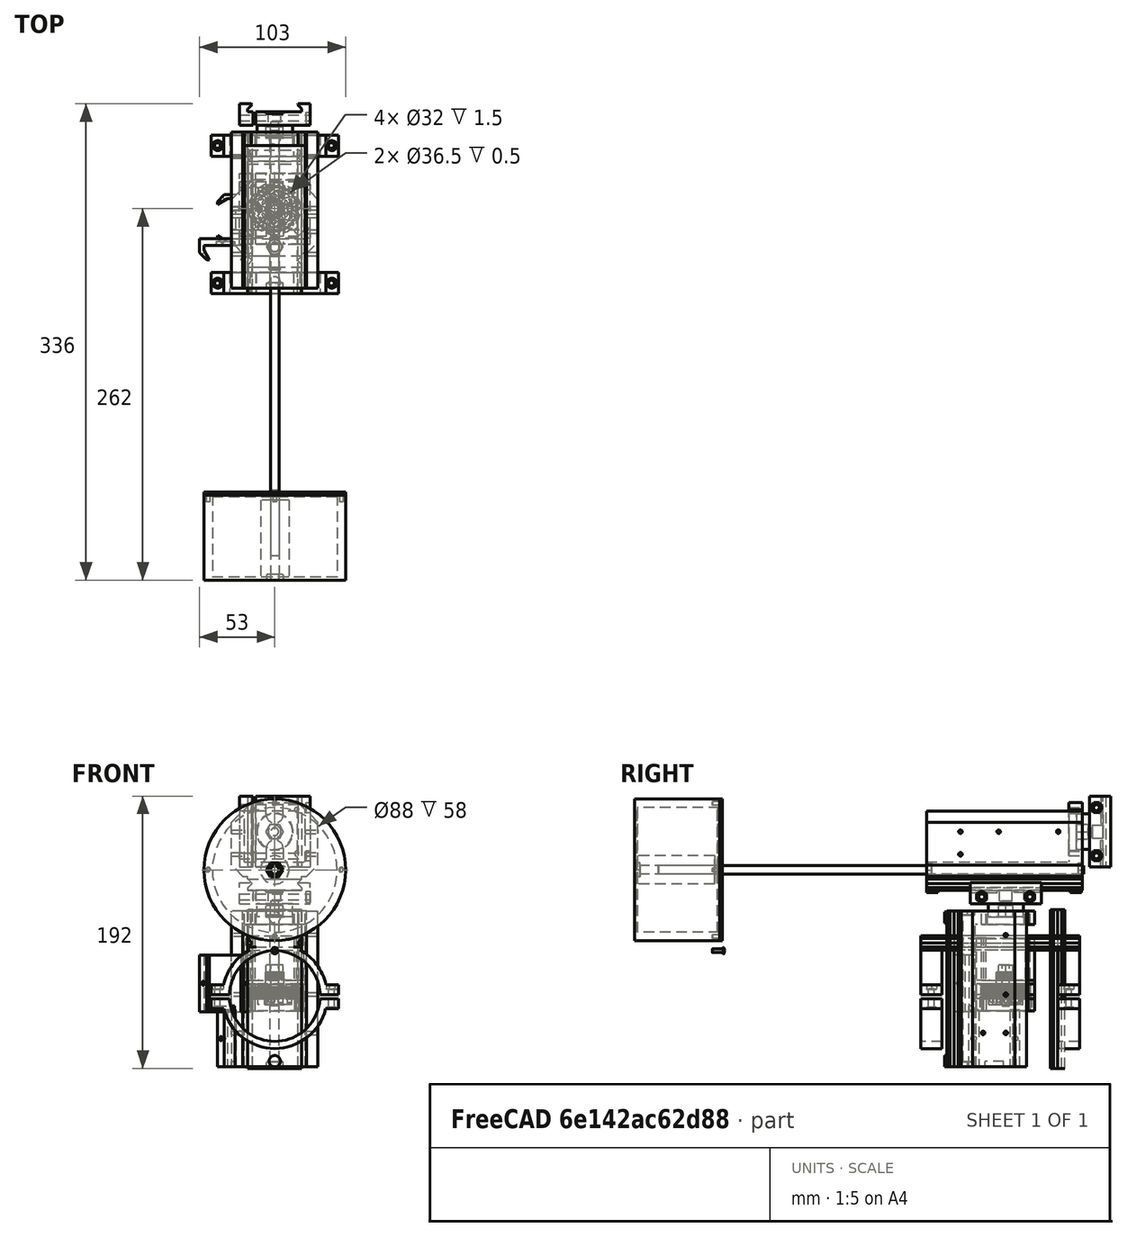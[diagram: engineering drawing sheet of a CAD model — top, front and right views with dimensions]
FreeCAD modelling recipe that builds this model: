
FCSTD DOCUMENT  (FreeCAD 0.17R12284 (Git))
Label: eq-mount-V1.0
License: All rights reserved
LicenseURL: http://en.wikipedia.org/wiki/All_rights_reserved
objects: Part::Feature×227, Part::Cylinder×217, Part::MultiFuse×182, Part::Cut×127, Part::Box×42, Part::FeaturePython×29, Part::Extrusion×25, App::Part×16, Sketcher::SketchObject×11, Part::Chamfer×8, Part::RegularPolygon×4
note: 872 computed .brp shape members not serialized (recipe doc carries the construction recipe); baked Part::Feature solids carry a one-line shape summary decoded from their .brp

FEATURE [Part::FeaturePython] InvoluteGear007  # WARN: FeaturePython — macro-defined, semantics opaque (R4)
  backlash = 0
  beta = 0
  clearance = 0.25
  double_helix = false
  head = 0
  height = 5.5
  module = 1.2
  numpoints = 6
  pressure_angle = 20
  reversed_backlash = false
  shift = 0
  simple = false
  teeth = 27
  undercut = false
FEATURE [Part::FeaturePython] InvoluteGear006  # WARN: FeaturePython — macro-defined, semantics opaque (R4)
  backlash = 0
  beta = 0
  clearance = 0.25
  double_helix = false
  head = 0
  height = 5.5
  module = 1.2
  numpoints = 6
  pressure_angle = 20
  reversed_backlash = false
  shift = 0
  simple = false
  teeth = 27
  undercut = false
FEATURE [Part::FeaturePython] InvoluteGear005  # WARN: FeaturePython — macro-defined, semantics opaque (R4)
  backlash = 0
  beta = 0
  clearance = 0.25
  double_helix = false
  head = 0
  height = 5.5
  module = 1.2
  numpoints = 6
  pressure_angle = 20
  reversed_backlash = false
  shift = 0
  simple = false
  teeth = 27
  undercut = false
FEATURE [Part::Cylinder] Cylinder007  label="Válec007"
  Angle = 360
  AttacherType = Attacher::AttachEngine3D
  Height = 1.5
  Radius = 20
FEATURE [Part::Cylinder] Cylinder008  label="Válec008"
  Angle = 360
  AttacherType = Attacher::AttachEngine3D
  Height = 1.5
  Radius = 16
FEATURE [Part::Cylinder] Cylinder006  label="Válec006"
  Angle = 360
  AttacherType = Attacher::AttachEngine3D
  Height = 1.5
  Radius = 16
FEATURE [Part::Cut] Cut  label="Ring2"
  Base = -> Cylinder007
  Placement = pos=(0,0,5.5) rot=(0,0,1;0rad)
  Tool = -> Cylinder006
FEATURE [Part::Cylinder] Cylinder009  label="Válec009"
  Angle = 360
  AttacherType = Attacher::AttachEngine3D
  Height = 1.5
  Radius = 20
FEATURE [Part::Cut] Cut003  label="Ring003"
  Base = -> Cylinder009
  Placement = pos=(0,0,-1.5) rot=(0,0,1;0rad)
  Tool = -> Cylinder008
FEATURE [Part::Cylinder] Cylinder005  label="Válec005"
  Angle = 360
  AttacherType = Attacher::AttachEngine3D
  Height = 5.5
  Radius = 20
FEATURE [Part::Cut] Cut002  label="ring 001"
  Base = -> Cylinder005
  Tool = -> InvoluteGear005
FEATURE [Part::MultiFuse] Fusion  label="Ring zaklad Fin"
  Shapes = -> [Cut002,Cut,Cut003]
FEATURE [Sketcher::SketchObject] Sketch001
  MapMode = 45
  Placement = pos=(44.88,21.011,5.40003) rot=(0.707106,0.001666,0.707106;3.13826rad)
  sketch-geometry (7):
    g0: LineSegment StartX=5 StartY=0 StartZ=0 EndX=2.5 EndY=4.33013 EndZ=0
    g1: LineSegment StartX=2.5 StartY=4.33013 StartZ=0 EndX=-2.5 EndY=4.33013 EndZ=0
    g2: LineSegment StartX=-2.5 StartY=4.33013 StartZ=0 EndX=-5 EndY=0 EndZ=0
    g3: LineSegment StartX=-5 StartY=0 StartZ=0 EndX=-2.5 EndY=-4.33013 EndZ=0
    g4: LineSegment StartX=-2.5 StartY=-4.33013 StartZ=0 EndX=2.5 EndY=-4.33013 EndZ=0
    g5: LineSegment StartX=2.5 StartY=-4.33013 StartZ=0 EndX=5 EndY=0 EndZ=0
    g6: Circle [constr] CenterX=0 CenterY=0 CenterZ=0 NormalX=0 NormalY=0 NormalZ=1 AngleXU=0 Radius=5
  constraints (14):
    c: Coincident(g0,g1)
    c: Coincident(g1,g2)
    c: Coincident(g2,g3)
    c: Coincident(g3,g4)
    c: Coincident(g4,g5)
    c: Coincident(g5,g0)
    c: Equal(g0, g1-g5) x5
    c: PointOnObject(g0,g6)
    c: PointOnObject(g1,g6)
    c: PointOnObject(g2,g6)
    c: PointOnObject(g3,g6)
    c: PointOnObject(g4,g6)
    c: PointOnObject(g5,g6)
    c: PointOnObject(g6,g-1)
FEATURE [Part::Feature] Cut005_solid001_cs
  Placement = pos=(0,0,-11.25) rot=(0,0,1;0rad)
  shape: bbox 41 x 41 x 3e-07 mm, 0 faces, 0 solids (baked)
FEATURE [Part::Feature] Screw_solid003  label="M2x4-Screw (Solid)003"
  Placement = pos=(0,0,0) rot=(0,0,1;1.0472rad)
  shape: bbox 3.6 x 3.6 x 4 mm, 12 faces (baked)
FEATURE [Part::Feature] Cylinder014002  label="Válec014"
  Placement = pos=(0,0,0) rot=(0,0,1;4.18879rad)
  shape: bbox 16 x 16 x 10 mm, 3 faces (baked)
FEATURE [Part::Feature] Screw_solid004  label="M2x4-Screw (Solid)004"
  Placement = pos=(0,0,0) rot=(0,0,-1;1.0472rad)
  shape: bbox 3.6 x 3.6 x 4 mm, 12 faces (baked)
FEATURE [Part::Feature] Screw_solid005  label="M2x4-Screw (Solid)005"
  Placement = pos=(0,0,0) rot=(0,0,1;3.14159rad)
  shape: bbox 3.6 x 3.6 x 4 mm, 12 faces (baked)
FEATURE [Part::MultiFuse] Fusion004  label="srouby002"
  Shapes = -> [Screw_solid003,Screw_solid004,Screw_solid005]
FEATURE [Part::Feature] Cut008_solid  label="Planet001"
  shape: bbox 12.9 x 13.1 x 5 mm, 57 faces (baked)
FEATURE [Part::Feature] Cylinder014001  label="Válec013"
  Placement = pos=(0,0,0) rot=(0,0,1;2.0944rad)
  shape: bbox 16 x 16 x 10 mm, 3 faces (baked)
FEATURE [Part::Cylinder] Cylinder014005010  label="Unasec vrch001"
  Angle = 360
  AttacherType = Attacher::AttachEngine3D
  Height = 1.5
  Placement = pos=(0,0,5.5) rot=(0,0,1;0rad)
  Radius = 15.5
FEATURE [Part::Cylinder] Cylinder010  label="unasec spodek"
  Angle = 360
  AttacherType = Attacher::AttachEngine3D
  Height = 1.5
  Placement = pos=(0,0,-1.5) rot=(0,0,1;0rad)
  Radius = 15.5
FEATURE [Part::Cylinder] Cylinder  label="Válec"
  Angle = 360
  AttacherType = Attacher::AttachEngine3D
  Height = 10
  Placement = pos=(0,0,-3) rot=(0,0,1;0rad)
  Radius = 7
FEATURE [Part::Cylinder] Cylinder014005007  label="Válec024"
  Angle = 360
  AttacherType = Attacher::AttachEngine3D
  Height = 7.5
  Placement = pos=(0,0,-7) rot=(0,0,1;0rad)
  Radius = 6.5
FEATURE [Part::Cylinder] Cylinder013  label="Válec011"
  Angle = 360
  AttacherType = Attacher::AttachEngine3D
  Height = 10
  Placement = pos=(10.5,0,0) rot=(0,0,1;0rad)
  Radius = 8
FEATURE [Part::MultiFuse] Fusion001
  Shapes = -> [Cylinder,Cylinder013,Cylinder014002,Cylinder014001]
FEATURE [Part::Cylinder] Cylinder011  label="unasec stred"
  Angle = 360
  AttacherType = Attacher::AttachEngine3D
  Height = 7
  Placement = pos=(0,0,-1.5) rot=(0,0,1;0rad)
  Radius = 13.5
FEATURE [Part::MultiFuse] Fusion002
  Shapes = -> [Cylinder011,Cylinder010]
FEATURE [Part::Cut] Cut004  label="unasec spodek001"
  Base = -> Fusion002
  Tool = -> Fusion001
FEATURE [Part::Cut] Cut006  label="Uasec spodek"
  Base = -> Cut004
  Tool = -> Fusion004
FEATURE [Part::Cylinder] Cylinder014005008  label="Válec025"
  Angle = 360
  AttacherType = Attacher::AttachEngine3D
  Height = 15
  Placement = pos=(0,0,-8) rot=(0,0,1;0rad)
  Radius = 2.65
FEATURE [Part::Cylinder] Cylinder014005009  label="Válec026"
  Angle = 360
  AttacherType = Attacher::AttachEngine3D
  Height = 7
  Placement = pos=(0,0,-7) rot=(0,0,1;0rad)
  Radius = 12
FEATURE [Part::Extrusion] Extrude  label="box"
  Base = -> Cut005_solid001_cs
  Dir = (0,0,1)
  DirMode = 2
  FaceMakerClass = Part::FaceMakerBullseye
  LengthFwd = 19
  LengthRev = 0
  Placement = pos=(0,0,-11.5) rot=(0,0,1;0rad)
  Solid = true
  Symmetric = false
FEATURE [Part::RegularPolygon] RegularPolygon  label="Pravidelný n-úhelník"
  AttacherType = Attacher::AttachEngine3D
  Circumradius = 6
  Polygon = 6
FEATURE [Part::Extrusion] Extrude006
  Base = -> RegularPolygon
  Dir = (0,0,1)
  DirMode = 2
  FaceMakerClass = Part::FaceMakerBullseye
  LengthFwd = 8
  LengthRev = 0
  Placement = pos=(0,0,13) rot=(0,0,1;0rad)
  Solid = true
  Symmetric = false
FEATURE [Part::Extrusion] Extrude007
  Base = -> Sketch001
  Dir = (1,0,0)
  DirMode = 2
  FaceMakerClass = Part::FaceMakerBullseye
  LengthFwd = 5
  LengthRev = 0
  Placement = pos=(0,0,0.25) rot=(0,0,1;0rad)
  Solid = true
  Symmetric = false
FEATURE [Part::FeaturePython] InvoluteGear012  # WARN: FeaturePython — macro-defined, semantics opaque (R4)
  backlash = 0
  beta = 0
  clearance = 0.25
  double_helix = false
  head = 0
  height = 5.5
  module = 1.2
  numpoints = 6
  pressure_angle = 20
  reversed_backlash = false
  shift = 0
  simple = false
  teeth = 27
  undercut = false
FEATURE [Part::FeaturePython] InvoluteGear013  # WARN: FeaturePython — macro-defined, semantics opaque (R4)
  backlash = 0
  beta = 0
  clearance = 0.25
  double_helix = false
  head = 0
  height = 5.5
  module = 1.2
  numpoints = 6
  pressure_angle = 20
  reversed_backlash = false
  shift = 0
  simple = false
  teeth = 27
  undercut = false
FEATURE [Part::Feature] Cylinder014005025  label="Válec038"
  Placement = pos=(0,0,0) rot=(0,0,1;2.0944rad)
  shape: bbox 5 x 5 x 7 mm, 3 faces (baked)
FEATURE [Part::Feature] Cylinder014005026  label="Válec039"
  Placement = pos=(0,0,0) rot=(0,0,1;2.0944rad)
  shape: bbox 16 x 16 x 10 mm, 3 faces (baked)
FEATURE [Part::Feature] Cylinder014005024  label="Válec037"
  Placement = pos=(0,0,0) rot=(0,0,1;4.18879rad)
  shape: bbox 16 x 16 x 10 mm, 3 faces (baked)
FEATURE [Part::Feature] Screw_solid006  label="M2x4-Screw (Solid)006"
  Placement = pos=(0,0,0) rot=(0,0,1;1.0472rad)
  shape: bbox 3.6 x 3.6 x 4 mm, 12 faces (baked)
FEATURE [Part::Feature] Screw_solid007  label="M2x4-Screw (Solid)007"
  Placement = pos=(0,0,0) rot=(0,0,-1;1.0472rad)
  shape: bbox 3.6 x 3.6 x 4 mm, 12 faces (baked)
FEATURE [Part::Feature] Cylinder014005006  label="Válec023"
  Placement = pos=(0,0,0) rot=(0,0,1;4.18879rad)
  shape: bbox 5 x 5 x 7 mm, 3 faces (baked)
FEATURE [Part::Feature] Cut008_solid001  label="Planet002"
  Placement = pos=(0,0,0) rot=(0,0,1;2.0944rad)
  shape: bbox 12.9 x 13.1 x 5 mm, 57 faces (baked)
FEATURE [Part::Feature] Cut008_solid002  label="Planet003"
  Placement = pos=(0,0,0) rot=(0,0,1;4.18879rad)
  shape: bbox 12.9 x 13.1 x 5 mm, 57 faces (baked)
FEATURE [Part::Feature] Cut007_solid  label="Sun1"
  shape: bbox 12.9 x 13.1 x 5 mm, 57 faces (baked)
FEATURE [Part::MultiFuse] Fusion010
  Shapes = -> [Cut007_solid,Cylinder014005007,Cylinder014005009]
FEATURE [Part::Feature] Screw_solid008  label="M2x4-Screw (Solid)008"
  Placement = pos=(0,0,0) rot=(0,0,1;3.14159rad)
  shape: bbox 3.6 x 3.6 x 4 mm, 12 faces (baked)
FEATURE [Part::MultiFuse] Fusion011  label="srouby003"
  Placement = pos=(0,0,0.5) rot=(0,0,1;0rad)
  Shapes = -> [Screw_solid006,Screw_solid007,Screw_solid008]
FEATURE [Part::Cut] Cut012  label="unasec vrch001"
  Base = -> Cylinder014005010
  Tool = -> Fusion011
FEATURE [Part::Feature] Cylinder014005005  label="Válec022"
  Placement = pos=(0,0,0) rot=(0,0,1;2.0944rad)
  shape: bbox 5 x 5 x 7 mm, 3 faces (baked)
FEATURE [Part::Feature] Cylinder014005013  label="Válec029"
  Placement = pos=(0,0,0) rot=(0,0,1;2.0944rad)
  shape: bbox 5 x 5 x 7 mm, 3 faces (baked)
FEATURE [Part::Feature] Cylinder014005004  label="Válec021"
  shape: bbox 5 x 5 x 7 mm, 3 faces (baked)
FEATURE [Part::MultiFuse] Fusion006
  Shapes = -> [Cylinder014005006,Cylinder014005004,Cylinder014005005]
FEATURE [Part::MultiFuse] Fusion008  label="Unasec spdek final"
  Shapes = -> [Cut006,Fusion006]
FEATURE [Part::Feature] Cylinder014005012  label="Válec028"
  shape: bbox 5 x 5 x 7 mm, 3 faces (baked)
FEATURE [Part::Feature] Cylinder014005014  label="Válec030"
  Placement = pos=(0,0,0) rot=(0,0,1;4.18879rad)
  shape: bbox 5 x 5 x 7 mm, 3 faces (baked)
FEATURE [Part::MultiFuse] Fusion012
  Shapes = -> [Cylinder014005014,Cylinder014005012,Cylinder014005013]
FEATURE [Part::Feature] Cut008_solid003  label="Planet004"
  Placement = pos=(0,0,0) rot=(0,0,1;4.18879rad)
  shape: bbox 12.9 x 13.1 x 5 mm, 57 faces (baked)
FEATURE [Part::Cylinder] Cylinder014005016  label="unasec spodek003"
  Angle = 360
  AttacherType = Attacher::AttachEngine3D
  Height = 1.5
  Placement = pos=(0,0,-1.5) rot=(0,0,1;0rad)
  Radius = 15.5
FEATURE [Part::Cylinder] Cylinder014005035  label="Válec048"
  Angle = 360
  AttacherType = Attacher::AttachEngine3D
  Height = 18
  Radius = 2.6
FEATURE [Part::Cylinder] Cylinder014005032  label="Válec045"
  Angle = 360
  AttacherType = Attacher::AttachEngine3D
  Height = 1.5
  Radius = 16
FEATURE [Part::Cylinder] Cylinder014005015  label="Válec031"
  Angle = 360
  AttacherType = Attacher::AttachEngine3D
  Height = 10
  Placement = pos=(0,0,-3) rot=(0,0,1;0rad)
  Radius = 7
FEATURE [Part::Cylinder] Cylinder014005029  label="Válec042"
  Angle = 360
  AttacherType = Attacher::AttachEngine3D
  Height = 1.5
  Radius = 16
FEATURE [Part::Cylinder] Cylinder014005031  label="Válec044"
  Angle = 360
  AttacherType = Attacher::AttachEngine3D
  Height = 1.5
  Radius = 20
FEATURE [Part::Cut] Cut017  label="Ring005"
  Base = -> Cylinder014005031
  Placement = pos=(0,0,-1.5) rot=(0,0,1;0rad)
  Tool = -> Cylinder014005032
FEATURE [Part::Cylinder] Cylinder014005034  label="Válec047"
  Angle = 360
  AttacherType = Attacher::AttachEngine3D
  Height = 4
  Placement = pos=(0,0,7) rot=(0,0,1;0rad)
  Radius = 6.5
FEATURE [Part::Cylinder] Cylinder014005036  label="Válec049"
  Angle = 360
  AttacherType = Attacher::AttachEngine3D
  Height = 4
  Placement = pos=(0,0,7) rot=(0,0,1;0rad)
  Radius = 6.5
FEATURE [Part::Cylinder] Cylinder014005041  label="Unasec vrch003"
  Angle = 360
  AttacherType = Attacher::AttachEngine3D
  Height = 1.5
  Placement = pos=(0,0,5.5) rot=(0,0,1;0rad)
  Radius = 15.5
FEATURE [Part::Cylinder] Cylinder014005011  label="Válec027"
  Angle = 360
  AttacherType = Attacher::AttachEngine3D
  Height = 7
  Radius = 2.6
FEATURE [Part::MultiFuse] Fusion013
  Placement = pos=(0,0,1) rot=(0,0,1;0rad)
  Shapes = -> [Fusion012,Cylinder014005011]
FEATURE [Part::Cut] Cut011  label="Unasec Vrch zaklad001"
  Base = -> Cut012
  Tool = -> Fusion013
FEATURE [Part::Cylinder] Cylinder014005017  label="unasec stred001"
  Angle = 360
  AttacherType = Attacher::AttachEngine3D
  Height = 7
  Placement = pos=(0,0,-1.5) rot=(0,0,1;0rad)
  Radius = 13.5
FEATURE [Part::Cylinder] Cylinder014005018  label="Válec032"
  Angle = 360
  AttacherType = Attacher::AttachEngine3D
  Height = 10
  Placement = pos=(10.5,0,0) rot=(0,0,1;0rad)
  Radius = 8
FEATURE [Part::MultiFuse] Fusion017
  Shapes = -> [Cylinder014005015,Cylinder014005018,Cylinder014005024,Cylinder014005026]
FEATURE [Part::Cylinder] Cylinder014005030  label="Válec043"
  Angle = 360
  AttacherType = Attacher::AttachEngine3D
  Height = 1.5
  Radius = 20
FEATURE [Part::Cut] Cut014  label="Ring004"
  Base = -> Cylinder014005030
  Placement = pos=(0,0,5.5) rot=(0,0,1;0rad)
  Tool = -> Cylinder014005029
FEATURE [Part::Cylinder] Cylinder014005033  label="Válec046"
  Angle = 360
  AttacherType = Attacher::AttachEngine3D
  Height = 5.5
  Radius = 20
FEATURE [Part::Cut] Cut015  label="ring 002"
  Base = -> Cylinder014005033
  Tool = -> InvoluteGear006
FEATURE [Part::Cylinder] Cylinder014005037  label="Válec050"
  Angle = 360
  AttacherType = Attacher::AttachEngine3D
  Height = 18
  Radius = 2.6
FEATURE [Part::Cylinder] Cylinder014005051  label="Válec063"
  Angle = 360
  AttacherType = Attacher::AttachEngine3D
  Height = 7
  Radius = 2.6
FEATURE [Part::Cylinder] Cylinder014005052  label="Válec064"
  Angle = 360
  AttacherType = Attacher::AttachEngine3D
  Height = 10
  Placement = pos=(0,0,-3) rot=(0,0,1;0rad)
  Radius = 7
FEATURE [Part::Cylinder] Cylinder014005042  label="Válec054"
  Angle = 360
  AttacherType = Attacher::AttachEngine3D
  Height = 7
  Radius = 2.6
FEATURE [Part::Cylinder] Cylinder014005054  label="Válec065"
  Angle = 360
  AttacherType = Attacher::AttachEngine3D
  Height = 10
  Placement = pos=(10.5,0,0) rot=(0,0,1;0rad)
  Radius = 8
FEATURE [Part::Cylinder] Cylinder014005056  label="Válec066"
  Angle = 360
  AttacherType = Attacher::AttachEngine3D
  Height = 1.5
  Radius = 16
FEATURE [Part::Cylinder] Cylinder014005053  label="unasec stred002"
  Angle = 360
  AttacherType = Attacher::AttachEngine3D
  Height = 7
  Placement = pos=(0,0,-1.5) rot=(0,0,1;0rad)
  Radius = 13.5
FEATURE [Part::Cylinder] Cylinder014005057  label="Válec067"
  Angle = 360
  AttacherType = Attacher::AttachEngine3D
  Height = 4
  Placement = pos=(0,0,7) rot=(0,0,1;0rad)
  Radius = 6.5
FEATURE [Part::Cylinder] Cylinder014005055  label="unasec spodek005"
  Angle = 360
  AttacherType = Attacher::AttachEngine3D
  Height = 1.5
  Placement = pos=(0,0,-1.5) rot=(0,0,1;0rad)
  Radius = 15.5
FEATURE [Part::Feature] Screw_solid016  label="M2x4-Screw (Solid)016"
  Placement = pos=(0,0,0) rot=(0,0,1;3.14159rad)
  shape: bbox 3.6 x 3.6 x 4 mm, 12 faces (baked)
FEATURE [Part::Feature] Screw_solid014  label="M2x4-Screw (Solid)014"
  Placement = pos=(0,0,0) rot=(0,0,-1;1.0472rad)
  shape: bbox 3.6 x 3.6 x 4 mm, 12 faces (baked)
FEATURE [Part::Feature] Cylinder014005027  label="Válec040"
  shape: bbox 5 x 5 x 7 mm, 3 faces (baked)
FEATURE [Part::Feature] Screw_solid015  label="M2x4-Screw (Solid)015"
  Placement = pos=(0,0,0) rot=(0,0,-1;1.0472rad)
  shape: bbox 3.6 x 3.6 x 4 mm, 12 faces (baked)
FEATURE [Part::Feature] Screw_solid011  label="M2x4-Screw (Solid)011"
  Placement = pos=(0,0,0) rot=(0,0,1;3.14159rad)
  shape: bbox 3.6 x 3.6 x 4 mm, 12 faces (baked)
FEATURE [Part::Feature] Cut008_solid004  label="Planet005"
  shape: bbox 12.9 x 13.1 x 5 mm, 57 faces (baked)
FEATURE [Part::Feature] Cylinder014005028  label="Válec041"
  Placement = pos=(0,0,0) rot=(0,0,1;4.18879rad)
  shape: bbox 5 x 5 x 7 mm, 3 faces (baked)
FEATURE [Part::Feature] Cut007_solid001  label="Sun2"
  Placement = pos=(0,0,10.5) rot=(0,0,1;0rad)
  shape: bbox 12.9 x 13.1 x 5 mm, 57 faces (baked)
FEATURE [Part::Feature] Cut008_solid005  label="Planet006"
  Placement = pos=(0,0,0) rot=(0,0,1;2.0944rad)
  shape: bbox 12.9 x 13.1 x 5 mm, 57 faces (baked)
FEATURE [Part::Feature] Cut007_solid002  label="Sun003"
  Placement = pos=(0,0,10.5) rot=(0,0,1;0rad)
  shape: bbox 12.9 x 13.1 x 5 mm, 57 faces (baked)
FEATURE [Part::Feature] Screw_solid013  label="M2x4-Screw (Solid)013"
  Placement = pos=(0,0,0) rot=(0,0,1;1.0472rad)
  shape: bbox 3.6 x 3.6 x 4 mm, 12 faces (baked)
FEATURE [Part::MultiFuse] Fusion018
  Shapes = -> [Cylinder014005017,Cylinder014005016]
FEATURE [Part::Cut] Cut016  label="unasec spodek002"
  Base = -> Fusion018
  Tool = -> Fusion017
FEATURE [Part::MultiFuse] Fusion028  label="Tělo I"
  Shapes = -> [Extrude,Fusion]
FEATURE [Part::MultiFuse] Fusion019  label="srouby005"
  Shapes = -> [Screw_solid013,Screw_solid014,Screw_solid011]
FEATURE [Part::Cut] Cut018  label="Uasec spodek001"
  Base = -> Cut016
  Tool = -> Fusion019
FEATURE [Part::MultiFuse] Fusion023  label="unasec vrhch 2"
  Shapes = -> [Cut011,Cut007_solid001,Cylinder014005034]
FEATURE [Part::Cut] Cut020  label="Unasec + Sun"
  Base = -> Fusion023
  Tool = -> Cylinder014005035
FEATURE [Part::MultiFuse] Fusion021
  Shapes = -> [Cylinder014005028,Cylinder014005027,Cylinder014005025]
FEATURE [Part::MultiFuse] Fusion020  label="Unasec spdek final001"
  Shapes = -> [Cut018,Fusion021]
FEATURE [Part::MultiFuse] Fusion030
  Shapes = -> [Cylinder014005053,Cylinder014005055]
FEATURE [Part::MultiFuse] Fusion022  label="Ring zaklad Fin001"
  Shapes = -> [Cut015,Cut014,Cut017]
FEATURE [Part::Feature] Cut008_solid007  label="Planet008"
  shape: bbox 12.9 x 13.1 x 5 mm, 57 faces (baked)
FEATURE [Part::Feature] Screw_solid022  label="M2x4-Screw (Solid)022"
  Placement = pos=(0,0,0) rot=(0,0,1;3.14159rad)
  shape: bbox 3.6 x 3.6 x 4 mm, 12 faces (baked)
FEATURE [Part::Feature] Cylinder014005048  label="Válec060"
  Placement = pos=(0,0,0) rot=(0,0,1;4.18879rad)
  shape: bbox 16 x 16 x 10 mm, 3 faces (baked)
FEATURE [Part::Feature] Cylinder014005049  label="Válec061"
  Placement = pos=(0,0,0) rot=(0,0,1;2.0944rad)
  shape: bbox 5 x 5 x 7 mm, 3 faces (baked)
FEATURE [Part::Feature] Cylinder014005050  label="Válec062"
  Placement = pos=(0,0,0) rot=(0,0,1;2.0944rad)
  shape: bbox 16 x 16 x 10 mm, 3 faces (baked)
FEATURE [Part::MultiFuse] Fusion031
  Shapes = -> [Cylinder014005052,Cylinder014005054,Cylinder014005048,Cylinder014005050]
FEATURE [Part::Cut] Cut030  label="unasec spodek004"
  Base = -> Fusion030
  Tool = -> Fusion031
FEATURE [Part::Feature] Cylinder014005040  label="Válec053"
  Placement = pos=(0,0,0) rot=(0,0,1;2.0944rad)
  shape: bbox 5 x 5 x 7 mm, 3 faces (baked)
FEATURE [Part::Feature] Cylinder014005039  label="Válec052"
  shape: bbox 5 x 5 x 7 mm, 3 faces (baked)
FEATURE [Part::Feature] Screw_solid019  label="M2x4-Screw (Solid)019"
  Placement = pos=(0,0,0) rot=(0,0,-1;1.0472rad)
  shape: bbox 3.6 x 3.6 x 4 mm, 12 faces (baked)
FEATURE [Part::Feature] Cut008_solid008  label="Planet009"
  Placement = pos=(0,0,0) rot=(0,0,1;4.18879rad)
  shape: bbox 12.9 x 13.1 x 5 mm, 57 faces (baked)
FEATURE [Part::Feature] Cut005_solid001_cs003
  Placement = pos=(0,0,-11.25) rot=(0,0,1;0rad)
  shape: bbox 41 x 41 x 3e-07 mm, 0 faces, 0 solids (baked)
FEATURE [Part::Extrusion] Extrude002  label="box002"
  Base = -> Cut005_solid001_cs003
  Dir = (0,0,1)
  DirMode = 2
  FaceMakerClass = Part::FaceMakerBullseye
  LengthFwd = 10.5
  LengthRev = 0
  Placement = pos=(0,0,-3) rot=(0,0,1;0rad)
  Solid = true
  Symmetric = false
FEATURE [Part::Feature] Screw_solid023  label="M2x4-Screw (Solid)023"
  Placement = pos=(0,0,0) rot=(0,0,1;1.0472rad)
  shape: bbox 3.6 x 3.6 x 4 mm, 12 faces (baked)
FEATURE [Part::Feature] Cylinder014005046  label="Válec058"
  Placement = pos=(0,0,0) rot=(0,0,1;4.18879rad)
  shape: bbox 5 x 5 x 7 mm, 3 faces (baked)
FEATURE [Part::Feature] Cut005_solid001_cs002
  Placement = pos=(0,0,-11.25) rot=(0,0,1;0rad)
  shape: bbox 41 x 41 x 3e-07 mm, 0 faces, 0 solids (baked)
FEATURE [Part::Extrusion] Extrude001  label="box001"
  Base = -> Cut005_solid001_cs002
  Dir = (0,0,1)
  DirMode = 2
  FaceMakerClass = Part::FaceMakerBullseye
  LengthFwd = 10.5
  LengthRev = 0
  Placement = pos=(0,0,-3) rot=(0,0,1;0rad)
  Solid = true
  Symmetric = false
FEATURE [Part::MultiFuse] Fusion029  label="teloII"
  Shapes = -> [Fusion022,Extrude001]
FEATURE [Part::Feature] Screw_solid017  label="M2x4-Screw (Solid)017"
  Placement = pos=(0,0,0) rot=(0,0,1;1.0472rad)
  shape: bbox 3.6 x 3.6 x 4 mm, 12 faces (baked)
FEATURE [Part::MultiFuse] Fusion027  label="srouby006"
  Placement = pos=(0,0,0.5) rot=(0,0,1;0rad)
  Shapes = -> [Screw_solid017,Screw_solid015,Screw_solid016]
FEATURE [Part::Cut] Cut021  label="unasec vrch003"
  Base = -> Cylinder014005041
  Tool = -> Fusion027
FEATURE [Part::Feature] Cylinder014005045  label="Válec057"
  Placement = pos=(0,0,0) rot=(0,0,1;4.18879rad)
  shape: bbox 5 x 5 x 7 mm, 3 faces (baked)
FEATURE [Part::Feature] Cut007_solid003  label="Sun004"
  Placement = pos=(0,0,10.5) rot=(0,0,1;0rad)
  shape: bbox 12.9 x 13.1 x 5 mm, 57 faces (baked)
FEATURE [Part::Feature] Cylinder014005047  label="Válec059"
  shape: bbox 5 x 5 x 7 mm, 3 faces (baked)
FEATURE [Part::MultiFuse] Fusion033
  Shapes = -> [Cylinder014005045,Cylinder014005047,Cylinder014005049]
FEATURE [Part::Feature] Screw_solid021  label="M2x4-Screw (Solid)021"
  Placement = pos=(0,0,0) rot=(0,0,-1;1.0472rad)
  shape: bbox 3.6 x 3.6 x 4 mm, 12 faces (baked)
FEATURE [Part::MultiFuse] Fusion039  label="srouby008"
  Shapes = -> [Screw_solid023,Screw_solid021,Screw_solid022]
FEATURE [Part::Cut] Cut031  label="Uasec spodek002"
  Base = -> Cut030
  Tool = -> Fusion039
FEATURE [Part::MultiFuse] Fusion040  label="Unasec spdek final002"
  Shapes = -> [Cut031,Fusion033]
FEATURE [Part::Feature] Cylinder014005044  label="Válec056"
  Placement = pos=(0,0,0) rot=(0,0,1;2.0944rad)
  shape: bbox 5 x 5 x 7 mm, 3 faces (baked)
FEATURE [Part::Feature] Cylinder014005038  label="Válec051"
  Placement = pos=(0,0,0) rot=(0,0,1;4.18879rad)
  shape: bbox 5 x 5 x 7 mm, 3 faces (baked)
FEATURE [Part::MultiFuse] Fusion026
  Shapes = -> [Cylinder014005038,Cylinder014005039,Cylinder014005040]
FEATURE [Part::MultiFuse] Fusion025
  Placement = pos=(0,0,1) rot=(0,0,1;0rad)
  Shapes = -> [Fusion026,Cylinder014005042]
FEATURE [Part::Cut] Cut022  label="Unasec Vrch zaklad003"
  Base = -> Cut021
  Tool = -> Fusion025
FEATURE [Part::MultiFuse] Fusion024  label="unasec vrhch 003"
  Shapes = -> [Cut022,Cut007_solid002,Cylinder014005036]
FEATURE [Part::Cut] Cut023  label="Unasec + Sun001"
  Base = -> Fusion024
  Tool = -> Cylinder014005037
FEATURE [App::Part] Part  label="Part020"
  Group = -> [Cut016,Cut018,Cylinder014005015,Cylinder014005016,Cylinder014005017,Cylinder014005018,Cylinder014005024,Cylinder014005025,Cylinder014005026,Screw_solid011,Cylinder014005027,Screw_solid013,Cylinder014005028,Screw_solid014,Fusion017,Fusion018,Fusion019,Fusion021,Fusion020,Cut008_solid004,Cut008_solid005,Cut008_solid003,Screw_solid017,Cylinder014005039,Cylinder014005040,Screw_solid015,Screw_solid016,+26 more]
  License = CC BY 3.0
  LicenseURL = http://creativecommons.org/licenses/by/3.0/
  Origin = -> Origin
  Placement = pos=(0,0,10.5) rot=(0,0,1;0rad)
FEATURE [Part::Feature] Cut008_solid006  label="Planet007"
  Placement = pos=(0,0,0) rot=(0,0,1;2.0944rad)
  shape: bbox 12.9 x 13.1 x 5 mm, 57 faces (baked)
FEATURE [Part::Feature] Screw_solid020  label="M2x4-Screw (Solid)020"
  Placement = pos=(0,0,0) rot=(0,0,1;3.14159rad)
  shape: bbox 3.6 x 3.6 x 4 mm, 12 faces (baked)
FEATURE [Part::Feature] Cylinder014005043  label="Válec055"
  shape: bbox 5 x 5 x 7 mm, 3 faces (baked)
FEATURE [Part::MultiFuse] Fusion038
  Shapes = -> [Cylinder014005046,Cylinder014005043,Cylinder014005044]
FEATURE [Part::MultiFuse] Fusion035
  Placement = pos=(0,0,1) rot=(0,0,1;0rad)
  Shapes = -> [Fusion038,Cylinder014005051]
FEATURE [Part::Feature] Screw_solid018  label="M2x4-Screw (Solid)018"
  Placement = pos=(0,0,0) rot=(0,0,1;1.0472rad)
  shape: bbox 3.6 x 3.6 x 4 mm, 12 faces (baked)
FEATURE [Part::MultiFuse] Fusion036  label="srouby007"
  Placement = pos=(0,0,0.5) rot=(0,0,1;0rad)
  Shapes = -> [Screw_solid018,Screw_solid019,Screw_solid020]
FEATURE [Part::Cylinder] Cylinder014005060  label="Válec070"
  Angle = 360
  AttacherType = Attacher::AttachEngine3D
  Height = 5.5
  Radius = 20
FEATURE [Part::Cut] Cut024  label="ring 003"
  Base = -> Cylinder014005060
  Tool = -> InvoluteGear007
FEATURE [Part::Cylinder] Cylinder014005063  label="Válec072"
  Angle = 360
  AttacherType = Attacher::AttachEngine3D
  Height = 1.5
  Radius = 20
FEATURE [Part::Cut] Cut029  label="Ring007"
  Base = -> Cylinder014005063
  Placement = pos=(0,0,5.5) rot=(0,0,1;0rad)
  Tool = -> Cylinder014005056
FEATURE [Part::Cylinder] Cylinder014005058  label="Válec068"
  Angle = 360
  AttacherType = Attacher::AttachEngine3D
  Height = 1.5
  Radius = 16
FEATURE [Part::Cylinder] Cylinder014005059  label="Válec069"
  Angle = 360
  AttacherType = Attacher::AttachEngine3D
  Height = 18
  Radius = 2.6
FEATURE [Part::Cylinder] Cylinder014005062  label="Válec071"
  Angle = 360
  AttacherType = Attacher::AttachEngine3D
  Height = 1.5
  Radius = 20
FEATURE [Part::Cut] Cut025  label="Ring006"
  Base = -> Cylinder014005062
  Placement = pos=(0,0,-1.5) rot=(0,0,1;0rad)
  Tool = -> Cylinder014005058
FEATURE [Part::MultiFuse] Fusion034  label="Ring zaklad Fin002"
  Shapes = -> [Cut024,Cut029,Cut025]
FEATURE [Part::MultiFuse] Fusion032  label="teloII001"
  Shapes = -> [Fusion034,Extrude002]
FEATURE [Part::Cylinder] Cylinder014005061  label="Unasec vrch004"
  Angle = 360
  AttacherType = Attacher::AttachEngine3D
  Height = 1.5
  Placement = pos=(0,0,5.5) rot=(0,0,1;0rad)
  Radius = 15.5
FEATURE [Part::Cut] Cut028  label="unasec vrch004"
  Base = -> Cylinder014005061
  Tool = -> Fusion036
FEATURE [Part::Cut] Cut027  label="Unasec Vrch zaklad004"
  Base = -> Cut028
  Tool = -> Fusion035
FEATURE [Part::MultiFuse] Fusion037  label="unasec vrhch 004"
  Shapes = -> [Cut027,Cut007_solid003,Cylinder014005057]
FEATURE [Part::Cut] Cut026  label="Unasec + Sun002"
  Base = -> Fusion037
  Tool = -> Cylinder014005059
FEATURE [App::Part] Part002  label="Part019"
  Group = -> [Cut030,Cut031,Cylinder014005052,Cylinder014005055,Cylinder014005053,Cylinder014005054,Cylinder014005048,Cylinder014005049,Cylinder014005050,Screw_solid022,Cylinder014005047,Screw_solid023,Cylinder014005045,Screw_solid021,Fusion031,Fusion030,Fusion039,Fusion033,Fusion040,Cut008_solid007,Cut008_solid006,Cut008_solid008,Screw_solid018,Cylinder014005043,Cylinder014005044,Screw_solid019,Screw_solid020,+26 more]
  License = CC BY 3.0
  LicenseURL = http://creativecommons.org/licenses/by/3.0/
  Origin = -> Origin002
  Placement = pos=(0,0,21) rot=(0,0,1;0rad)
FEATURE [Part::Feature] Cut007_solid005  label="Sun006"
  Placement = pos=(0,0,10.5) rot=(0,0,1;0rad)
  shape: bbox 12.9 x 13.1 x 5 mm, 57 faces (baked)
FEATURE [Part::Feature] Cylinder014005109  label="Válec111"
  Placement = pos=(0,0,0) rot=(0,0,1;2.0944rad)
  shape: bbox 16 x 16 x 10 mm, 3 faces (baked)
FEATURE [Part::Feature] Cylinder014005108  label="Válec110"
  Placement = pos=(0,0,0) rot=(0,0,1;2.0944rad)
  shape: bbox 5 x 5 x 7 mm, 3 faces (baked)
FEATURE [Part::Feature] Cut008_solid013  label="Planet014"
  Placement = pos=(0,0,0) rot=(0,0,1;4.18879rad)
  shape: bbox 12.9 x 13.1 x 5 mm, 57 faces (baked)
FEATURE [Part::Feature] Cut008_solid014  label="Planet015"
  shape: bbox 12.9 x 13.1 x 5 mm, 57 faces (baked)
FEATURE [Part::Feature] Screw_solid038  label="M2x4-Screw (Solid)038"
  Placement = pos=(0,0,0) rot=(0,0,1;1.0472rad)
  shape: bbox 3.6 x 3.6 x 4 mm, 12 faces (baked)
FEATURE [Part::Feature] Cut005_solid001_cs005
  Placement = pos=(0,0,-11.25) rot=(0,0,1;0rad)
  shape: bbox 41 x 41 x 3e-07 mm, 0 faces, 0 solids (baked)
FEATURE [Part::Extrusion] Extrude004  label="box004"
  Base = -> Cut005_solid001_cs005
  Dir = (0,0,1)
  DirMode = 2
  FaceMakerClass = Part::FaceMakerBullseye
  LengthFwd = 10.5
  LengthRev = 0
  Placement = pos=(0,0,-3) rot=(0,0,1;0rad)
  Solid = true
  Symmetric = false
FEATURE [Part::Feature] Cylinder014005118  label="Válec119"
  shape: bbox 5 x 5 x 7 mm, 3 faces (baked)
FEATURE [Part::Feature] Cut007_solid006  label="Sun007"
  Placement = pos=(0,0,10.5) rot=(0,0,1;0rad)
  shape: bbox 12.9 x 13.1 x 5 mm, 57 faces (baked)
FEATURE [Part::Feature] Cylinder014005103  label="Válec105"
  Placement = pos=(0,0,0) rot=(0,0,1;2.0944rad)
  shape: bbox 5 x 5 x 7 mm, 3 faces (baked)
FEATURE [Part::Feature] Screw_solid035  label="M2x4-Screw (Solid)035"
  Placement = pos=(0,0,0) rot=(0,0,1;3.14159rad)
  shape: bbox 3.6 x 3.6 x 4 mm, 12 faces (baked)
FEATURE [Part::Feature] Cylinder014005102  label="Válec104"
  Placement = pos=(0,0,0) rot=(0,0,1;4.18879rad)
  shape: bbox 5 x 5 x 7 mm, 3 faces (baked)
FEATURE [Part::Feature] Cylinder014005106  label="Válec108"
  Placement = pos=(0,0,0) rot=(0,0,1;4.18879rad)
  shape: bbox 5 x 5 x 7 mm, 3 faces (baked)
FEATURE [Part::Feature] Screw_solid033  label="M2x4-Screw (Solid)033"
  Placement = pos=(0,0,0) rot=(0,0,1;1.0472rad)
  shape: bbox 3.6 x 3.6 x 4 mm, 12 faces (baked)
FEATURE [Part::Feature] Cut008_solid012  label="Planet013"
  Placement = pos=(0,0,0) rot=(0,0,1;2.0944rad)
  shape: bbox 12.9 x 13.1 x 5 mm, 57 faces (baked)
FEATURE [Part::Feature] Screw_solid036  label="M2x4-Screw (Solid)036"
  Placement = pos=(0,0,0) rot=(0,0,-1;1.0472rad)
  shape: bbox 3.6 x 3.6 x 4 mm, 12 faces (baked)
FEATURE [Part::Feature] Cylinder014005107  label="Válec109"
  shape: bbox 5 x 5 x 7 mm, 3 faces (baked)
FEATURE [Part::MultiFuse] Fusion063
  Shapes = -> [Cylinder014005106,Cylinder014005107,Cylinder014005103]
FEATURE [Part::Feature] Cylinder014005105  label="Válec107"
  Placement = pos=(0,0,0) rot=(0,0,1;4.18879rad)
  shape: bbox 16 x 16 x 10 mm, 3 faces (baked)
FEATURE [Part::Feature] Cylinder014005104  label="Válec106"
  shape: bbox 5 x 5 x 7 mm, 3 faces (baked)
FEATURE [Part::MultiFuse] Fusion062
  Shapes = -> [Cylinder014005102,Cylinder014005104,Cylinder014005108]
FEATURE [Part::Feature] Screw_solid037  label="M2x4-Screw (Solid)037"
  Placement = pos=(0,0,0) rot=(0,0,-1;1.0472rad)
  shape: bbox 3.6 x 3.6 x 4 mm, 12 faces (baked)
FEATURE [Part::MultiFuse] Fusion066  label="srouby013"
  Placement = pos=(0,0,0.5) rot=(0,0,1;0rad)
  Shapes = -> [Screw_solid033,Screw_solid037,Screw_solid035]
FEATURE [Part::Feature] Screw_solid034  label="M2x4-Screw (Solid)034"
  Placement = pos=(0,0,0) rot=(0,0,1;3.14159rad)
  shape: bbox 3.6 x 3.6 x 4 mm, 12 faces (baked)
FEATURE [Part::MultiFuse] Fusion065  label="srouby012"
  Shapes = -> [Screw_solid038,Screw_solid036,Screw_solid034]
FEATURE [Part::Cylinder] Cylinder014005101  label="Válec103"
  Angle = 360
  AttacherType = Attacher::AttachEngine3D
  Height = 10
  Placement = pos=(10.5,0,0) rot=(0,0,1;0rad)
  Radius = 8
FEATURE [Part::Cylinder] Cylinder014005110  label="Válec112"
  Angle = 360
  AttacherType = Attacher::AttachEngine3D
  Height = 1.5
  Radius = 16
FEATURE [Part::Cylinder] Cylinder014005098  label="Válec102"
  Angle = 360
  AttacherType = Attacher::AttachEngine3D
  Height = 10
  Placement = pos=(0,0,-3) rot=(0,0,1;0rad)
  Radius = 7
FEATURE [Part::MultiFuse] Fusion059
  Shapes = -> [Cylinder014005098,Cylinder014005101,Cylinder014005105,Cylinder014005109]
FEATURE [Part::Cylinder] Cylinder014005112  label="Válec114"
  Angle = 360
  AttacherType = Attacher::AttachEngine3D
  Height = 1.5
  Radius = 20
FEATURE [Part::Cylinder] Cylinder014005117  label="Válec118"
  Angle = 360
  AttacherType = Attacher::AttachEngine3D
  Height = 18
  Radius = 2.6
FEATURE [Part::Cylinder] Cylinder014005114  label="Válec116"
  Angle = 360
  AttacherType = Attacher::AttachEngine3D
  Height = 1.5
  Radius = 20
FEATURE [Part::Cut] Cut046  label="Ring011"
  Base = -> Cylinder014005114
  Placement = pos=(0,0,-1.5) rot=(0,0,1;0rad)
  Tool = -> Cylinder014005110
FEATURE [Part::Cylinder] Cylinder014005121  label="Válec122"
  Angle = 360
  AttacherType = Attacher::AttachEngine3D
  Height = 1.5
  Radius = 16
FEATURE [Part::Cylinder] Cylinder014005111  label="Válec113"
  Angle = 360
  AttacherType = Attacher::AttachEngine3D
  Height = 5.5
  Radius = 20
FEATURE [Part::Cut] Cut045  label="ring 005"
  Base = -> Cylinder014005111
  Tool = -> InvoluteGear012
FEATURE [Part::Cylinder] Cylinder014005119  label="Válec120"
  Angle = 360
  AttacherType = Attacher::AttachEngine3D
  Height = 1.5
  Radius = 20
FEATURE [Part::Cut] Cut054  label="Ring013"
  Base = -> Cylinder014005119
  Placement = pos=(0,0,5.5) rot=(0,0,1;0rad)
  Tool = -> Cylinder014005121
FEATURE [Part::Cylinder] Cylinder014005099  label="unasec stred005"
  Angle = 360
  AttacherType = Attacher::AttachEngine3D
  Height = 7
  Placement = pos=(0,0,-1.5) rot=(0,0,1;0rad)
  Radius = 13.5
FEATURE [Part::Cylinder] Cylinder014005097  label="Válec101"
  Angle = 360
  AttacherType = Attacher::AttachEngine3D
  Height = 7
  Radius = 2.6
FEATURE [Part::MultiFuse] Fusion068
  Placement = pos=(0,0,1) rot=(0,0,1;0rad)
  Shapes = -> [Fusion063,Cylinder014005097]
FEATURE [Part::Cylinder] Cylinder014005100  label="unasec spodek011"
  Angle = 360
  AttacherType = Attacher::AttachEngine3D
  Height = 1.5
  Placement = pos=(0,0,-1.5) rot=(0,0,1;0rad)
  Radius = 15.5
FEATURE [Part::MultiFuse] Fusion058
  Shapes = -> [Cylinder014005099,Cylinder014005100]
FEATURE [Part::Cut] Cut044  label="unasec spodek010"
  Base = -> Fusion058
  Tool = -> Fusion059
FEATURE [Part::Cut] Cut050  label="Uasec spodek005"
  Base = -> Cut044
  Tool = -> Fusion065
FEATURE [Part::MultiFuse] Fusion064  label="Unasec spdek final004"
  Shapes = -> [Cut050,Fusion062]
FEATURE [Part::Cylinder] Cylinder014005113  label="Válec115"
  Angle = 360
  AttacherType = Attacher::AttachEngine3D
  Height = 1.5
  Radius = 16
FEATURE [Part::Cut] Cut043  label="Ring010"
  Base = -> Cylinder014005112
  Placement = pos=(0,0,5.5) rot=(0,0,1;0rad)
  Tool = -> Cylinder014005113
FEATURE [Part::MultiFuse] Fusion061  label="Ring zaklad Fin004"
  Shapes = -> [Cut045,Cut043,Cut046]
FEATURE [Part::MultiFuse] Fusion060  label="teloII003"
  Shapes = -> [Fusion061,Extrude004]
FEATURE [Part::Cylinder] Cylinder014005115  label="Unasec vrch006"
  Angle = 360
  AttacherType = Attacher::AttachEngine3D
  Height = 1.5
  Placement = pos=(0,0,5.5) rot=(0,0,1;0rad)
  Radius = 15.5
FEATURE [Part::Cut] Cut049  label="unasec vrch006"
  Base = -> Cylinder014005115
  Tool = -> Fusion066
FEATURE [Part::Cut] Cut048  label="Unasec Vrch zaklad006"
  Base = -> Cut049
  Tool = -> Fusion068
FEATURE [Part::Cylinder] Cylinder014005116  label="Válec117"
  Angle = 360
  AttacherType = Attacher::AttachEngine3D
  Height = 4
  Placement = pos=(0,0,7) rot=(0,0,1;0rad)
  Radius = 6.5
FEATURE [Part::MultiFuse] Fusion067  label="unasec vrhch 006"
  Shapes = -> [Cut048,Cut007_solid005,Cylinder014005116]
FEATURE [Part::Cut] Cut047  label="Unasec + Sun004"
  Base = -> Fusion067
  Tool = -> Cylinder014005117
FEATURE [App::Part] Part004
  Group = -> [Cut044,Cut050,Cylinder014005098,Cylinder014005100,Cylinder014005099,Cylinder014005101,Cylinder014005105,Cylinder014005108,Cylinder014005109,Screw_solid034,Cylinder014005104,Screw_solid038,Cylinder014005102,Screw_solid036,Fusion059,Fusion058,Fusion065,Fusion062,Fusion064,Cut008_solid014,Cut008_solid012,Cut008_solid013,Screw_solid033,Cylinder014005107,Cylinder014005103,Screw_solid037,Screw_solid035,+26 more]
  License = CC BY 3.0
  LicenseURL = http://creativecommons.org/licenses/by/3.0/
  Origin = -> Origin004
  Placement = pos=(0,0,31.5) rot=(0,0,1;0rad)
FEATURE [Part::Cylinder] Cylinder014005120  label="Válec121"
  Angle = 360
  AttacherType = Attacher::AttachEngine3D
  Height = 5.5
  Radius = 20
FEATURE [Part::Cut] Cut051  label="ring 006"
  Base = -> Cylinder014005120
  Tool = -> InvoluteGear013
FEATURE [Part::Cylinder] Cylinder014005123  label="Válec124"
  Angle = 360
  AttacherType = Attacher::AttachEngine3D
  Height = 1.5
  Radius = 16
FEATURE [Part::Cylinder] Cylinder014005127  label="Válec127"
  Angle = 360
  AttacherType = Attacher::AttachEngine3D
  Height = 18
  Radius = 2.6
FEATURE [Part::Cylinder] Cylinder014005124  label="Válec125"
  Angle = 360
  AttacherType = Attacher::AttachEngine3D
  Height = 1.5
  Radius = 20
FEATURE [Part::Cut] Cut053  label="Ring012"
  Base = -> Cylinder014005124
  Placement = pos=(0,0,-1.5) rot=(0,0,1;0rad)
  Tool = -> Cylinder014005123
FEATURE [Part::MultiFuse] Fusion076  label="Ring zaklad Fin005"
  Shapes = -> [Cut051,Cut054,Cut053]
FEATURE [Part::Cylinder] Cylinder014005125  label="Unasec vrch007"
  Angle = 360
  AttacherType = Attacher::AttachEngine3D
  Height = 1.5
  Placement = pos=(0,0,5.5) rot=(0,0,1;0rad)
  Radius = 15.5
FEATURE [Part::Cylinder] Cylinder014005133  label="unasec stred006"
  Angle = 360
  AttacherType = Attacher::AttachEngine3D
  Height = 7
  Placement = pos=(0,0,-1.5) rot=(0,0,1;0rad)
  Radius = 13.5
FEATURE [Part::Cylinder] Cylinder014005122  label="Válec123"
  Angle = 360
  AttacherType = Attacher::AttachEngine3D
  Height = 10
  Placement = pos=(10.5,0,0) rot=(0,0,1;0rad)
  Radius = 8
FEATURE [Part::Cylinder] Cylinder014005126  label="Válec126"
  Angle = 360
  AttacherType = Attacher::AttachEngine3D
  Height = 4
  Placement = pos=(0,0,7) rot=(0,0,1;0rad)
  Radius = 6.5
FEATURE [Part::Cylinder] Cylinder014005134  label="unasec spodek013"
  Angle = 360
  AttacherType = Attacher::AttachEngine3D
  Height = 1.5
  Placement = pos=(0,0,-1.5) rot=(0,0,1;0rad)
  Radius = 15.5
FEATURE [Part::MultiFuse] Fusion077
  Shapes = -> [Cylinder014005133,Cylinder014005134]
FEATURE [Part::Feature] Cylinder014005131  label="Válec131"
  Placement = pos=(0,0,0) rot=(0,0,1;4.18879rad)
  shape: bbox 16 x 16 x 10 mm, 3 faces (baked)
FEATURE [Part::Feature] Cylinder014005138  label="Válec136"
  Placement = pos=(0,0,0) rot=(0,0,1;2.0944rad)
  shape: bbox 16 x 16 x 10 mm, 3 faces (baked)
FEATURE [Part::Feature] Screw_solid044  label="M2x4-Screw (Solid)044"
  Placement = pos=(0,0,0) rot=(0,0,1;1.0472rad)
  shape: bbox 3.6 x 3.6 x 4 mm, 12 faces (baked)
FEATURE [Part::Feature] Screw_solid043  label="M2x4-Screw (Solid)043"
  Placement = pos=(0,0,0) rot=(0,0,-1;1.0472rad)
  shape: bbox 3.6 x 3.6 x 4 mm, 12 faces (baked)
FEATURE [Part::Feature] Screw_solid042  label="M2x4-Screw (Solid)042"
  Placement = pos=(0,0,0) rot=(0,0,1;3.14159rad)
  shape: bbox 3.6 x 3.6 x 4 mm, 12 faces (baked)
FEATURE [Part::Feature] Screw_solid047  label="M2x4-Screw (Solid)047"
  Placement = pos=(0,0,0) rot=(0,0,-1;1.0472rad)
  shape: bbox 3.6 x 3.6 x 4 mm, 12 faces (baked)
FEATURE [Part::Feature] Cylinder014005128  label="Válec128"
  Placement = pos=(0,0,0) rot=(0,0,1;2.0944rad)
  shape: bbox 5 x 5 x 7 mm, 3 faces (baked)
FEATURE [Part::Feature] Cylinder014005129  label="Válec129"
  shape: bbox 5 x 5 x 7 mm, 3 faces (baked)
FEATURE [Part::Feature] Cut008_solid017  label="Planet018"
  shape: bbox 12.9 x 13.1 x 5 mm, 57 faces (baked)
FEATURE [Part::Feature] Cut061001  label="SUN I Final"
  shape: bbox 24 x 24 x 12.25 mm, 99 faces (baked)
FEATURE [App::Part] Part001
  Group = -> [Cut008_solid,Cut008_solid001,Cut008_solid002,Cylinder010,Cylinder,Cylinder013,Fusion001,Fusion002,Cylinder014005006,Cylinder014005005,Cylinder014002,Cylinder014001,Cylinder014005004,Cylinder011,Cut004,Cut006,Screw_solid005,Screw_solid003,Screw_solid004,Fusion006,Fusion004,Fusion008,Cylinder014005034,Cylinder014005035,Cut007_solid001,Cut012,Cut011,Screw_solid007,Screw_solid008,Cylinder014005014,+29 more]
  License = CC BY 3.0
  LicenseURL = http://creativecommons.org/licenses/by/3.0/
  Origin = -> Origin001
FEATURE [Part::Feature] Screw_solid045  label="M2x4-Screw (Solid)045"
  Placement = pos=(0,0,0) rot=(0,0,1;3.14159rad)
  shape: bbox 3.6 x 3.6 x 4 mm, 12 faces (baked)
FEATURE [Part::Feature] Cylinder014005130  label="Válec130"
  Placement = pos=(0,0,0) rot=(0,0,1;4.18879rad)
  shape: bbox 5 x 5 x 7 mm, 3 faces (baked)
FEATURE [Part::Feature] Screw_solid046  label="M2x4-Screw (Solid)046"
  Placement = pos=(0,0,0) rot=(0,0,1;1.0472rad)
  shape: bbox 3.6 x 3.6 x 4 mm, 12 faces (baked)
FEATURE [Part::MultiFuse] Fusion085  label="srouby016"
  Placement = pos=(0,0,0.5) rot=(0,0,1;0rad)
  Shapes = -> [Screw_solid046,Screw_solid047,Screw_solid045]
FEATURE [Part::Feature] Screw_solid040  label="M2x4-Screw (Solid)040"
  Placement = pos=(0,0,0) rot=(0,0,1;3.14159rad)
  shape: bbox 3.6 x 3.6 x 4 mm, 12 faces (baked)
FEATURE [Part::Feature] Cylinder014005132  label="Válec132"
  Placement = pos=(0,0,0) rot=(0,0,1;4.18879rad)
  shape: bbox 5 x 5 x 7 mm, 3 faces (baked)
FEATURE [Part::MultiFuse] Fusion075
  Shapes = -> [Cylinder014005132,Cylinder014005118,Cylinder014005128]
FEATURE [Part::Feature] Cut008_solid015  label="Planet016"
  Placement = pos=(0,0,0) rot=(0,0,1;2.0944rad)
  shape: bbox 12.9 x 13.1 x 5 mm, 57 faces (baked)
FEATURE [Part::Feature] Screw_solid041  label="M2x4-Screw (Solid)041"
  Placement = pos=(0,0,0) rot=(0,0,-1;1.0472rad)
  shape: bbox 3.6 x 3.6 x 4 mm, 12 faces (baked)
FEATURE [Part::MultiFuse] Fusion073  label="srouby015"
  Shapes = -> [Screw_solid044,Screw_solid041,Screw_solid042]
FEATURE [Part::Feature] Cut008_solid016  label="Planet017"
  Placement = pos=(0,0,0) rot=(0,0,1;4.18879rad)
  shape: bbox 12.9 x 13.1 x 5 mm, 57 faces (baked)
FEATURE [Part::Feature] Cylinder014005137  label="Válec135"
  Placement = pos=(0,0,0) rot=(0,0,1;2.0944rad)
  shape: bbox 5 x 5 x 7 mm, 3 faces (baked)
FEATURE [Part::MultiFuse] Fusion072
  Shapes = -> [Cylinder014005130,Cylinder014005129,Cylinder014005137]
FEATURE [Part::Feature] Cylinder014005149  label="Válec146"
  Placement = pos=(0,0,0) rot=(0,0,1;2.0944rad)
  shape: bbox 5 x 5 x 7 mm, 3 faces (baked)
FEATURE [Part::Feature] Cylinder014005150  label="Válec147"
  shape: bbox 5 x 5 x 7 mm, 3 faces (baked)
FEATURE [Part::Feature] Screw_solid039  label="M2x4-Screw (Solid)039"
  Placement = pos=(0,0,0) rot=(0,0,1;1.0472rad)
  shape: bbox 3.6 x 3.6 x 4 mm, 12 faces (baked)
FEATURE [Part::MultiFuse] Fusion071  label="srouby014"
  Placement = pos=(0,0,0.5) rot=(0,0,1;0rad)
  Shapes = -> [Screw_solid039,Screw_solid043,Screw_solid040]
FEATURE [Part::Cut] Cut057  label="unasec vrch007"
  Base = -> Cylinder014005125
  Tool = -> Fusion071
FEATURE [Part::Feature] Cut005_solid001_cs006
  Placement = pos=(0,0,-11.25) rot=(0,0,1;0rad)
  shape: bbox 41 x 41 x 3e-07 mm, 0 faces, 0 solids (baked)
FEATURE [Part::Extrusion] Extrude005  label="box005"
  Base = -> Cut005_solid001_cs006
  Dir = (0,0,1)
  DirMode = 2
  FaceMakerClass = Part::FaceMakerBullseye
  LengthFwd = 10.5
  LengthRev = 0
  Placement = pos=(0,0,-3) rot=(0,0,1;0rad)
  Solid = true
  Symmetric = false
FEATURE [Part::MultiFuse] Fusion078  label="teloII004"
  Shapes = -> [Fusion076,Extrude005]
FEATURE [Part::Cylinder] Cylinder014005135  label="Válec133"
  Angle = 360
  AttacherType = Attacher::AttachEngine3D
  Height = 7
  Radius = 2.6
FEATURE [Part::MultiFuse] Fusion079
  Placement = pos=(0,0,1) rot=(0,0,1;0rad)
  Shapes = -> [Fusion075,Cylinder014005135]
FEATURE [Part::Cylinder] Cylinder014005136  label="Válec134"
  Angle = 360
  AttacherType = Attacher::AttachEngine3D
  Height = 10
  Placement = pos=(0,0,-3) rot=(0,0,1;0rad)
  Radius = 7
FEATURE [Part::MultiFuse] Fusion069
  Shapes = -> [Cylinder014005136,Cylinder014005122,Cylinder014005131,Cylinder014005138]
FEATURE [Part::Cut] Cut052  label="unasec spodek012"
  Base = -> Fusion077
  Tool = -> Fusion069
FEATURE [Part::Cut] Cut056  label="Uasec spodek006"
  Base = -> Cut052
  Tool = -> Fusion073
FEATURE [Part::MultiFuse] Fusion074  label="Unasec spdek final005"
  Shapes = -> [Cut056,Fusion072]
FEATURE [Part::Cut] Cut058  label="Unasec Vrch zaklad007"
  Base = -> Cut057
  Tool = -> Fusion079
FEATURE [Part::MultiFuse] Fusion070  label="unasec vrhch 007"
  Shapes = -> [Cut058,Cut007_solid006,Cylinder014005126]
FEATURE [Part::Cut] Cut055  label="Unasec + Sun005 old"
  Base = -> Fusion070
  Tool = -> Cylinder014005127
FEATURE [Part::Cylinder] Cylinder014005148  label="Válec145"
  Angle = 360
  AttacherType = Attacher::AttachEngine3D
  Height = 22
  Radius = 2.6
FEATURE [Part::MultiFuse] Fusion090
  Shapes = -> [Cylinder014005148,Extrude007]
FEATURE [Part::Cylinder] Cylinder014005147  label="Válec144"
  Angle = 360
  AttacherType = Attacher::AttachEngine3D
  Height = 6
  Placement = pos=(0,0,7) rot=(0,0,1;0rad)
  Radius = 6.5
FEATURE [Part::Cylinder] Cylinder014005145  label="Válec143"
  Angle = 360
  AttacherType = Attacher::AttachEngine3D
  Height = 7
  Radius = 2.6
FEATURE [Part::Cylinder] Cylinder014005146  label="Unasec vrch008"
  Angle = 360
  AttacherType = Attacher::AttachEngine3D
  Height = 1.5
  Placement = pos=(0,0,5.5) rot=(0,0,1;0rad)
  Radius = 15.5
FEATURE [Part::Cut] Cut061004  label="unasec vrch008"
  Base = -> Cylinder014005146
  Tool = -> Fusion085
FEATURE [Part::Feature] Cylinder014005151  label="Válec148"
  Placement = pos=(0,0,0) rot=(0,0,1;4.18879rad)
  shape: bbox 5 x 5 x 7 mm, 3 faces (baked)
FEATURE [Part::MultiFuse] Fusion087
  Shapes = -> [Cylinder014005151,Cylinder014005150,Cylinder014005149]
FEATURE [Part::MultiFuse] Fusion088
  Placement = pos=(0,0,1) rot=(0,0,1;0rad)
  Shapes = -> [Fusion087,Cylinder014005145]
FEATURE [Part::Cut] Cut061003  label="Unasec Vrch zaklad008"
  Base = -> Cut061004
  Tool = -> Fusion088
FEATURE [Part::MultiFuse] Fusion089
  Shapes = -> [Cut061003,Cylinder014005147,Extrude006]
FEATURE [Part::Cut] Cut061005  label="unasec top"
  Base = -> Fusion089
  Tool = -> Fusion090
FEATURE [App::Part] Part005
  Group = -> [Cut052,Cut056,Cylinder014005136,Cylinder014005134,Cylinder014005133,Cylinder014005122,Cylinder014005131,Cylinder014005137,Cylinder014005138,Screw_solid042,Cylinder014005129,Screw_solid044,Cylinder014005130,Screw_solid041,Fusion069,Fusion077,Fusion073,Fusion072,Fusion074,Cut008_solid017,Cut008_solid015,Cut008_solid016,Screw_solid039,Cylinder014005118,Cylinder014005128,Screw_solid043,Screw_solid040,+48 more]
  License = CC BY 3.0
  LicenseURL = http://creativecommons.org/licenses/by/3.0/
  Origin = -> Origin005
  Placement = pos=(0,0,42) rot=(0,0,1;0rad)
FEATURE [App::Part] Part007  label="GearBOX 1024:1a"
  Group = -> [Part001,Part,Part002,Part004,Part005]
  License = CC BY 3.0
  LicenseURL = http://creativecommons.org/licenses/by/3.0/
  Origin = -> Origin007
FEATURE [Part::Box] Box009  label="Krychle008"
  AttacherType = Attacher::AttachEngine3D
  Height = 40
  Length = 41
  Placement = pos=(-20.5,-20.5,0) rot=(0,0,1;0rad)
  Width = 41
FEATURE [Part::Cylinder] Cylinder003  label="Válec003"
  Angle = 360
  AttacherType = Attacher::AttachEngine3D
  Height = 50
  Placement = pos=(-15.5,15.5,0) rot=(0,0,1;0rad)
  Radius = 1.6
FEATURE [Part::Cylinder] Cylinder002  label="Válec002"
  Angle = 360
  AttacherType = Attacher::AttachEngine3D
  Height = 50
  Placement = pos=(15.5,15.5,0) rot=(0,0,1;0rad)
  Radius = 1.6
FEATURE [Part::Cylinder] Cylinder014005153  label="Válec150"
  Angle = 360
  AttacherType = Attacher::AttachEngine3D
  Height = 50
  Placement = pos=(-15.5,-15.5,0) rot=(0,0,1;0rad)
  Radius = 1.6
FEATURE [Part::Cylinder] Cylinder004  label="Válec004"
  Angle = 360
  AttacherType = Attacher::AttachEngine3D
  Height = 50
  Placement = pos=(15.5,-15.5,0) rot=(0,0,1;0rad)
  Radius = 1.6
FEATURE [Part::MultiFuse] Fusion091  label="diry"
  Shapes = -> [Cylinder003,Cylinder002,Cylinder014005153,Cylinder004]
FEATURE [Part::Chamfer] Chamfer
  Base = -> Box009
  Edges = 4 edges r=5: [Edge1,Edge3,Edge5,Edge7]
FEATURE [Part::Cut] Cut061006
  Base = -> Chamfer
  Tool = -> Fusion091
FEATURE [App::Part] Part008  label="NEAM17  motor- 40mm"
  Group = -> [Chamfer,Fusion091,Box009,Cylinder003,Cylinder002,Cylinder014005153,Cylinder004,Cut061006]
  License = CC BY 3.0
  LicenseURL = http://creativecommons.org/licenses/by/3.0/
  Origin = -> Origin008
  Placement = pos=(0,0,-51.5) rot=(0,0,1;0rad)
FEATURE [Part::Box] Box010  label="Krychle009"
  AttacherType = Attacher::AttachEngine3D
  Height = 10
  Length = 43
  Placement = pos=(-21.5,-20.5,0) rot=(0,0,1;0rad)
  Width = 42
FEATURE [Part::Chamfer] Chamfer001
  Base = -> Box010
  Edges = 2 edges r=5: [Edge1,Edge5]
FEATURE [Part::Cylinder] Cylinder014005154  label="Válec151"
  Angle = 360
  AttacherType = Attacher::AttachEngine3D
  Height = 50
  Placement = pos=(-15.5,15.5,0) rot=(0,0,1;0rad)
  Radius = 1.6
FEATURE [Part::Cylinder] Cylinder014005155  label="Válec152"
  Angle = 360
  AttacherType = Attacher::AttachEngine3D
  Height = 50
  Placement = pos=(15.5,15.5,0) rot=(0,0,1;0rad)
  Radius = 1.6
FEATURE [Part::Cylinder] Cylinder014005156  label="dira stred001"
  Angle = 360
  AttacherType = Attacher::AttachEngine3D
  Height = 50
  Radius = 13
FEATURE [Part::Cylinder] Cylinder014005157  label="Válec153"
  Angle = 360
  AttacherType = Attacher::AttachEngine3D
  Height = 50
  Placement = pos=(-15.5,-15.5,0) rot=(0,0,1;0rad)
  Radius = 1.6
FEATURE [Part::Cylinder] Cylinder014005158  label="Válec154"
  Angle = 360
  AttacherType = Attacher::AttachEngine3D
  Height = 50
  Placement = pos=(15.5,-15.5,0) rot=(0,0,1;0rad)
  Radius = 1.6
FEATURE [Part::MultiFuse] Fusion092  label="diry001"
  Shapes = -> [Cylinder014005154,Cylinder014005155,Cylinder014005156,Cylinder014005157,Cylinder014005158]
FEATURE [Part::Cut] Cut061007  label="Horni ucjyt"
  Base = -> Chamfer001
  Placement = pos=(0,0,49.5) rot=(0,0,1;0rad)
  Tool = -> Fusion092
FEATURE [Part::Cylinder] Cylinder014005159  label="Válec155"
  Angle = 360
  AttacherType = Attacher::AttachEngine3D
  Height = 50
  Placement = pos=(15.5,-15.5,0) rot=(0,0,1;0rad)
  Radius = 1.6
FEATURE [Part::Cylinder] Cylinder014005160  label="Válec156"
  Angle = 360
  AttacherType = Attacher::AttachEngine3D
  Height = 50
  Placement = pos=(-15.5,-15.5,0) rot=(0,0,1;0rad)
  Radius = 1.6
FEATURE [Part::Box] Box011  label="Krychle010"
  AttacherType = Attacher::AttachEngine3D
  Height = 10
  Length = 41
  Placement = pos=(-20.5,-20.5,0) rot=(0,0,1;0rad)
  Width = 41
FEATURE [Part::Chamfer] Chamfer002
  Base = -> Box011
  Edges = 4 edges r=5: [Edge1,Edge3,Edge5,Edge7]
FEATURE [Part::Cylinder] Cylinder014005161  label="Válec157"
  Angle = 360
  AttacherType = Attacher::AttachEngine3D
  Height = 50
  Placement = pos=(-15.5,15.5,0) rot=(0,0,1;0rad)
  Radius = 1.6
FEATURE [Part::Cylinder] Cylinder014005162  label="dira stred002"
  Angle = 360
  AttacherType = Attacher::AttachEngine3D
  Height = 50
  Radius = 12
FEATURE [Part::Cylinder] Cylinder014005163  label="Válec158"
  Angle = 360
  AttacherType = Attacher::AttachEngine3D
  Height = 50
  Placement = pos=(15.5,15.5,0) rot=(0,0,1;0rad)
  Radius = 1.6
FEATURE [Part::MultiFuse] Fusion093  label="diry002"
  Shapes = -> [Cylinder014005161,Cylinder014005163,Cylinder014005162,Cylinder014005160,Cylinder014005159]
FEATURE [Part::Cut] Cut061008
  Base = -> Chamfer002
  Tool = -> Fusion093
FEATURE [App::Part] Part010  label="Distance001"
  Group = -> [Chamfer002,Fusion093,Box011,Cylinder014005161,Cylinder014005163,Cylinder014005162,Cylinder014005160,Cylinder014005159,Cut061008]
  License = CC BY 3.0
  LicenseURL = http://creativecommons.org/licenses/by/3.0/
  Origin = -> Origin010
  Placement = pos=(0,0,49.5) rot=(0,0,1;0rad)
FEATURE [Part::Box] Box  label="deska"
  AttacherType = Attacher::AttachEngine3D
  Height = 111
  Length = 43
  Placement = pos=(-21.5,21.5,-51.5) rot=(0,0,1;0rad)
  Width = 10
FEATURE [Part::Box] Box012  label="deska001"
  AttacherType = Attacher::AttachEngine3D
  Height = 111
  Length = 9
  Placement = pos=(-30.5,-14.5,-51.5) rot=(0,0,1;0rad)
  Width = 46
FEATURE [Part::Box] Box013  label="deska002"
  AttacherType = Attacher::AttachEngine3D
  Height = 111
  Length = 9
  Placement = pos=(21.5,-14.5,-51.5) rot=(0,0,1;0rad)
  Width = 46
FEATURE [Part::MultiFuse] Fusion094  label="motor drazak"
  Shapes = -> [Cut061007,Box013,Box,Box012]
FEATURE [Part::Box] Box014  label="Krychle"
  AttacherType = Attacher::AttachEngine3D
  Height = 112
  Length = 38
  Placement = pos=(-19,32,-52) rot=(0,0,1;0rad)
  Width = 10
FEATURE [Part::Box] Box015  label="Krychle011"
  AttacherType = Attacher::AttachEngine3D
  Height = 112
  Length = 38
  Placement = pos=(-19,34,-52) rot=(0,0,1;0rad)
  Width = 6
FEATURE [Part::Cut] Cut061009
  Base = -> Box014
  Tool = -> Box015
FEATURE [Sketcher::SketchObject] Sketch
  MapMode = 5
  Placement = pos=(0,0,60) rot=(0,0,1;0rad)
  sketch-geometry (6):
    g0: LineSegment StartX=-18.9734 StartY=34.0308 StartZ=0 EndX=-16.0253 EndY=36.9748 EndZ=0
    g1: LineSegment StartX=18.996 StartY=34.0308 StartZ=0 EndX=16.044 EndY=36.9748 EndZ=0
    g2: LineSegment StartX=18.996 StartY=34.0308 StartZ=0 EndX=-18.9734 EndY=34.0308 EndZ=0
    g3: LineSegment StartX=-18.9734 StartY=40.0311 StartZ=0 EndX=-16.0253 EndY=36.9748 EndZ=0
    g4: LineSegment StartX=16.044 StartY=36.9748 StartZ=0 EndX=18.9109 EndY=40.0311 EndZ=0
    g5: LineSegment StartX=-18.9734 StartY=40.0311 StartZ=0 EndX=18.9109 EndY=40.0311 EndZ=0
  constraints (7):
    c: Coincident(g2,g1)
    c: Coincident(g2,g0)
    c: Horizontal(g2)
    c: Coincident(g3,g0)
    c: Coincident(g5,g3)
    c: Coincident(g5,g4)
    c: Horizontal(g5)
FEATURE [Part::Extrusion] Extrude009
  Base = -> Sketch
  Dir = (0,0,1)
  DirMode = 2
  FaceMakerClass = Part::FaceMakerBullseye
  LengthFwd = -112
  LengthRev = 0
  Solid = true
  Symmetric = false
FEATURE [Part::MultiFuse] Fusion095  label="Arca plate base"
  Placement = pos=(0,-0.5,0) rot=(0,0,1;0rad)
  Shapes = -> [Extrude009,Cut061009]
FEATURE [Part::Box] Box016  label="Krychle012"
  AttacherType = Attacher::AttachEngine3D
  Height = 112
  Length = 38
  Placement = pos=(-19,32,-52) rot=(0,0,1;0rad)
  Width = 10
FEATURE [Part::Box] Box017  label="Krychle013"
  AttacherType = Attacher::AttachEngine3D
  Height = 112
  Length = 38
  Placement = pos=(-19,34,-52) rot=(0,0,1;0rad)
  Width = 6
FEATURE [Part::Cut] Cut061010
  Base = -> Box016
  Tool = -> Box017
FEATURE [Sketcher::SketchObject] Sketch002
  MapMode = 5
  Placement = pos=(0,0,60) rot=(0,0,1;0rad)
  sketch-geometry (6):
    g0: LineSegment StartX=-18.9734 StartY=34.0308 StartZ=0 EndX=-16.0253 EndY=36.9748 EndZ=0
    g1: LineSegment StartX=18.996 StartY=34.0308 StartZ=0 EndX=16.044 EndY=36.9748 EndZ=0
    g2: LineSegment StartX=18.996 StartY=34.0308 StartZ=0 EndX=-18.9734 EndY=34.0308 EndZ=0
    g3: LineSegment StartX=-18.9734 StartY=40.0311 StartZ=0 EndX=-16.0253 EndY=36.9748 EndZ=0
    g4: LineSegment StartX=16.044 StartY=36.9748 StartZ=0 EndX=18.9109 EndY=40.0311 EndZ=0
    g5: LineSegment StartX=-18.9734 StartY=40.0311 StartZ=0 EndX=18.9109 EndY=40.0311 EndZ=0
  constraints (7):
    c: Coincident(g2,g1)
    c: Coincident(g2,g0)
    c: Horizontal(g2)
    c: Coincident(g3,g0)
    c: Coincident(g5,g3)
    c: Coincident(g5,g4)
    c: Horizontal(g5)
FEATURE [Part::Extrusion] Extrude010
  Base = -> Sketch002
  Dir = (0,0,1)
  DirMode = 2
  FaceMakerClass = Part::FaceMakerBullseye
  LengthFwd = -112
  LengthRev = 0
  Solid = true
  Symmetric = false
FEATURE [Part::MultiFuse] Fusion096  label="Arca plate base001"
  Placement = pos=(0,-0.5,0) rot=(0,0,1;0rad)
  Shapes = -> [Extrude010,Cut061010]
FEATURE [Part::Cylinder] Cylinder014005164  label="Válec159"
  Angle = 360
  AttacherType = Attacher::AttachEngine3D
  Height = 200
  Placement = pos=(0,27,-100) rot=(0,0,1;0rad)
  Radius = 3.2
FEATURE [Part::FeaturePython] Nut  label="M6-Nut"  # Fasteners workbench fastener (typed FeaturePython)
  Placement = pos=(0,27,56) rot=(0,0,1;0rad)
  diameter = 8
  invert = false
  matchOuter = false
  offset = 0
  thread = false
  type = 1
FEATURE [Part::FeaturePython] Nut001  label="M6-Nut001"  # Fasteners workbench fastener (typed FeaturePython)
  Placement = pos=(0,27,-52) rot=(0,0,1;0rad)
  diameter = 8
  invert = false
  matchOuter = false
  offset = 0
  thread = false
  type = 1
FEATURE [Part::MultiFuse] Fusion097  label="Dira zavazi"
  Shapes = -> [Cylinder014005164,Nut,Nut001]
FEATURE [Part::Cylinder] Cylinder014005165  label="Válec160"
  Angle = 360
  AttacherType = Attacher::AttachEngine3D
  Height = 10
  Placement = pos=(0,43,54.5) rot=(1,0,0;1.5708rad)
  Radius = 4
FEATURE [Part::Cylinder] Cylinder014005166  label="Válec161"
  Angle = 360
  AttacherType = Attacher::AttachEngine3D
  Height = 10
  Placement = pos=(0,43,-47) rot=(1,0,0;1.5708rad)
  Radius = 4
FEATURE [Part::MultiFuse] Fusion098  label="drzak s arca"
  Shapes = -> [Fusion094,Fusion096,Cylinder014005165,Cylinder014005166]
FEATURE [Part::Cylinder] Cylinder014005167  label="Válec162"
  Angle = 360
  AttacherType = Attacher::AttachEngine3D
  Height = 65
  Placement = pos=(-32,0,0) rot=(0,1,0;1.5708rad)
  Radius = 1.25
FEATURE [Part::Cylinder] Cylinder014005168  label="Válec163"
  Angle = 360
  AttacherType = Attacher::AttachEngine3D
  Height = 65
  Placement = pos=(-32,0,42) rot=(0,1,0;1.5708rad)
  Radius = 1.25
FEATURE [Part::Cylinder] Cylinder014005169  label="Válec164"
  Angle = 360
  AttacherType = Attacher::AttachEngine3D
  Height = 65
  Placement = pos=(-32,0,-27) rot=(0,1,0;1.5708rad)
  Radius = 1.25
FEATURE [Part::MultiFuse] Fusion099  label="diry 2,5"
  Shapes = -> [Cylinder014005167,Cylinder014005168,Cylinder014005169]
FEATURE [Part::MultiFuse] Fusion100  label="diry003"
  Shapes = -> [Fusion097,Fusion099]
FEATURE [Part::Cut] Cut061011  label="Drzak s dirama"
  Base = -> Fusion098
  Tool = -> Fusion100
FEATURE [Part::Chamfer] Chamfer003  label="Axsix1"
  Base = -> Cut061011
  Edges = 4 edges r=8: [Edge131,Edge134,Edge187,Edge191]
  Placement = pos=(0,0,0) rot=(0,0,1;3.14159rad)
FEATURE [Part::Cylinder] Cylinder014005170  label="dira stred003"
  Angle = 360
  AttacherType = Attacher::AttachEngine3D
  Height = 50
  Radius = 13
FEATURE [Part::Cylinder] Cylinder014005171  label="Válec165"
  Angle = 360
  AttacherType = Attacher::AttachEngine3D
  Height = 50
  Placement = pos=(-15.5,-15.5,0) rot=(0,0,1;0rad)
  Radius = 1.6
FEATURE [Part::Cylinder] Cylinder014005172  label="Válec166"
  Angle = 360
  AttacherType = Attacher::AttachEngine3D
  Height = 50
  Placement = pos=(15.5,-15.5,0) rot=(0,0,1;0rad)
  Radius = 1.6
FEATURE [Part::Cylinder] Cylinder014005173  label="Válec167"
  Angle = 360
  AttacherType = Attacher::AttachEngine3D
  Height = 50
  Placement = pos=(-15.5,15.5,0) rot=(0,0,1;0rad)
  Radius = 1.6
FEATURE [Part::Cylinder] Cylinder014005174  label="Válec168"
  Angle = 360
  AttacherType = Attacher::AttachEngine3D
  Height = 50
  Placement = pos=(15.5,15.5,0) rot=(0,0,1;0rad)
  Radius = 1.6
FEATURE [Part::Box] Box018  label="Krychle014"
  AttacherType = Attacher::AttachEngine3D
  Height = 10
  Length = 43
  Placement = pos=(-21.5,-20.5,0) rot=(0,0,1;0rad)
  Width = 42
FEATURE [Part::Chamfer] Chamfer004
  Base = -> Box018
  Edges = 2 edges r=5: [Edge1,Edge5]
FEATURE [Part::MultiFuse] Fusion102  label="diry004"
  Shapes = -> [Cylinder014005173,Cylinder014005174,Cylinder014005170,Cylinder014005171,Cylinder014005172]
FEATURE [Part::Cut] Cut061012  label="Horni ucjyt001"
  Base = -> Chamfer004
  Placement = pos=(0,0,49.5) rot=(0,0,1;0rad)
  Tool = -> Fusion102
FEATURE [Part::Box] Box019  label="deska003"
  AttacherType = Attacher::AttachEngine3D
  Height = 111
  Length = 9
  Placement = pos=(-30.5,-14.5,-51.5) rot=(0,0,1;0rad)
  Width = 46
FEATURE [Part::Box] Box020  label="deska004"
  AttacherType = Attacher::AttachEngine3D
  Height = 111
  Length = 9
  Placement = pos=(21.5,-14.5,-51.5) rot=(0,0,1;0rad)
  Width = 46
FEATURE [Part::Box] Box021  label="deska005"
  AttacherType = Attacher::AttachEngine3D
  Height = 111
  Length = 43
  Placement = pos=(-21.5,21.5,-51.5) rot=(0,0,1;0rad)
  Width = 10
FEATURE [Part::MultiFuse] Fusion101  label="motor drazak001"
  Shapes = -> [Cut061012,Box020,Box021,Box019]
FEATURE [Sketcher::SketchObject] Sketch003
  MapMode = 5
  Placement = pos=(0,0,60) rot=(0,0,1;0rad)
  sketch-geometry (6):
    g0: LineSegment StartX=-18.9734 StartY=34.0308 StartZ=0 EndX=-16.0253 EndY=36.9748 EndZ=0
    g1: LineSegment StartX=18.996 StartY=34.0308 StartZ=0 EndX=16.044 EndY=36.9748 EndZ=0
    g2: LineSegment StartX=18.996 StartY=34.0308 StartZ=0 EndX=-18.9734 EndY=34.0308 EndZ=0
    g3: LineSegment StartX=-18.9734 StartY=40.0311 StartZ=0 EndX=-16.0253 EndY=36.9748 EndZ=0
    g4: LineSegment StartX=16.044 StartY=36.9748 StartZ=0 EndX=18.9109 EndY=40.0311 EndZ=0
    g5: LineSegment StartX=-18.9734 StartY=40.0311 StartZ=0 EndX=18.9109 EndY=40.0311 EndZ=0
  constraints (7):
    c: Coincident(g2,g1)
    c: Coincident(g2,g0)
    c: Horizontal(g2)
    c: Coincident(g3,g0)
    c: Coincident(g5,g3)
    c: Coincident(g5,g4)
    c: Horizontal(g5)
FEATURE [Part::Extrusion] Extrude011
  Base = -> Sketch003
  Dir = (0,0,1)
  DirMode = 2
  FaceMakerClass = Part::FaceMakerBullseye
  LengthFwd = -112
  LengthRev = 0
  Solid = true
  Symmetric = false
FEATURE [Part::FeaturePython] Nut002  label="M6-Nut002"  # Fasteners workbench fastener (typed FeaturePython)
  Placement = pos=(0,27,56) rot=(0,0,1;0rad)
  diameter = 8
  invert = false
  matchOuter = false
  offset = 0
  thread = false
  type = 1
FEATURE [Part::FeaturePython] Nut003  label="M6-Nut003"  # Fasteners workbench fastener (typed FeaturePython)
  Placement = pos=(0,27,-52) rot=(0,0,1;0rad)
  diameter = 8
  invert = false
  matchOuter = false
  offset = 0
  thread = false
  type = 1
FEATURE [Part::Cylinder] Cylinder014005175  label="Válec169"
  Angle = 360
  AttacherType = Attacher::AttachEngine3D
  Height = 65
  Placement = pos=(-32,0,-27) rot=(0,1,0;1.5708rad)
  Radius = 1.25
FEATURE [Part::Cylinder] Cylinder014005176  label="Válec170"
  Angle = 360
  AttacherType = Attacher::AttachEngine3D
  Height = 10
  Placement = pos=(0,43,54.5) rot=(1,0,0;1.5708rad)
  Radius = 4
FEATURE [Part::Cylinder] Cylinder014005177  label="Válec171"
  Angle = 360
  AttacherType = Attacher::AttachEngine3D
  Height = 65
  Placement = pos=(-32,0,42) rot=(0,1,0;1.5708rad)
  Radius = 1.25
FEATURE [Part::Cylinder] Cylinder014005178  label="Válec172"
  Angle = 360
  AttacherType = Attacher::AttachEngine3D
  Height = 200
  Placement = pos=(0,27,-100) rot=(0,0,1;0rad)
  Radius = 3.2
FEATURE [Part::Cylinder] Cylinder014005179  label="Válec173"
  Angle = 360
  AttacherType = Attacher::AttachEngine3D
  Height = 65
  Placement = pos=(-32,0,0) rot=(0,1,0;1.5708rad)
  Radius = 1.25
FEATURE [Part::Box] Box022  label="Krychle015"
  AttacherType = Attacher::AttachEngine3D
  Height = 112
  Length = 38
  Placement = pos=(-19,32,-52) rot=(0,0,1;0rad)
  Width = 10
FEATURE [Part::Box] Box023  label="Krychle016"
  AttacherType = Attacher::AttachEngine3D
  Height = 112
  Length = 38
  Placement = pos=(-19,34,-52) rot=(0,0,1;0rad)
  Width = 6
FEATURE [Part::Cylinder] Cylinder014005180  label="Válec174"
  Angle = 360
  AttacherType = Attacher::AttachEngine3D
  Height = 10
  Placement = pos=(0,43,-47) rot=(1,0,0;1.5708rad)
  Radius = 4
FEATURE [Part::Cut] Cut061014
  Base = -> Box022
  Tool = -> Box023
FEATURE [Part::MultiFuse] Fusion103  label="Arca plate base002"
  Placement = pos=(0,-0.5,0) rot=(0,0,1;0rad)
  Shapes = -> [Extrude011,Cut061014]
FEATURE [Part::MultiFuse] Fusion104  label="Dira zavazi001"
  Shapes = -> [Cylinder014005178,Nut002,Nut003]
FEATURE [Part::MultiFuse] Fusion105  label="drzak s arca001"
  Shapes = -> [Fusion101,Fusion103,Cylinder014005176,Cylinder014005180]
FEATURE [Part::MultiFuse] Fusion106  label="diry 2,006"
  Shapes = -> [Cylinder014005179,Cylinder014005177,Cylinder014005175]
FEATURE [Part::MultiFuse] Fusion107  label="diry005"
  Shapes = -> [Fusion104,Fusion106]
FEATURE [Part::Cut] Cut061013  label="Drzak s dirama001"
  Base = -> Fusion105
  Tool = -> Fusion107
FEATURE [Part::Chamfer] Chamfer005  label="Axis2"
  Base = -> Cut061013
  Edges = 4 edges r=8: [Edge131,Edge134,Edge187,Edge191]
  Placement = pos=(0,-5,115) rot=(-1,0,0;1.5708rad)
FEATURE [Part::Box] Box024  label="Krychle017"
  AttacherType = Attacher::AttachEngine3D
  Height = 112
  Length = 38
  Placement = pos=(-19,32,-52) rot=(0,0,1;0rad)
  Width = 10
FEATURE [Part::Box] Box025  label="Krychle018"
  AttacherType = Attacher::AttachEngine3D
  Height = 112
  Length = 38
  Placement = pos=(-19,34,-52) rot=(0,0,1;0rad)
  Width = 6
FEATURE [Part::Cut] Cut061015
  Base = -> Box024
  Tool = -> Box025
FEATURE [Sketcher::SketchObject] Sketch004
  MapMode = 5
  Placement = pos=(0,0,60) rot=(0,0,1;0rad)
  sketch-geometry (6):
    g0: LineSegment StartX=-18.9734 StartY=34.0308 StartZ=0 EndX=-16.0253 EndY=36.9748 EndZ=0
    g1: LineSegment StartX=18.996 StartY=34.0308 StartZ=0 EndX=16.044 EndY=36.9748 EndZ=0
    g2: LineSegment StartX=18.996 StartY=34.0308 StartZ=0 EndX=-18.9734 EndY=34.0308 EndZ=0
    g3: LineSegment StartX=-18.9734 StartY=40.0311 StartZ=0 EndX=-16.0253 EndY=36.9748 EndZ=0
    g4: LineSegment StartX=16.044 StartY=36.9748 StartZ=0 EndX=18.9109 EndY=40.0311 EndZ=0
    g5: LineSegment StartX=-18.9734 StartY=40.0311 StartZ=0 EndX=18.9109 EndY=40.0311 EndZ=0
  constraints (7):
    c: Coincident(g2,g1)
    c: Coincident(g2,g0)
    c: Horizontal(g2)
    c: Coincident(g3,g0)
    c: Coincident(g5,g3)
    c: Coincident(g5,g4)
    c: Horizontal(g5)
FEATURE [Part::Extrusion] Extrude012
  Base = -> Sketch004
  Dir = (0,0,1)
  DirMode = 2
  FaceMakerClass = Part::FaceMakerBullseye
  LengthFwd = -112
  LengthRev = 0
  Solid = true
  Symmetric = false
FEATURE [Part::MultiFuse] Fusion108  label="Arca plate base003"
  Placement = pos=(0,-6.5,115.5) rot=(-1,0,0;1.5708rad)
  Shapes = -> [Extrude012,Cut061015]
FEATURE [Part::Box] Box026  label="Krychle019"
  AttacherType = Attacher::AttachEngine3D
  Height = 15
  Length = 50
  Placement = pos=(-25,-25,64) rot=(0,0,1;0rad)
  Width = 50
FEATURE [Part::Cut] Cut061016  label="Arca sw 1"
  Base = -> Box026
  Tool = -> Fusion108
FEATURE [Part::Box] Box027  label="Krychle020"
  AttacherType = Attacher::AttachEngine3D
  Height = 15
  Length = 2
  Placement = pos=(-15.5,-26,61) rot=(0,0,1;0rad)
  Width = 52
FEATURE [Part::Cut] Cut061017
  Base = -> Cut061016
  Tool = -> Box027
FEATURE [Sketcher::SketchObject] Sketch005
  MapMode = 45
  Placement = pos=(44.88,21.011,5.40003) rot=(0.707106,0.001666,0.707106;3.13826rad)
  sketch-geometry (7):
    g0: LineSegment StartX=5.21891 StartY=0.0364138 StartZ=0 EndX=2.62121 EndY=4.46293 EndZ=0
    g1: LineSegment StartX=2.62121 StartY=4.46293 StartZ=0 EndX=-2.51111 EndY=4.42651 EndZ=0
    g2: LineSegment StartX=-2.51111 StartY=4.42651 StartZ=0 EndX=-5.04574 EndY=-0.0364138 EndZ=0
    g3: LineSegment StartX=-5.04574 StartY=-0.0364138 StartZ=0 EndX=-2.44804 EndY=-4.46293 EndZ=0
    g4: LineSegment StartX=-2.44804 StartY=-4.46293 StartZ=0 EndX=2.68428 EndY=-4.42651 EndZ=0
    g5: LineSegment StartX=2.68428 StartY=-4.42651 StartZ=0 EndX=5.21891 EndY=0.0364138 EndZ=0
    g6: Circle [constr] CenterX=0.0865834 CenterY=0 CenterZ=0 NormalX=0 NormalY=0 NormalZ=1 AngleXU=0 Radius=5.13245
  constraints (14):
    c: Coincident(g0,g1)
    c: Coincident(g1,g2)
    c: Coincident(g2,g3)
    c: Coincident(g3,g4)
    c: Coincident(g4,g5)
    c: Coincident(g5,g0)
    c: Equal(g0, g1-g5) x5
    c: PointOnObject(g0,g6)
    c: PointOnObject(g1,g6)
    c: PointOnObject(g2,g6)
    c: PointOnObject(g3,g6)
    c: PointOnObject(g4,g6)
    c: PointOnObject(g5,g6)
    c: PointOnObject(g6,g-1)
FEATURE [Part::RegularPolygon] RegularPolygon001  label="Pravidelný n-úhelník001"
  AttacherType = Attacher::AttachEngine3D
  Circumradius = 6
  Polygon = 6
FEATURE [Part::Extrusion] Extrude013
  Base = -> Sketch005
  Dir = (1,0,0)
  DirMode = 2
  FaceMakerClass = Part::FaceMakerBullseye
  LengthFwd = 5
  LengthRev = 0
  Placement = pos=(0,0,0.25) rot=(0,0,1;0rad)
  Solid = true
  Symmetric = false
FEATURE [Part::Extrusion] Extrude014
  Base = -> RegularPolygon001
  Dir = (0,0,1)
  DirMode = 2
  FaceMakerClass = Part::FaceMakerBullseye
  LengthFwd = 8
  LengthRev = 0
  Placement = pos=(0,0,13) rot=(0,0,1;0rad)
  Solid = true
  Symmetric = false
FEATURE [Part::Feature] Screw_solid048  label="M2x4-Screw (Solid)048"
  Placement = pos=(0,0,0) rot=(0,0,1;3.14159rad)
  shape: bbox 3.6 x 3.6 x 4 mm, 12 faces (baked)
FEATURE [Part::Feature] Screw_solid049  label="M2x4-Screw (Solid)049"
  Placement = pos=(0,0,0) rot=(0,0,-1;1.0472rad)
  shape: bbox 3.6 x 3.6 x 4 mm, 12 faces (baked)
FEATURE [Part::Cylinder] Cylinder014005181  label="Válec175"
  Angle = 360
  AttacherType = Attacher::AttachEngine3D
  Height = 6
  Placement = pos=(0,0,7) rot=(0,0,1;0rad)
  Radius = 6.5
FEATURE [Part::Cylinder] Cylinder014005182  label="Válec176"
  Angle = 360
  AttacherType = Attacher::AttachEngine3D
  Height = 22
  Radius = 2.6
FEATURE [Part::MultiFuse] Fusion110
  Shapes = -> [Cylinder014005182,Extrude013]
FEATURE [Part::Cylinder] Cylinder014005183  label="Válec177"
  Angle = 360
  AttacherType = Attacher::AttachEngine3D
  Height = 7
  Radius = 2.6
FEATURE [Part::Cylinder] Cylinder014005184  label="Unasec vrch009"
  Angle = 360
  AttacherType = Attacher::AttachEngine3D
  Height = 1.5
  Placement = pos=(0,0,5.5) rot=(0,0,1;0rad)
  Radius = 15.5
FEATURE [Part::Feature] Cylinder014005185  label="Válec178"
  shape: bbox 5 x 5 x 7 mm, 3 faces (baked)
FEATURE [Part::Feature] Cylinder014005186  label="Válec179"
  Placement = pos=(0,0,0) rot=(0,0,1;2.0944rad)
  shape: bbox 5 x 5 x 7 mm, 3 faces (baked)
FEATURE [Part::Feature] Screw_solid050  label="M2x4-Screw (Solid)050"
  Placement = pos=(0,0,0) rot=(0,0,1;1.0472rad)
  shape: bbox 3.6 x 3.6 x 4 mm, 12 faces (baked)
FEATURE [Part::MultiFuse] Fusion112  label="srouby017"
  Placement = pos=(0,0,0.5) rot=(0,0,1;0rad)
  Shapes = -> [Screw_solid050,Screw_solid049,Screw_solid048]
FEATURE [Part::Cut] Cut061020  label="unasec vrch009"
  Base = -> Cylinder014005184
  Tool = -> Fusion112
FEATURE [Part::Feature] Cylinder014005187  label="Válec180"
  Placement = pos=(0,0,0) rot=(0,0,1;4.18879rad)
  shape: bbox 5 x 5 x 7 mm, 3 faces (baked)
FEATURE [Part::MultiFuse] Fusion109
  Shapes = -> [Cylinder014005187,Cylinder014005185,Cylinder014005186]
FEATURE [Part::MultiFuse] Fusion113
  Placement = pos=(0,0,1) rot=(0,0,1;0rad)
  Shapes = -> [Fusion109,Cylinder014005183]
FEATURE [Part::Cut] Cut061019  label="Unasec Vrch zaklad009"
  Base = -> Cut061020
  Tool = -> Fusion113
FEATURE [Part::MultiFuse] Fusion111
  Shapes = -> [Cut061019,Cylinder014005181,Extrude014]
FEATURE [Part::Cut] Cut061018  label="unasec top001"
  Base = -> Fusion111
  Placement = pos=(0,0,42) rot=(0,0,1;0rad)
  Tool = -> Fusion110
FEATURE [Part::Cylinder] Cylinder014005188  label="Válec181"
  Angle = 360
  AttacherType = Attacher::AttachEngine3D
  Height = 9
  Placement = pos=(0,0,55) rot=(0,0,1;0rad)
  Radius = 12.5
FEATURE [Part::Cylinder] Cylinder014005189  label="Válec182"
  Angle = 360
  AttacherType = Attacher::AttachEngine3D
  Height = 55
  Placement = pos=(0,0,35) rot=(0,0,1;0rad)
  Radius = 2.7
FEATURE [Part::Cylinder] Cylinder014005190  label="Válec183"
  Angle = 360
  AttacherType = Attacher::AttachEngine3D
  Height = 8
  Placement = pos=(0,0,66) rot=(0,0,1;0rad)
  Radius = 4.5
FEATURE [Part::MultiFuse] Fusion114
  Shapes = -> [Cylinder014005188,Cut061017]
FEATURE [Part::MultiFuse] Fusion115
  Shapes = -> [Cylinder014005189,Cut061018,Cylinder014005190]
FEATURE [Part::Cut] Cut061021
  Base = -> Fusion114
  Tool = -> Fusion115
FEATURE [Part::Cylinder] Cylinder014005191  label="Válec184"
  Angle = 360
  AttacherType = Attacher::AttachEngine3D
  Height = 60
  Placement = pos=(-30,17,69) rot=(0,1,0;1.5708rad)
  Radius = 2.1
FEATURE [Part::Cylinder] Cylinder014005192  label="Válec185"
  Angle = 360
  AttacherType = Attacher::AttachEngine3D
  Height = 60
  Placement = pos=(-30,-17,69) rot=(0,1,0;1.5708rad)
  Radius = 2.1
FEATURE [Part::FeaturePython] Nut005  label="M4-Nut"  # Fasteners workbench fastener (typed FeaturePython)
  Placement = pos=(22,17,69) rot=(0,1,0;1.5708rad)
  diameter = 6
  invert = false
  matchOuter = false
  offset = 0
  thread = false
  type = 1
FEATURE [Part::FeaturePython] Nut006  label="M4-Nut001"  # Fasteners workbench fastener (typed FeaturePython)
  Placement = pos=(22,-17,69) rot=(0,1,0;1.5708rad)
  diameter = 6
  invert = false
  matchOuter = false
  offset = 0
  thread = false
  type = 1
FEATURE [Part::MultiFuse] Fusion116
  Shapes = -> [Cylinder014005191,Cylinder014005192,Nut005,Nut006]
FEATURE [Part::Cut] Cut061022
  Base = -> Cut061021
  Tool = -> Fusion116
FEATURE [Part::Feature] Cylinder014005205  label="Válec197"
  Placement = pos=(0,0,0) rot=(0,0,1;4.18879rad)
  shape: bbox 5 x 5 x 7 mm, 3 faces (baked)
FEATURE [Part::Feature] Cut008_solid018  label="Planet019"
  Placement = pos=(0,0,0) rot=(0,0,1;2.0944rad)
  shape: bbox 12.9 x 13.1 x 5 mm, 57 faces (baked)
FEATURE [Part::Feature] Cut008_solid019  label="Planet020"
  Placement = pos=(0,0,0) rot=(0,0,1;4.18879rad)
  shape: bbox 12.9 x 13.1 x 5 mm, 57 faces (baked)
FEATURE [Part::Feature] Screw_solid054  label="M2x4-Screw (Solid)054"
  Placement = pos=(0,0,0) rot=(0,0,1;3.14159rad)
  shape: bbox 3.6 x 3.6 x 4 mm, 12 faces (baked)
FEATURE [Part::Feature] Cut007_solid007  label="Sun008"
  shape: bbox 12.9 x 13.1 x 5 mm, 57 faces (baked)
FEATURE [Part::Feature] Cut008_solid020  label="Planet021"
  shape: bbox 12.9 x 13.1 x 5 mm, 57 faces (baked)
FEATURE [Part::Feature] Cylinder014005206  label="Válec198"
  Placement = pos=(0,0,0) rot=(0,0,1;4.18879rad)
  shape: bbox 16 x 16 x 10 mm, 3 faces (baked)
FEATURE [Part::Feature] Cylinder014005207  label="Válec199"
  Placement = pos=(0,0,0) rot=(0,0,1;2.0944rad)
  shape: bbox 5 x 5 x 7 mm, 3 faces (baked)
FEATURE [Part::Feature] Cylinder014005208  label="Válec200"
  Placement = pos=(0,0,0) rot=(0,0,1;2.0944rad)
  shape: bbox 16 x 16 x 10 mm, 3 faces (baked)
FEATURE [Part::Feature] Screw_solid055  label="M2x4-Screw (Solid)055"
  Placement = pos=(0,0,0) rot=(0,0,1;1.0472rad)
  shape: bbox 3.6 x 3.6 x 4 mm, 12 faces (baked)
FEATURE [Part::Feature] Screw_solid056  label="M2x4-Screw (Solid)056"
  Placement = pos=(0,0,0) rot=(0,0,1;1.0472rad)
  shape: bbox 3.6 x 3.6 x 4 mm, 12 faces (baked)
FEATURE [Part::Feature] Cylinder014005209  label="Válec201"
  Placement = pos=(0,0,0) rot=(0,0,1;4.18879rad)
  shape: bbox 16 x 16 x 10 mm, 3 faces (baked)
FEATURE [Part::Feature] Screw_solid057  label="M2x4-Screw (Solid)057"
  Placement = pos=(0,0,0) rot=(0,0,-1;1.0472rad)
  shape: bbox 3.6 x 3.6 x 4 mm, 12 faces (baked)
FEATURE [Part::Feature] Screw_solid058  label="M2x4-Screw (Solid)058"
  Placement = pos=(0,0,0) rot=(0,0,1;3.14159rad)
  shape: bbox 3.6 x 3.6 x 4 mm, 12 faces (baked)
FEATURE [Part::MultiFuse] Fusion175  label="srouby027"
  Shapes = -> [Screw_solid056,Screw_solid057,Screw_solid058]
FEATURE [Part::Feature] Cylinder014005210  label="Válec202"
  Placement = pos=(0,0,0) rot=(0,0,1;2.0944rad)
  shape: bbox 5 x 5 x 7 mm, 3 faces (baked)
FEATURE [Part::Feature] Cut005_solid001_cs007
  Placement = pos=(0,0,-11.25) rot=(0,0,1;0rad)
  shape: bbox 41 x 41 x 3e-07 mm, 0 faces, 0 solids (baked)
FEATURE [Part::Feature] Cylinder014005211  label="Válec203"
  Placement = pos=(0,0,0) rot=(0,0,1;2.0944rad)
  shape: bbox 16 x 16 x 10 mm, 3 faces (baked)
FEATURE [Part::Feature] Screw_solid059  label="M2x4-Screw (Solid)059"
  Placement = pos=(0,0,0) rot=(0,0,-1;1.0472rad)
  shape: bbox 3.6 x 3.6 x 4 mm, 12 faces (baked)
FEATURE [Part::MultiFuse] Fusion178  label="srouby028"
  Placement = pos=(0,0,0.5) rot=(0,0,1;0rad)
  Shapes = -> [Screw_solid055,Screw_solid059,Screw_solid054]
FEATURE [Part::Cylinder] Cylinder014005212  label="Válec204"
  Angle = 360
  AttacherType = Attacher::AttachEngine3D
  Height = 10
  Placement = pos=(10.5,0,0) rot=(0,0,1;0rad)
  Radius = 8
FEATURE [Part::Cylinder] Cylinder014005213  label="Unasec vrch011"
  Angle = 360
  AttacherType = Attacher::AttachEngine3D
  Height = 1.5
  Placement = pos=(0,0,5.5) rot=(0,0,1;0rad)
  Radius = 15.5
FEATURE [Part::Cylinder] Cylinder014005214  label="unasec spodek015"
  Angle = 360
  AttacherType = Attacher::AttachEngine3D
  Height = 1.5
  Placement = pos=(0,0,-1.5) rot=(0,0,1;0rad)
  Radius = 15.5
FEATURE [Part::Cylinder] Cylinder014005215  label="unasec stred007"
  Angle = 360
  AttacherType = Attacher::AttachEngine3D
  Height = 7
  Placement = pos=(0,0,-1.5) rot=(0,0,1;0rad)
  Radius = 13.5
FEATURE [Part::MultiFuse] Fusion182
  Shapes = -> [Cylinder014005215,Cylinder014005214]
FEATURE [Part::Cylinder] Cylinder014005216  label="Válec205"
  Angle = 360
  AttacherType = Attacher::AttachEngine3D
  Height = 1.5
  Radius = 20
FEATURE [Part::Cylinder] Cylinder014005217  label="Válec206"
  Angle = 360
  AttacherType = Attacher::AttachEngine3D
  Height = 1.5
  Radius = 20
FEATURE [Part::Cylinder] Cylinder014005218  label="Válec207"
  Angle = 360
  AttacherType = Attacher::AttachEngine3D
  Height = 5.5
  Radius = 20
FEATURE [Part::Cylinder] Cylinder014005219  label="Válec208"
  Angle = 360
  AttacherType = Attacher::AttachEngine3D
  Height = 7.5
  Placement = pos=(0,0,-7) rot=(0,0,1;0rad)
  Radius = 6.5
FEATURE [Part::Cylinder] Cylinder014005220  label="Válec209"
  Angle = 360
  AttacherType = Attacher::AttachEngine3D
  Height = 1.5
  Radius = 16
FEATURE [Part::Cut] Cut061032  label="Ring014"
  Base = -> Cylinder014005216
  Placement = pos=(0,0,-1.5) rot=(0,0,1;0rad)
  Tool = -> Cylinder014005220
FEATURE [Part::Cylinder] Cylinder014005221  label="Válec210"
  Angle = 360
  AttacherType = Attacher::AttachEngine3D
  Height = 1.5
  Radius = 16
FEATURE [Part::Cylinder] Cylinder014005222  label="Válec211"
  Angle = 360
  AttacherType = Attacher::AttachEngine3D
  Height = 10
  Placement = pos=(0,0,-3) rot=(0,0,1;0rad)
  Radius = 7
FEATURE [Part::MultiFuse] Fusion181
  Shapes = -> [Cylinder014005222,Cylinder014005212,Cylinder014005209,Cylinder014005208]
FEATURE [Part::Cut] Cut061031  label="unasec spodek014"
  Base = -> Fusion182
  Tool = -> Fusion181
FEATURE [Sketcher::SketchObject] Sketch008
  MapMode = 45
  Placement = pos=(44.88,21.011,5.40003) rot=(0.707106,0.001666,0.707106;3.13826rad)
  sketch-geometry (7):
    g0: LineSegment StartX=5 StartY=0 StartZ=0 EndX=2.5 EndY=4.33013 EndZ=0
    g1: LineSegment StartX=2.5 StartY=4.33013 StartZ=0 EndX=-2.5 EndY=4.33013 EndZ=0
    g2: LineSegment StartX=-2.5 StartY=4.33013 StartZ=0 EndX=-5 EndY=0 EndZ=0
    g3: LineSegment StartX=-5 StartY=0 StartZ=0 EndX=-2.5 EndY=-4.33013 EndZ=0
    g4: LineSegment StartX=-2.5 StartY=-4.33013 StartZ=0 EndX=2.5 EndY=-4.33013 EndZ=0
    g5: LineSegment StartX=2.5 StartY=-4.33013 StartZ=0 EndX=5 EndY=0 EndZ=0
    g6: Circle [constr] CenterX=0 CenterY=0 CenterZ=0 NormalX=0 NormalY=0 NormalZ=1 AngleXU=0 Radius=5
  constraints (14):
    c: Coincident(g0,g1)
    c: Coincident(g1,g2)
    c: Coincident(g2,g3)
    c: Coincident(g3,g4)
    c: Coincident(g4,g5)
    c: Coincident(g5,g0)
    c: Equal(g0, g1-g5) x5
    c: PointOnObject(g0,g6)
    c: PointOnObject(g1,g6)
    c: PointOnObject(g2,g6)
    c: PointOnObject(g3,g6)
    c: PointOnObject(g4,g6)
    c: PointOnObject(g5,g6)
    c: PointOnObject(g6,g-1)
FEATURE [Part::Extrusion] Extrude018  label="box006"
  Base = -> Cut005_solid001_cs007
  Dir = (0,0,1)
  DirMode = 2
  FaceMakerClass = Part::FaceMakerBullseye
  LengthFwd = 19
  LengthRev = 0
  Placement = pos=(0,0,-11.5) rot=(0,0,1;0rad)
  Solid = true
  Symmetric = false
FEATURE [Part::RegularPolygon] RegularPolygon003  label="Pravidelný n-úhelník003"
  AttacherType = Attacher::AttachEngine3D
  Circumradius = 6
  Polygon = 6
FEATURE [Part::Extrusion] Extrude021
  Base = -> Sketch008
  Dir = (1,0,0)
  DirMode = 2
  FaceMakerClass = Part::FaceMakerBullseye
  LengthFwd = 5
  LengthRev = 0
  Placement = pos=(0,0,0.25) rot=(0,0,1;0rad)
  Solid = true
  Symmetric = false
FEATURE [Part::Extrusion] Extrude024
  Base = -> RegularPolygon003
  Dir = (0,0,1)
  DirMode = 2
  FaceMakerClass = Part::FaceMakerBullseye
  LengthFwd = 8
  LengthRev = 0
  Placement = pos=(0,0,13) rot=(0,0,1;0rad)
  Solid = true
  Symmetric = false
FEATURE [Part::FeaturePython] InvoluteGear014 .. InvoluteGear018  x5 (patterned run collapsed; names and placements below)
  backlash = 0
  beta = 0
  clearance = 0.25
  double_helix = false
  head = 0
  height = 5.5
  module = 1.2
  numpoints = 6
  pressure_angle = 20
  reversed_backlash = false
  shift = 0
  simple = false
  teeth = 27
  undercut = false
FEATURE [Part::Cut] Cut061036  label="Ring016"
  Base = -> Cylinder014005217
  Placement = pos=(0,0,5.5) rot=(0,0,1;0rad)
  Tool = -> Cylinder014005221
FEATURE [Part::Cut] Cut061038  label="unasec vrch011"
  Base = -> Cylinder014005213
  Tool = -> Fusion178
FEATURE [Part::Cut] Cut061039  label="ring 008"
  Base = -> Cylinder014005218
  Tool = -> InvoluteGear018
FEATURE [Part::MultiFuse] Fusion180  label="Ring zaklad Fin010"
  Shapes = -> [Cut061039,Cut061036,Cut061032]
FEATURE [Part::MultiFuse] Fusion148  label="Tělo I001"
  Shapes = -> [Extrude018,Fusion180]
FEATURE [Part::Cut] Cut061041  label="Uasec spodek007"
  Base = -> Cut061031
  Tool = -> Fusion175
FEATURE [Part::Cylinder] Cylinder014005223  label="Válec212"
  Angle = 360
  AttacherType = Attacher::AttachEngine3D
  Height = 4
  Placement = pos=(0,0,7) rot=(0,0,1;0rad)
  Radius = 6.5
FEATURE [Part::Cylinder] Cylinder014005224  label="unasec spodek018"
  Angle = 360
  AttacherType = Attacher::AttachEngine3D
  Height = 1.5
  Placement = pos=(0,0,-1.5) rot=(0,0,1;0rad)
  Radius = 15.5
FEATURE [Part::Cylinder] Cylinder014005225  label="Unasec vrch012"
  Angle = 360
  AttacherType = Attacher::AttachEngine3D
  Height = 1.5
  Placement = pos=(0,0,5.5) rot=(0,0,1;0rad)
  Radius = 15.5
FEATURE [Part::Cylinder] Cylinder014005226  label="Válec213"
  Angle = 360
  AttacherType = Attacher::AttachEngine3D
  Height = 7
  Radius = 2.6
FEATURE [Part::Cylinder] Cylinder014005227  label="Válec214"
  Angle = 360
  AttacherType = Attacher::AttachEngine3D
  Height = 7
  Placement = pos=(0,0,-7) rot=(0,0,1;0rad)
  Radius = 12
FEATURE [Part::MultiFuse] Fusion173
  Shapes = -> [Cut007_solid007,Cylinder014005219,Cylinder014005227]
FEATURE [Part::Cylinder] Cylinder014005228  label="Válec215"
  Angle = 360
  AttacherType = Attacher::AttachEngine3D
  Height = 15
  Placement = pos=(0,0,-8) rot=(0,0,1;0rad)
  Radius = 2.65
FEATURE [Part::Cylinder] Cylinder014005229  label="Válec216"
  Angle = 360
  AttacherType = Attacher::AttachEngine3D
  Height = 1.5
  Radius = 16
FEATURE [Part::Cylinder] Cylinder014005230  label="Válec217"
  Angle = 360
  AttacherType = Attacher::AttachEngine3D
  Height = 10
  Placement = pos=(0,0,-3) rot=(0,0,1;0rad)
  Radius = 7
FEATURE [Part::Cylinder] Cylinder014005231  label="Válec218"
  Angle = 360
  AttacherType = Attacher::AttachEngine3D
  Height = 1.5
  Radius = 16
FEATURE [Part::Cylinder] Cylinder014005232  label="Válec219"
  Angle = 360
  AttacherType = Attacher::AttachEngine3D
  Height = 1.5
  Radius = 20
FEATURE [Part::Cut] Cut061042  label="Ring017"
  Base = -> Cylinder014005232
  Placement = pos=(0,0,-1.5) rot=(0,0,1;0rad)
  Tool = -> Cylinder014005229
FEATURE [Part::Cylinder] Cylinder014005233  label="Válec220"
  Angle = 360
  AttacherType = Attacher::AttachEngine3D
  Height = 18
  Radius = 2.6
FEATURE [Part::Cylinder] Cylinder014005234  label="Válec221"
  Angle = 360
  AttacherType = Attacher::AttachEngine3D
  Height = 4
  Placement = pos=(0,0,7) rot=(0,0,1;0rad)
  Radius = 6.5
FEATURE [Part::Feature] Screw_solid060  label="M2x4-Screw (Solid)060"
  Placement = pos=(0,0,0) rot=(0,0,-1;1.0472rad)
  shape: bbox 3.6 x 3.6 x 4 mm, 12 faces (baked)
FEATURE [Part::Feature] Screw_solid061  label="M2x4-Screw (Solid)061"
  Placement = pos=(0,0,0) rot=(0,0,1;3.14159rad)
  shape: bbox 3.6 x 3.6 x 4 mm, 12 faces (baked)
FEATURE [Part::Feature] Cylinder014005235  label="Válec222"
  shape: bbox 5 x 5 x 7 mm, 3 faces (baked)
FEATURE [Part::Feature] Cylinder014005236  label="Válec223"
  Placement = pos=(0,0,0) rot=(0,0,1;2.0944rad)
  shape: bbox 5 x 5 x 7 mm, 3 faces (baked)
FEATURE [Part::Feature] Cylinder014005237  label="Válec224"
  shape: bbox 5 x 5 x 7 mm, 3 faces (baked)
FEATURE [Part::Feature] Screw_solid062  label="M2x4-Screw (Solid)062"
  Placement = pos=(0,0,0) rot=(0,0,1;3.14159rad)
  shape: bbox 3.6 x 3.6 x 4 mm, 12 faces (baked)
FEATURE [Part::Feature] Cut008_solid021  label="Planet022"
  shape: bbox 12.9 x 13.1 x 5 mm, 57 faces (baked)
FEATURE [Part::Feature] Cut008_solid022  label="Planet023"
  shape: bbox 12.9 x 13.1 x 5 mm, 57 faces (baked)
FEATURE [Part::Feature] Cylinder014005238  label="Válec225"
  Placement = pos=(0,0,0) rot=(0,0,1;2.0944rad)
  shape: bbox 16 x 16 x 10 mm, 3 faces (baked)
FEATURE [Part::Feature] Cylinder014005239  label="Válec226"
  Placement = pos=(0,0,0) rot=(0,0,1;2.0944rad)
  shape: bbox 5 x 5 x 7 mm, 3 faces (baked)
FEATURE [Part::Feature] Screw_solid063  label="M2x4-Screw (Solid)063"
  Placement = pos=(0,0,0) rot=(0,0,-1;1.0472rad)
  shape: bbox 3.6 x 3.6 x 4 mm, 12 faces (baked)
FEATURE [Part::Feature] Cut007_solid008  label="Sun009"
  Placement = pos=(0,0,10.5) rot=(0,0,1;0rad)
  shape: bbox 12.9 x 13.1 x 5 mm, 57 faces (baked)
FEATURE [Part::Feature] Cylinder014005240  label="Válec227"
  Placement = pos=(0,0,0) rot=(0,0,1;4.18879rad)
  shape: bbox 16 x 16 x 10 mm, 3 faces (baked)
FEATURE [Part::Feature] Cylinder014005241  label="Válec228"
  Placement = pos=(0,0,0) rot=(0,0,1;4.18879rad)
  shape: bbox 5 x 5 x 7 mm, 3 faces (baked)
FEATURE [Part::MultiFuse] Fusion176
  Shapes = -> [Cylinder014005241,Cylinder014005237,Cylinder014005236]
FEATURE [Part::MultiFuse] Fusion172
  Placement = pos=(0,0,1) rot=(0,0,1;0rad)
  Shapes = -> [Fusion176,Cylinder014005226]
FEATURE [Part::Cut] Cut061040  label="Unasec Vrch zaklad011"
  Base = -> Cut061038
  Tool = -> Fusion172
FEATURE [Part::Feature] Cut008_solid023  label="Planet024"
  Placement = pos=(0,0,0) rot=(0,0,1;4.18879rad)
  shape: bbox 12.9 x 13.1 x 5 mm, 57 faces (baked)
FEATURE [Part::Feature] Cylinder014005242  label="Válec229"
  shape: bbox 5 x 5 x 7 mm, 3 faces (baked)
FEATURE [Part::Feature] Cut008_solid024  label="Planet025"
  Placement = pos=(0,0,0) rot=(0,0,1;2.0944rad)
  shape: bbox 12.9 x 13.1 x 5 mm, 57 faces (baked)
FEATURE [Part::Feature] Cylinder014005243  label="Válec230"
  Placement = pos=(0,0,0) rot=(0,0,1;2.0944rad)
  shape: bbox 5 x 5 x 7 mm, 3 faces (baked)
FEATURE [Part::Feature] Screw_solid064  label="M2x4-Screw (Solid)064"
  Placement = pos=(0,0,0) rot=(0,0,1;1.0472rad)
  shape: bbox 3.6 x 3.6 x 4 mm, 12 faces (baked)
FEATURE [Part::MultiFuse] Fusion137  label="srouby021"
  Shapes = -> [Screw_solid064,Screw_solid060,Screw_solid061]
FEATURE [Part::Feature] Cylinder014005244  label="Válec231"
  shape: bbox 5 x 5 x 7 mm, 3 faces (baked)
FEATURE [Part::MultiFuse] Fusion174
  Shapes = -> [Cylinder014005205,Cylinder014005244,Cylinder014005207]
FEATURE [Part::MultiFuse] Fusion179  label="Unasec spdek final010"
  Shapes = -> [Cut061041,Fusion174]
FEATURE [Part::Feature] Screw_solid065  label="M2x4-Screw (Solid)065"
  Placement = pos=(0,0,0) rot=(0,0,1;3.14159rad)
  shape: bbox 3.6 x 3.6 x 4 mm, 12 faces (baked)
FEATURE [Part::Feature] Screw_solid066  label="M2x4-Screw (Solid)066"
  Placement = pos=(0,0,0) rot=(0,0,-1;1.0472rad)
  shape: bbox 3.6 x 3.6 x 4 mm, 12 faces (baked)
FEATURE [Part::Feature] Cylinder014005245  label="Válec232"
  Placement = pos=(0,0,0) rot=(0,0,1;4.18879rad)
  shape: bbox 5 x 5 x 7 mm, 3 faces (baked)
FEATURE [Part::MultiFuse] Fusion129
  Shapes = -> [Cylinder014005245,Cylinder014005242,Cylinder014005210]
FEATURE [Part::Feature] Cut007_solid009  label="Sun010"
  Placement = pos=(0,0,10.5) rot=(0,0,1;0rad)
  shape: bbox 12.9 x 13.1 x 5 mm, 57 faces (baked)
FEATURE [Part::MultiFuse] Fusion133  label="unasec vrhch 008"
  Shapes = -> [Cut061040,Cut007_solid009,Cylinder014005234]
FEATURE [Part::Cut] Cut061053  label="Unasec + Sun007"
  Base = -> Fusion133
  Tool = -> Cylinder014005233
FEATURE [Part::Cylinder] Cylinder014005246  label="Válec233"
  Angle = 360
  AttacherType = Attacher::AttachEngine3D
  Height = 7
  Radius = 2.6
FEATURE [Part::Cylinder] Cylinder014005247  label="unasec stred008"
  Angle = 360
  AttacherType = Attacher::AttachEngine3D
  Height = 7
  Placement = pos=(0,0,-1.5) rot=(0,0,1;0rad)
  Radius = 13.5
FEATURE [Part::MultiFuse] Fusion151
  Shapes = -> [Cylinder014005247,Cylinder014005224]
FEATURE [Part::Cylinder] Cylinder014005248  label="Válec234"
  Angle = 360
  AttacherType = Attacher::AttachEngine3D
  Height = 4
  Placement = pos=(0,0,7) rot=(0,0,1;0rad)
  Radius = 6.5
FEATURE [Part::Cylinder] Cylinder014005249  label="Válec235"
  Angle = 360
  AttacherType = Attacher::AttachEngine3D
  Height = 10
  Placement = pos=(10.5,0,0) rot=(0,0,1;0rad)
  Radius = 8
FEATURE [Part::MultiFuse] Fusion177
  Shapes = -> [Cylinder014005230,Cylinder014005249,Cylinder014005206,Cylinder014005211]
FEATURE [Part::Cut] Cut061035  label="unasec spodek016"
  Base = -> Fusion151
  Tool = -> Fusion177
FEATURE [Part::Cut] Cut061045  label="Uasec spodek008"
  Base = -> Cut061035
  Tool = -> Fusion137
FEATURE [Part::MultiFuse] Fusion130  label="Unasec spdek final006"
  Shapes = -> [Cut061045,Fusion129]
FEATURE [Part::Cylinder] Cylinder014005250  label="Válec236"
  Angle = 360
  AttacherType = Attacher::AttachEngine3D
  Height = 5.5
  Radius = 20
FEATURE [Part::Cut] Cut061034  label="ring 007"
  Base = -> Cylinder014005250
  Tool = -> InvoluteGear017
FEATURE [Part::Cylinder] Cylinder014005251  label="Válec237"
  Angle = 360
  AttacherType = Attacher::AttachEngine3D
  Height = 18
  Radius = 2.6
FEATURE [Part::Cylinder] Cylinder014005252  label="Válec238"
  Angle = 360
  AttacherType = Attacher::AttachEngine3D
  Height = 10
  Placement = pos=(10.5,0,0) rot=(0,0,1;0rad)
  Radius = 8
FEATURE [Part::Cylinder] Cylinder014005253  label="Válec239"
  Angle = 360
  AttacherType = Attacher::AttachEngine3D
  Height = 1.5
  Radius = 16
FEATURE [Part::Cylinder] Cylinder014005254  label="unasec stred009"
  Angle = 360
  AttacherType = Attacher::AttachEngine3D
  Height = 7
  Placement = pos=(0,0,-1.5) rot=(0,0,1;0rad)
  Radius = 13.5
FEATURE [Part::Cylinder] Cylinder014005255  label="Válec240"
  Angle = 360
  AttacherType = Attacher::AttachEngine3D
  Height = 7
  Radius = 2.6
FEATURE [Part::Cylinder] Cylinder014005256  label="Válec241"
  Angle = 360
  AttacherType = Attacher::AttachEngine3D
  Height = 1.5
  Radius = 20
FEATURE [Part::Cut] Cut061033  label="Ring015"
  Base = -> Cylinder014005256
  Placement = pos=(0,0,5.5) rot=(0,0,1;0rad)
  Tool = -> Cylinder014005231
FEATURE [Part::MultiFuse] Fusion154  label="Ring zaklad Fin007"
  Shapes = -> [Cut061034,Cut061033,Cut061042]
FEATURE [Part::Cylinder] Cylinder014005257  label="Válec242"
  Angle = 360
  AttacherType = Attacher::AttachEngine3D
  Height = 10
  Placement = pos=(0,0,-3) rot=(0,0,1;0rad)
  Radius = 7
FEATURE [Part::MultiFuse] Fusion152
  Shapes = -> [Cylinder014005257,Cylinder014005252,Cylinder014005240,Cylinder014005238]
FEATURE [Part::Cylinder] Cylinder014005258  label="unasec spodek019"
  Angle = 360
  AttacherType = Attacher::AttachEngine3D
  Height = 1.5
  Placement = pos=(0,0,-1.5) rot=(0,0,1;0rad)
  Radius = 15.5
FEATURE [Part::MultiFuse] Fusion134
  Shapes = -> [Cylinder014005254,Cylinder014005258]
FEATURE [Part::Cut] Cut061047  label="unasec spodek017"
  Base = -> Fusion134
  Tool = -> Fusion152
FEATURE [Part::Cylinder] Cylinder014005259  label="Válec243"
  Angle = 360
  AttacherType = Attacher::AttachEngine3D
  Height = 1.5
  Radius = 20
FEATURE [Part::Cylinder] Cylinder014005260  label="Válec244"
  Angle = 360
  AttacherType = Attacher::AttachEngine3D
  Height = 1.5
  Radius = 20
FEATURE [Part::Cylinder] Cylinder014005261  label="Válec245"
  Angle = 360
  AttacherType = Attacher::AttachEngine3D
  Height = 10
  Placement = pos=(10.5,0,0) rot=(0,0,1;0rad)
  Radius = 8
FEATURE [Part::Cylinder] Cylinder014005262  label="Válec246"
  Angle = 360
  AttacherType = Attacher::AttachEngine3D
  Height = 1.5
  Radius = 16
FEATURE [Part::Cylinder] Cylinder014005263  label="Válec247"
  Angle = 360
  AttacherType = Attacher::AttachEngine3D
  Height = 18
  Radius = 2.6
FEATURE [Part::Cylinder] Cylinder014005264  label="Unasec vrch013"
  Angle = 360
  AttacherType = Attacher::AttachEngine3D
  Height = 1.5
  Placement = pos=(0,0,5.5) rot=(0,0,1;0rad)
  Radius = 15.5
FEATURE [Part::Cylinder] Cylinder014005265  label="Válec248"
  Angle = 360
  AttacherType = Attacher::AttachEngine3D
  Height = 1.5
  Radius = 20
FEATURE [Part::Cut] Cut061055  label="Ring019"
  Base = -> Cylinder014005265
  Placement = pos=(0,0,5.5) rot=(0,0,1;0rad)
  Tool = -> Cylinder014005253
FEATURE [Part::Cylinder] Cylinder014005266  label="Válec249"
  Angle = 360
  AttacherType = Attacher::AttachEngine3D
  Height = 1.5
  Radius = 20
FEATURE [Part::Cylinder] Cylinder014005267  label="Válec250"
  Angle = 360
  AttacherType = Attacher::AttachEngine3D
  Height = 1.5
  Radius = 16
FEATURE [Part::Cut] Cut061046  label="Ring018"
  Base = -> Cylinder014005260
  Placement = pos=(0,0,-1.5) rot=(0,0,1;0rad)
  Tool = -> Cylinder014005267
FEATURE [Part::Cylinder] Cylinder014005268  label="Válec251"
  Angle = 360
  AttacherType = Attacher::AttachEngine3D
  Height = 18
  Radius = 2.6
FEATURE [Part::Cylinder] Cylinder014005269  label="Válec252"
  Angle = 360
  AttacherType = Attacher::AttachEngine3D
  Height = 5.5
  Radius = 20
FEATURE [Part::Cut] Cut061054  label="ring 009"
  Base = -> Cylinder014005269
  Tool = -> InvoluteGear014
FEATURE [Part::MultiFuse] Fusion153  label="Ring zaklad Fin006"
  Shapes = -> [Cut061054,Cut061055,Cut061046]
FEATURE [Part::Cylinder] Cylinder014005270  label="Válec253"
  Angle = 360
  AttacherType = Attacher::AttachEngine3D
  Height = 10
  Placement = pos=(0,0,-3) rot=(0,0,1;0rad)
  Radius = 7
FEATURE [Part::Cut] Cut061073  label="Ring023"
  Base = -> Cylinder014005266
  Placement = pos=(0,0,-1.5) rot=(0,0,1;0rad)
  Tool = -> Cylinder014005262
FEATURE [Part::Feature] Cut008_solid025  label="Planet026"
  Placement = pos=(0,0,0) rot=(0,0,1;2.0944rad)
  shape: bbox 12.9 x 13.1 x 5 mm, 57 faces (baked)
FEATURE [Part::Feature] Cut008_solid026  label="Planet027"
  Placement = pos=(0,0,0) rot=(0,0,1;4.18879rad)
  shape: bbox 12.9 x 13.1 x 5 mm, 57 faces (baked)
FEATURE [Part::Feature] Cut008_solid027  label="Planet028"
  shape: bbox 12.9 x 13.1 x 5 mm, 57 faces (baked)
FEATURE [Part::Feature] Screw_solid067  label="M2x4-Screw (Solid)067"
  Placement = pos=(0,0,0) rot=(0,0,1;1.0472rad)
  shape: bbox 3.6 x 3.6 x 4 mm, 12 faces (baked)
FEATURE [Part::Feature] Cylinder014005271  label="Válec254"
  shape: bbox 5 x 5 x 7 mm, 3 faces (baked)
FEATURE [Part::Feature] Cylinder014005272  label="Válec255"
  Placement = pos=(0,0,0) rot=(0,0,1;4.18879rad)
  shape: bbox 5 x 5 x 7 mm, 3 faces (baked)
FEATURE [Part::MultiFuse] Fusion141
  Shapes = -> [Cylinder014005272,Cylinder014005235,Cylinder014005239]
FEATURE [Part::MultiFuse] Fusion144
  Placement = pos=(0,0,1) rot=(0,0,1;0rad)
  Shapes = -> [Fusion141,Cylinder014005246]
FEATURE [Part::Feature] Cut005_solid001_cs008
  Placement = pos=(0,0,-11.25) rot=(0,0,1;0rad)
  shape: bbox 41 x 41 x 3e-07 mm, 0 faces, 0 solids (baked)
FEATURE [Part::Extrusion] Extrude020  label="box008"
  Base = -> Cut005_solid001_cs008
  Dir = (0,0,1)
  DirMode = 2
  FaceMakerClass = Part::FaceMakerBullseye
  LengthFwd = 10.5
  LengthRev = 0
  Placement = pos=(0,0,-3) rot=(0,0,1;0rad)
  Solid = true
  Symmetric = false
FEATURE [Part::Feature] Cut008_solid028  label="Planet029"
  Placement = pos=(0,0,0) rot=(0,0,1;4.18879rad)
  shape: bbox 12.9 x 13.1 x 5 mm, 57 faces (baked)
FEATURE [Part::Feature] Cylinder014005273  label="Válec256"
  Placement = pos=(0,0,0) rot=(0,0,1;4.18879rad)
  shape: bbox 5 x 5 x 7 mm, 3 faces (baked)
FEATURE [Part::Feature] Screw_solid068  label="M2x4-Screw (Solid)068"
  Placement = pos=(0,0,0) rot=(0,0,1;1.0472rad)
  shape: bbox 3.6 x 3.6 x 4 mm, 12 faces (baked)
FEATURE [Part::Feature] Cylinder014005274  label="Válec257"
  Placement = pos=(0,0,0) rot=(0,0,1;4.18879rad)
  shape: bbox 5 x 5 x 7 mm, 3 faces (baked)
FEATURE [Part::Feature] Screw_solid069  label="M2x4-Screw (Solid)069"
  Placement = pos=(0,0,0) rot=(0,0,-1;1.0472rad)
  shape: bbox 3.6 x 3.6 x 4 mm, 12 faces (baked)
FEATURE [Part::MultiFuse] Fusion142  label="srouby022"
  Shapes = -> [Screw_solid068,Screw_solid069,Screw_solid065]
FEATURE [Part::Cut] Cut061051  label="Uasec spodek009"
  Base = -> Cut061047
  Tool = -> Fusion142
FEATURE [Part::Feature] Screw_solid070  label="M2x4-Screw (Solid)070"
  Placement = pos=(0,0,0) rot=(0,0,1;1.0472rad)
  shape: bbox 3.6 x 3.6 x 4 mm, 12 faces (baked)
FEATURE [Part::Feature] Screw_solid071  label="M2x4-Screw (Solid)071"
  Placement = pos=(0,0,0) rot=(0,0,1;1.0472rad)
  shape: bbox 3.6 x 3.6 x 4 mm, 12 faces (baked)
FEATURE [Part::MultiFuse] Fusion145  label="srouby023"
  Placement = pos=(0,0,0.5) rot=(0,0,1;0rad)
  Shapes = -> [Screw_solid071,Screw_solid066,Screw_solid062]
FEATURE [Part::Cut] Cut061050  label="unasec vrch013"
  Base = -> Cylinder014005225
  Tool = -> Fusion145
FEATURE [Part::Cut] Cut061049  label="Unasec Vrch zaklad013"
  Base = -> Cut061050
  Tool = -> Fusion144
FEATURE [Part::MultiFuse] Fusion147  label="unasec vrhch 010"
  Shapes = -> [Cut061049,Cut007_solid008,Cylinder014005223]
FEATURE [Part::Cut] Cut061043  label="Unasec + Sun005"
  Base = -> Fusion147
  Tool = -> Cylinder014005251
FEATURE [Part::Feature] Cylinder014005275  label="Válec258"
  Placement = pos=(0,0,0) rot=(0,0,1;2.0944rad)
  shape: bbox 5 x 5 x 7 mm, 3 faces (baked)
FEATURE [Part::Feature] Cylinder014005276  label="Válec259"
  shape: bbox 5 x 5 x 7 mm, 3 faces (baked)
FEATURE [Part::MultiFuse] Fusion132
  Shapes = -> [Cylinder014005273,Cylinder014005276,Cylinder014005275]
FEATURE [Part::MultiFuse] Fusion138
  Placement = pos=(0,0,1) rot=(0,0,1;0rad)
  Shapes = -> [Fusion132,Cylinder014005255]
FEATURE [Part::Feature] Cut005_solid001_cs009
  Placement = pos=(0,0,-11.25) rot=(0,0,1;0rad)
  shape: bbox 41 x 41 x 3e-07 mm, 0 faces, 0 solids (baked)
FEATURE [Part::Extrusion] Extrude022  label="box009"
  Base = -> Cut005_solid001_cs009
  Dir = (0,0,1)
  DirMode = 2
  FaceMakerClass = Part::FaceMakerBullseye
  LengthFwd = 10.5
  LengthRev = 0
  Placement = pos=(0,0,-3) rot=(0,0,1;0rad)
  Solid = true
  Symmetric = false
FEATURE [Part::MultiFuse] Fusion150  label="teloII007"
  Shapes = -> [Fusion154,Extrude022]
FEATURE [App::Part] Part014  label="Part022"
  Group = -> [Cut061035,Cut061045,Cylinder014005230,Cylinder014005224,Cylinder014005247,Cylinder014005249,Cylinder014005206,Cylinder014005210,Cylinder014005211,Screw_solid061,Cylinder014005242,Screw_solid064,Cylinder014005245,Screw_solid060,Fusion177,Fusion151,Fusion137,Fusion129,Fusion130,Cut008_solid021,Cut008_solid024,Cut008_solid023,Screw_solid071,Cylinder014005235,Cylinder014005239,Screw_solid066,+27 more]
  License = CC BY 3.0
  LicenseURL = http://creativecommons.org/licenses/by/3.0/
  Origin = -> Origin011
  Placement = pos=(0,0,10.5) rot=(0,0,1;0rad)
FEATURE [Part::Feature] Cylinder014005277  label="Válec260"
  Placement = pos=(0,0,0) rot=(0,0,1;2.0944rad)
  shape: bbox 16 x 16 x 10 mm, 3 faces (baked)
FEATURE [Part::Feature] Cut005_solid001_cs010
  Placement = pos=(0,0,-11.25) rot=(0,0,1;0rad)
  shape: bbox 41 x 41 x 3e-07 mm, 0 faces, 0 solids (baked)
FEATURE [Part::Extrusion] Extrude019  label="box007"
  Base = -> Cut005_solid001_cs010
  Dir = (0,0,1)
  DirMode = 2
  FaceMakerClass = Part::FaceMakerBullseye
  LengthFwd = 10.5
  LengthRev = 0
  Placement = pos=(0,0,-3) rot=(0,0,1;0rad)
  Solid = true
  Symmetric = false
FEATURE [Part::MultiFuse] Fusion139  label="teloII005"
  Shapes = -> [Fusion153,Extrude019]
FEATURE [Part::Feature] Screw_solid072  label="M2x4-Screw (Solid)072"
  Placement = pos=(0,0,0) rot=(0,0,1;3.14159rad)
  shape: bbox 3.6 x 3.6 x 4 mm, 12 faces (baked)
FEATURE [Part::MultiFuse] Fusion131  label="srouby019"
  Placement = pos=(0,0,0.5) rot=(0,0,1;0rad)
  Shapes = -> [Screw_solid070,Screw_solid063,Screw_solid072]
FEATURE [Part::Cut] Cut061048  label="unasec vrch012"
  Base = -> Cylinder014005264
  Tool = -> Fusion131
FEATURE [Part::Cut] Cut061044  label="Unasec Vrch zaklad012"
  Base = -> Cut061048
  Tool = -> Fusion138
FEATURE [Part::Feature] Cut007_solid010  label="Sun011"
  Placement = pos=(0,0,10.5) rot=(0,0,1;0rad)
  shape: bbox 12.9 x 13.1 x 5 mm, 57 faces (baked)
FEATURE [Part::Feature] Cylinder014005278  label="Válec261"
  shape: bbox 5 x 5 x 7 mm, 3 faces (baked)
FEATURE [Part::MultiFuse] Fusion128
  Shapes = -> [Cylinder014005274,Cylinder014005278,Cylinder014005243]
FEATURE [Part::MultiFuse] Fusion143  label="Unasec spdek final008"
  Shapes = -> [Cut061051,Fusion128]
FEATURE [Part::Feature] Cut007_solid011  label="Sun012"
  Placement = pos=(0,0,10.5) rot=(0,0,1;0rad)
  shape: bbox 12.9 x 13.1 x 5 mm, 57 faces (baked)
FEATURE [Part::MultiFuse] Fusion155  label="unasec vrhch 011"
  Shapes = -> [Cut061044,Cut007_solid011,Cylinder014005248]
FEATURE [Part::Cut] Cut061052  label="Unasec + Sun006"
  Base = -> Fusion155
  Tool = -> Cylinder014005268
FEATURE [App::Part] Part013  label="Part021"
  Group = -> [Cut061047,Cut061051,Cylinder014005257,Cylinder014005258,Cylinder014005254,Cylinder014005252,Cylinder014005240,Cylinder014005243,Cylinder014005238,Screw_solid065,Cylinder014005278,Screw_solid068,Cylinder014005274,Screw_solid069,Fusion152,Fusion134,Fusion142,Fusion128,Fusion143,Cut008_solid022,Cut008_solid025,Cut008_solid028,Screw_solid070,Cylinder014005276,Cylinder014005275,Screw_solid063,+27 more]
  License = CC BY 3.0
  LicenseURL = http://creativecommons.org/licenses/by/3.0/
  Origin = -> Origin013
  Placement = pos=(0,0,21) rot=(0,0,1;0rad)
FEATURE [Part::Feature] Cylinder014005279  label="Válec262"
  Placement = pos=(0,0,0) rot=(0,0,1;2.0944rad)
  shape: bbox 5 x 5 x 7 mm, 3 faces (baked)
FEATURE [Part::Feature] Screw_solid073  label="M2x4-Screw (Solid)073"
  Placement = pos=(0,0,0) rot=(0,0,1;3.14159rad)
  shape: bbox 3.6 x 3.6 x 4 mm, 12 faces (baked)
FEATURE [Part::Feature] Cylinder014005280  label="Válec263"
  Placement = pos=(0,0,0) rot=(0,0,1;2.0944rad)
  shape: bbox 5 x 5 x 7 mm, 3 faces (baked)
FEATURE [Part::Feature] Screw_solid074  label="M2x4-Screw (Solid)074"
  Placement = pos=(0,0,0) rot=(0,0,-1;1.0472rad)
  shape: bbox 3.6 x 3.6 x 4 mm, 12 faces (baked)
FEATURE [Part::Feature] Cylinder014005281  label="Válec264"
  shape: bbox 5 x 5 x 7 mm, 3 faces (baked)
FEATURE [Part::Feature] Cylinder014005282  label="Válec265"
  shape: bbox 5 x 5 x 7 mm, 3 faces (baked)
FEATURE [Part::Feature] Cut008_solid029  label="Planet030"
  shape: bbox 12.9 x 13.1 x 5 mm, 57 faces (baked)
FEATURE [Part::Feature] Screw_solid075  label="M2x4-Screw (Solid)075"
  Placement = pos=(0,0,0) rot=(0,0,-1;1.0472rad)
  shape: bbox 3.6 x 3.6 x 4 mm, 12 faces (baked)
FEATURE [Part::Feature] Screw_solid076  label="M2x4-Screw (Solid)076"
  Placement = pos=(0,0,0) rot=(0,0,1;1.0472rad)
  shape: bbox 3.6 x 3.6 x 4 mm, 12 faces (baked)
FEATURE [Part::Feature] Cut061074  label="SUN I Final001"
  shape: bbox 24 x 24 x 12.25 mm, 99 faces (baked)
FEATURE [App::Part] Part015  label="Part023"
  Group = -> [Cut008_solid020,Cut008_solid018,Cut008_solid019,Cylinder014005214,Cylinder014005222,Cylinder014005212,Fusion181,Fusion182,Cylinder014005205,Cylinder014005207,Cylinder014005209,Cylinder014005208,Cylinder014005244,Cylinder014005215,Cut061031,Cut061041,Screw_solid058,Screw_solid056,Screw_solid057,Fusion174,Fusion175,Fusion179,Cylinder014005234,Cylinder014005233,Cut007_solid009,Cut061038,Cut061040,+32 more]
  License = CC BY 3.0
  LicenseURL = http://creativecommons.org/licenses/by/3.0/
  Origin = -> Origin012
FEATURE [Part::Feature] Screw_solid077  label="M2x4-Screw (Solid)077"
  Placement = pos=(0,0,0) rot=(0,0,-1;1.0472rad)
  shape: bbox 3.6 x 3.6 x 4 mm, 12 faces (baked)
FEATURE [Part::Feature] Cylinder014005283  label="Válec266"
  Placement = pos=(0,0,0) rot=(0,0,1;2.0944rad)
  shape: bbox 16 x 16 x 10 mm, 3 faces (baked)
FEATURE [Part::Feature] Screw_solid078  label="M2x4-Screw (Solid)078"
  Placement = pos=(0,0,0) rot=(0,0,1;3.14159rad)
  shape: bbox 3.6 x 3.6 x 4 mm, 12 faces (baked)
FEATURE [Part::Feature] Cut007_solid012  label="Sun013"
  Placement = pos=(0,0,10.5) rot=(0,0,1;0rad)
  shape: bbox 12.9 x 13.1 x 5 mm, 57 faces (baked)
FEATURE [Part::Feature] Cylinder014005284  label="Válec267"
  Placement = pos=(0,0,0) rot=(0,0,1;4.18879rad)
  shape: bbox 5 x 5 x 7 mm, 3 faces (baked)
FEATURE [Part::MultiFuse] Fusion159
  Shapes = -> [Cylinder014005284,Cylinder014005281,Cylinder014005279]
FEATURE [Part::Feature] Screw_solid079  label="M2x4-Screw (Solid)079"
  Placement = pos=(0,0,0) rot=(0,0,1;3.14159rad)
  shape: bbox 3.6 x 3.6 x 4 mm, 12 faces (baked)
FEATURE [Part::Feature] Cut008_solid030  label="Planet031"
  Placement = pos=(0,0,0) rot=(0,0,1;2.0944rad)
  shape: bbox 12.9 x 13.1 x 5 mm, 57 faces (baked)
FEATURE [Part::Feature] Cylinder014005285  label="Válec268"
  Placement = pos=(0,0,0) rot=(0,0,1;4.18879rad)
  shape: bbox 5 x 5 x 7 mm, 3 faces (baked)
FEATURE [Part::Feature] Cylinder014005286  label="Válec269"
  Placement = pos=(0,0,0) rot=(0,0,1;2.0944rad)
  shape: bbox 5 x 5 x 7 mm, 3 faces (baked)
FEATURE [Part::Feature] Screw_solid080  label="M2x4-Screw (Solid)080"
  Placement = pos=(0,0,0) rot=(0,0,1;1.0472rad)
  shape: bbox 3.6 x 3.6 x 4 mm, 12 faces (baked)
FEATURE [Part::MultiFuse] Fusion160  label="srouby024"
  Placement = pos=(0,0,0.5) rot=(0,0,1;0rad)
  Shapes = -> [Screw_solid080,Screw_solid074,Screw_solid079]
FEATURE [Part::Feature] Cylinder014005287  label="Válec270"
  shape: bbox 5 x 5 x 7 mm, 3 faces (baked)
FEATURE [Part::MultiFuse] Fusion146
  Shapes = -> [Cylinder014005285,Cylinder014005287,Cylinder014005286]
FEATURE [Part::Feature] Screw_solid081  label="M2x4-Screw (Solid)081"
  Placement = pos=(0,0,0) rot=(0,0,1;3.14159rad)
  shape: bbox 3.6 x 3.6 x 4 mm, 12 faces (baked)
FEATURE [Part::MultiFuse] Fusion136  label="srouby020"
  Shapes = -> [Screw_solid067,Screw_solid077,Screw_solid081]
FEATURE [Part::Feature] Cylinder014005288  label="Válec271"
  Placement = pos=(0,0,0) rot=(0,0,1;4.18879rad)
  shape: bbox 16 x 16 x 10 mm, 3 faces (baked)
FEATURE [Part::Feature] Screw_solid082  label="M2x4-Screw (Solid)082"
  Placement = pos=(0,0,0) rot=(0,0,-1;1.0472rad)
  shape: bbox 3.6 x 3.6 x 4 mm, 12 faces (baked)
FEATURE [Part::Feature] Cylinder014005289  label="Válec272"
  Placement = pos=(0,0,0) rot=(0,0,1;4.18879rad)
  shape: bbox 16 x 16 x 10 mm, 3 faces (baked)
FEATURE [Part::MultiFuse] Fusion127
  Shapes = -> [Cylinder014005270,Cylinder014005261,Cylinder014005289,Cylinder014005277]
FEATURE [Part::Cylinder] Cylinder014005290  label="unasec spodek022"
  Angle = 360
  AttacherType = Attacher::AttachEngine3D
  Height = 1.5
  Placement = pos=(0,0,-1.5) rot=(0,0,1;0rad)
  Radius = 15.5
FEATURE [Part::Cylinder] Cylinder014005291  label="Válec273"
  Angle = 360
  AttacherType = Attacher::AttachEngine3D
  Height = 1.5
  Radius = 16
FEATURE [Part::Cylinder] Cylinder014005292  label="Válec274"
  Angle = 360
  AttacherType = Attacher::AttachEngine3D
  Height = 1.5
  Radius = 16
FEATURE [Part::Cylinder] Cylinder014005293  label="Válec275"
  Angle = 360
  AttacherType = Attacher::AttachEngine3D
  Height = 18
  Radius = 2.6
FEATURE [Part::Cylinder] Cylinder014005294  label="Unasec vrch014"
  Angle = 360
  AttacherType = Attacher::AttachEngine3D
  Height = 1.5
  Placement = pos=(0,0,5.5) rot=(0,0,1;0rad)
  Radius = 15.5
FEATURE [Part::Cut] Cut061067  label="unasec vrch016"
  Base = -> Cylinder014005294
  Tool = -> Fusion160
FEATURE [Part::Cylinder] Cylinder014005295  label="unasec stred010"
  Angle = 360
  AttacherType = Attacher::AttachEngine3D
  Height = 7
  Placement = pos=(0,0,-1.5) rot=(0,0,1;0rad)
  Radius = 13.5
FEATURE [Part::MultiFuse] Fusion165
  Shapes = -> [Cylinder014005295,Cylinder014005290]
FEATURE [Part::Cut] Cut061071  label="unasec spodek021"
  Base = -> Fusion165
  Tool = -> Fusion127
FEATURE [Part::Cut] Cut061058  label="Uasec spodek010"
  Base = -> Cut061071
  Tool = -> Fusion136
FEATURE [Part::MultiFuse] Fusion158  label="Unasec spdek final009"
  Shapes = -> [Cut061058,Fusion159]
FEATURE [Part::Cylinder] Cylinder014005296  label="Válec276"
  Angle = 360
  AttacherType = Attacher::AttachEngine3D
  Height = 5.5
  Radius = 20
FEATURE [Part::Cut] Cut061064  label="ring 010"
  Base = -> Cylinder014005296
  Tool = -> InvoluteGear015
FEATURE [Part::Cylinder] Cylinder014005297  label="Válec277"
  Angle = 360
  AttacherType = Attacher::AttachEngine3D
  Height = 1.5
  Radius = 16
FEATURE [Part::Cut] Cut061061  label="Ring020"
  Base = -> Cylinder014005259
  Placement = pos=(0,0,5.5) rot=(0,0,1;0rad)
  Tool = -> Cylinder014005297
FEATURE [Part::MultiFuse] Fusion157  label="Ring zaklad Fin008"
  Shapes = -> [Cut061064,Cut061061,Cut061073]
FEATURE [Part::MultiFuse] Fusion156  label="teloII008"
  Shapes = -> [Fusion157,Extrude020]
FEATURE [Part::Cylinder] Cylinder014005298  label="Válec278"
  Angle = 360
  AttacherType = Attacher::AttachEngine3D
  Height = 1.5
  Radius = 20
FEATURE [Part::Cut] Cut061063  label="Ring021"
  Base = -> Cylinder014005298
  Placement = pos=(0,0,5.5) rot=(0,0,1;0rad)
  Tool = -> Cylinder014005292
FEATURE [Part::Cylinder] Cylinder014005299  label="Válec279"
  Angle = 360
  AttacherType = Attacher::AttachEngine3D
  Height = 4
  Placement = pos=(0,0,7) rot=(0,0,1;0rad)
  Radius = 6.5
FEATURE [Part::Cylinder] Cylinder014005300  label="Válec280"
  Angle = 360
  AttacherType = Attacher::AttachEngine3D
  Height = 7
  Radius = 2.6
FEATURE [Part::MultiFuse] Fusion161
  Placement = pos=(0,0,1) rot=(0,0,1;0rad)
  Shapes = -> [Fusion146,Cylinder014005300]
FEATURE [Part::Cut] Cut061062  label="Unasec Vrch zaklad015"
  Base = -> Cut061067
  Tool = -> Fusion161
FEATURE [Part::MultiFuse] Fusion135  label="unasec vrhch 009"
  Shapes = -> [Cut061062,Cut007_solid010,Cylinder014005299]
FEATURE [Part::Cut] Cut061066  label="Unasec + Sun008"
  Base = -> Fusion135
  Tool = -> Cylinder014005263
FEATURE [App::Part] Part016
  Group = -> [Cut061071,Cut061058,Cylinder014005270,Cylinder014005290,Cylinder014005295,Cylinder014005261,Cylinder014005289,Cylinder014005279,Cylinder014005277,Screw_solid081,Cylinder014005281,Screw_solid067,Cylinder014005284,Screw_solid077,Fusion127,Fusion165,Fusion136,Fusion159,Fusion158,Cut008_solid027,Cut008_solid030,Cut008_solid026,Screw_solid080,Cylinder014005287,Cylinder014005286,Screw_solid074,+27 more]
  License = CC BY 3.0
  LicenseURL = http://creativecommons.org/licenses/by/3.0/
  Origin = -> Origin015
  Placement = pos=(0,0,31.5) rot=(0,0,1;0rad)
FEATURE [Part::Cylinder] Cylinder014005301  label="Válec281"
  Angle = 360
  AttacherType = Attacher::AttachEngine3D
  Height = 5.5
  Radius = 20
FEATURE [Part::Cut] Cut061068  label="ring 011"
  Base = -> Cylinder014005301
  Tool = -> InvoluteGear016
FEATURE [Part::Cylinder] Cylinder014005302  label="Válec282"
  Angle = 360
  AttacherType = Attacher::AttachEngine3D
  Height = 6
  Placement = pos=(0,0,7) rot=(0,0,1;0rad)
  Radius = 6.5
FEATURE [Part::Cylinder] Cylinder014005303  label="Válec283"
  Angle = 360
  AttacherType = Attacher::AttachEngine3D
  Height = 1.5
  Radius = 20
FEATURE [Part::Cut] Cut061065  label="Ring022"
  Base = -> Cylinder014005303
  Placement = pos=(0,0,-1.5) rot=(0,0,1;0rad)
  Tool = -> Cylinder014005291
FEATURE [Part::MultiFuse] Fusion169  label="Ring zaklad Fin009"
  Shapes = -> [Cut061068,Cut061063,Cut061065]
FEATURE [Part::Cylinder] Cylinder014005304  label="Válec284"
  Angle = 360
  AttacherType = Attacher::AttachEngine3D
  Height = 4
  Placement = pos=(0,0,7) rot=(0,0,1;0rad)
  Radius = 6.5
FEATURE [Part::Cylinder] Cylinder014005305  label="Unasec vrch015"
  Angle = 360
  AttacherType = Attacher::AttachEngine3D
  Height = 1.5
  Placement = pos=(0,0,5.5) rot=(0,0,1;0rad)
  Radius = 15.5
FEATURE [Part::Cylinder] Cylinder014005306  label="Válec285"
  Angle = 360
  AttacherType = Attacher::AttachEngine3D
  Height = 10
  Placement = pos=(10.5,0,0) rot=(0,0,1;0rad)
  Radius = 8
FEATURE [Part::Cylinder] Cylinder014005307  label="Válec286"
  Angle = 360
  AttacherType = Attacher::AttachEngine3D
  Height = 7
  Radius = 2.6
FEATURE [Part::Cylinder] Cylinder014005308  label="unasec stred011"
  Angle = 360
  AttacherType = Attacher::AttachEngine3D
  Height = 7
  Placement = pos=(0,0,-1.5) rot=(0,0,1;0rad)
  Radius = 13.5
FEATURE [Part::Cylinder] Cylinder014005309  label="Válec287"
  Angle = 360
  AttacherType = Attacher::AttachEngine3D
  Height = 10
  Placement = pos=(0,0,-3) rot=(0,0,1;0rad)
  Radius = 7
FEATURE [Part::MultiFuse] Fusion162
  Shapes = -> [Cylinder014005309,Cylinder014005306,Cylinder014005288,Cylinder014005283]
FEATURE [Part::Cylinder] Cylinder014005310  label="Válec288"
  Angle = 360
  AttacherType = Attacher::AttachEngine3D
  Height = 22
  Radius = 2.6
FEATURE [Part::MultiFuse] Fusion183
  Shapes = -> [Cylinder014005310,Extrude021]
FEATURE [Part::Cylinder] Cylinder014005311  label="Válec289"
  Angle = 360
  AttacherType = Attacher::AttachEngine3D
  Height = 7
  Radius = 2.6
FEATURE [Part::Cylinder] Cylinder014005312  label="unasec spodek023"
  Angle = 360
  AttacherType = Attacher::AttachEngine3D
  Height = 1.5
  Placement = pos=(0,0,-1.5) rot=(0,0,1;0rad)
  Radius = 15.5
FEATURE [Part::MultiFuse] Fusion170
  Shapes = -> [Cylinder014005308,Cylinder014005312]
FEATURE [Part::Cut] Cut061060  label="unasec spodek020"
  Base = -> Fusion170
  Tool = -> Fusion162
FEATURE [Part::Cylinder] Cylinder014005313  label="Unasec vrch016"
  Angle = 360
  AttacherType = Attacher::AttachEngine3D
  Height = 1.5
  Placement = pos=(0,0,5.5) rot=(0,0,1;0rad)
  Radius = 15.5
FEATURE [Part::Feature] Screw_solid083  label="M2x4-Screw (Solid)083"
  Placement = pos=(0,0,0) rot=(0,0,-1;1.0472rad)
  shape: bbox 3.6 x 3.6 x 4 mm, 12 faces (baked)
FEATURE [Part::MultiFuse] Fusion166  label="srouby026"
  Shapes = -> [Screw_solid076,Screw_solid083,Screw_solid073]
FEATURE [Part::Cut] Cut061069  label="Uasec spodek011"
  Base = -> Cut061060
  Tool = -> Fusion166
FEATURE [Part::Feature] Cylinder014005314  label="Válec290"
  shape: bbox 5 x 5 x 7 mm, 3 faces (baked)
FEATURE [Part::Feature] Cylinder014005315  label="Válec291"
  Placement = pos=(0,0,0) rot=(0,0,1;2.0944rad)
  shape: bbox 5 x 5 x 7 mm, 3 faces (baked)
FEATURE [Part::Feature] Screw_solid084  label="M2x4-Screw (Solid)084"
  Placement = pos=(0,0,0) rot=(0,0,1;3.14159rad)
  shape: bbox 3.6 x 3.6 x 4 mm, 12 faces (baked)
FEATURE [Part::Feature] Cylinder014005316  label="Válec292"
  Placement = pos=(0,0,0) rot=(0,0,1;4.18879rad)
  shape: bbox 5 x 5 x 7 mm, 3 faces (baked)
FEATURE [Part::MultiFuse] Fusion168
  Shapes = -> [Cylinder014005316,Cylinder014005271,Cylinder014005280]
FEATURE [Part::MultiFuse] Fusion171
  Placement = pos=(0,0,1) rot=(0,0,1;0rad)
  Shapes = -> [Fusion168,Cylinder014005307]
FEATURE [Part::Feature] Cylinder014005317  label="Válec293"
  Placement = pos=(0,0,0) rot=(0,0,1;4.18879rad)
  shape: bbox 5 x 5 x 7 mm, 3 faces (baked)
FEATURE [Part::Feature] Screw_solid085  label="M2x4-Screw (Solid)085"
  Placement = pos=(0,0,0) rot=(0,0,1;1.0472rad)
  shape: bbox 3.6 x 3.6 x 4 mm, 12 faces (baked)
FEATURE [Part::MultiFuse] Fusion185  label="srouby029"
  Placement = pos=(0,0,0.5) rot=(0,0,1;0rad)
  Shapes = -> [Screw_solid085,Screw_solid082,Screw_solid078]
FEATURE [Part::Cut] Cut061059  label="unasec vrch015"
  Base = -> Cylinder014005313
  Tool = -> Fusion185
FEATURE [Part::Feature] Screw_solid086  label="M2x4-Screw (Solid)086"
  Placement = pos=(0,0,0) rot=(0,0,1;1.0472rad)
  shape: bbox 3.6 x 3.6 x 4 mm, 12 faces (baked)
FEATURE [Part::MultiFuse] Fusion164  label="srouby025"
  Placement = pos=(0,0,0.5) rot=(0,0,1;0rad)
  Shapes = -> [Screw_solid086,Screw_solid075,Screw_solid084]
FEATURE [Part::Cut] Cut061057  label="unasec vrch014"
  Base = -> Cylinder014005305
  Tool = -> Fusion164
FEATURE [Part::Cut] Cut061072  label="Unasec Vrch zaklad016"
  Base = -> Cut061057
  Tool = -> Fusion171
FEATURE [Part::MultiFuse] Fusion163  label="unasec vrhch 012"
  Shapes = -> [Cut061072,Cut007_solid012,Cylinder014005304]
FEATURE [Part::Cut] Cut061070  label="Unasec + Sun005 old001"
  Base = -> Fusion163
  Tool = -> Cylinder014005293
FEATURE [Part::Feature] Cut005_solid001_cs011
  Placement = pos=(0,0,-11.25) rot=(0,0,1;0rad)
  shape: bbox 41 x 41 x 3e-07 mm, 0 faces, 0 solids (baked)
FEATURE [Part::Extrusion] Extrude023  label="box010"
  Base = -> Cut005_solid001_cs011
  Dir = (0,0,1)
  DirMode = 2
  FaceMakerClass = Part::FaceMakerBullseye
  LengthFwd = 10.5
  LengthRev = 0
  Placement = pos=(0,0,-3) rot=(0,0,1;0rad)
  Solid = true
  Symmetric = false
FEATURE [Part::MultiFuse] Fusion149  label="teloII006"
  Shapes = -> [Fusion169,Extrude023]
FEATURE [Part::Feature] Cut008_solid031  label="Planet032"
  Placement = pos=(0,0,0) rot=(0,0,1;2.0944rad)
  shape: bbox 12.9 x 13.1 x 5 mm, 57 faces (baked)
FEATURE [Part::Feature] Cylinder014005318  label="Válec294"
  Placement = pos=(0,0,0) rot=(0,0,1;2.0944rad)
  shape: bbox 5 x 5 x 7 mm, 3 faces (baked)
FEATURE [Part::MultiFuse] Fusion167
  Shapes = -> [Cylinder014005317,Cylinder014005282,Cylinder014005318]
FEATURE [Part::MultiFuse] Fusion140  label="Unasec spdek final007"
  Shapes = -> [Cut061069,Fusion167]
FEATURE [Part::Feature] Cylinder014005319  label="Válec295"
  Placement = pos=(0,0,0) rot=(0,0,1;4.18879rad)
  shape: bbox 5 x 5 x 7 mm, 3 faces (baked)
FEATURE [Part::MultiFuse] Fusion126
  Shapes = -> [Cylinder014005319,Cylinder014005314,Cylinder014005315]
FEATURE [Part::MultiFuse] Fusion186
  Placement = pos=(0,0,1) rot=(0,0,1;0rad)
  Shapes = -> [Fusion126,Cylinder014005311]
FEATURE [Part::Cut] Cut061056  label="Unasec Vrch zaklad014"
  Base = -> Cut061059
  Tool = -> Fusion186
FEATURE [Part::MultiFuse] Fusion184
  Shapes = -> [Cut061056,Cylinder014005302,Extrude024]
FEATURE [Part::Cut] Cut061037  label="unasec top003"
  Base = -> Fusion184
  Tool = -> Fusion183
FEATURE [Part::Feature] Cut008_solid032  label="Planet033"
  Placement = pos=(0,0,0) rot=(0,0,1;4.18879rad)
  shape: bbox 12.9 x 13.1 x 5 mm, 57 faces (baked)
FEATURE [App::Part] Part012
  Group = -> [Cut061060,Cut061069,Cylinder014005309,Cylinder014005312,Cylinder014005308,Cylinder014005306,Cylinder014005288,Cylinder014005318,Cylinder014005283,Screw_solid073,Cylinder014005282,Screw_solid076,Cylinder014005317,Screw_solid083,Fusion162,Fusion170,Fusion166,Fusion167,Fusion140,Cut008_solid029,Cut008_solid031,Cut008_solid032,Screw_solid086,Cylinder014005271,Cylinder014005280,Screw_solid075,+49 more]
  License = CC BY 3.0
  LicenseURL = http://creativecommons.org/licenses/by/3.0/
  Origin = -> Origin014
  Placement = pos=(0,0,42) rot=(0,0,1;0rad)
FEATURE [App::Part] Part011  label="GearBOX 1024:1b"
  Group = -> [Part015,Part014,Part013,Part016,Part012]
  License = CC BY 3.0
  LicenseURL = http://creativecommons.org/licenses/by/3.0/
  Origin = -> Origin016
  Placement = pos=(0,-5,115) rot=(-1,0,0;1.5708rad)
FEATURE [Part::Box] Box032  label="Krychle025"
  AttacherType = Attacher::AttachEngine3D
  Height = 40
  Length = 41
  Placement = pos=(-20.5,-20.5,0) rot=(0,0,1;0rad)
  Width = 41
FEATURE [Part::Chamfer] Chamfer006
  Base = -> Box032
  Edges = 4 edges r=5: [Edge1,Edge3,Edge5,Edge7]
FEATURE [Part::Cylinder] Cylinder014005320  label="Válec296"
  Angle = 360
  AttacherType = Attacher::AttachEngine3D
  Height = 50
  Placement = pos=(-15.5,-15.5,0) rot=(0,0,1;0rad)
  Radius = 1.6
FEATURE [Part::Cylinder] Cylinder014005321  label="Válec297"
  Angle = 360
  AttacherType = Attacher::AttachEngine3D
  Height = 50
  Placement = pos=(15.5,15.5,0) rot=(0,0,1;0rad)
  Radius = 1.6
FEATURE [Part::Cylinder] Cylinder014005322  label="Válec298"
  Angle = 360
  AttacherType = Attacher::AttachEngine3D
  Height = 50
  Placement = pos=(-15.5,15.5,0) rot=(0,0,1;0rad)
  Radius = 1.6
FEATURE [Part::Cylinder] Cylinder014005323  label="Válec299"
  Angle = 360
  AttacherType = Attacher::AttachEngine3D
  Height = 50
  Placement = pos=(15.5,-15.5,0) rot=(0,0,1;0rad)
  Radius = 1.6
FEATURE [Part::MultiFuse] Fusion187  label="diry006"
  Shapes = -> [Cylinder014005322,Cylinder014005321,Cylinder014005320,Cylinder014005323]
FEATURE [Part::Cut] Cut061075
  Base = -> Chamfer006
  Tool = -> Fusion187
FEATURE [App::Part] Part017  label="NEAM17  motor- 40mm001"
  Group = -> [Chamfer006,Fusion187,Box032,Cylinder014005322,Cylinder014005321,Cylinder014005320,Cylinder014005323,Cut061075]
  License = CC BY 3.0
  LicenseURL = http://creativecommons.org/licenses/by/3.0/
  Origin = -> Origin017
  Placement = pos=(0,-56.5,115) rot=(-1,0,0;1.5708rad)
FEATURE [Part::Cylinder] Cylinder014005324  label="Válec300"
  Angle = 360
  AttacherType = Attacher::AttachEngine3D
  Height = 2.5
  Placement = pos=(0,-12,71) rot=(0,0,1;0rad)
  Radius = 6
FEATURE [Part::Box] Box033  label="Krychle026"
  AttacherType = Attacher::AttachEngine3D
  Height = 2.5
  Length = 12
  Placement = pos=(-6,-25,71) rot=(0,0,1;0rad)
  Width = 13
FEATURE [Part::MultiFuse] Fusion188
  Placement = pos=(0,0,1) rot=(0,0,1;0rad)
  Shapes = -> [Box033,Cylinder014005324]
FEATURE [Part::Cylinder] Cylinder014005325  label="Válec301"
  Angle = 360
  AttacherType = Attacher::AttachEngine3D
  Height = 2.5
  Placement = pos=(0,-12,71) rot=(0,0,1;0rad)
  Radius = 6
FEATURE [Part::Box] Box034  label="Krychle027"
  AttacherType = Attacher::AttachEngine3D
  Height = 2.5
  Length = 12
  Placement = pos=(-6,-25,71) rot=(0,0,1;0rad)
  Width = 13
FEATURE [Part::MultiFuse] Fusion189
  Placement = pos=(0,0,1) rot=(0,0,1;3.14159rad)
  Shapes = -> [Box034,Cylinder014005325]
FEATURE [Part::MultiFuse] Fusion190
  Shapes = -> [Fusion188,Fusion189]
FEATURE [Part::Cut] Cut061076  label="Swis Arca1"
  Base = -> Cut061022
  Tool = -> Fusion190
FEATURE [Part::RegularPolygon] RegularPolygon004  label="Pravidelný n-úhelník004"
  AttacherType = Attacher::AttachEngine3D
  Circumradius = 6
  Polygon = 6
FEATURE [Part::Extrusion] Extrude027
  Base = -> RegularPolygon004
  Dir = (0,0,1)
  DirMode = 2
  FaceMakerClass = Part::FaceMakerBullseye
  LengthFwd = 8
  LengthRev = 0
  Placement = pos=(0,0,13) rot=(0,0,1;0rad)
  Solid = true
  Symmetric = false
FEATURE [Part::FeaturePython] Nut007  label="M4-Nut002"  # Fasteners workbench fastener (typed FeaturePython)
  Placement = pos=(22,17,69) rot=(0,1,0;1.5708rad)
  diameter = 6
  invert = false
  matchOuter = false
  offset = 0
  thread = false
  type = 1
FEATURE [Part::FeaturePython] Nut008  label="M4-Nut003"  # Fasteners workbench fastener (typed FeaturePython)
  Placement = pos=(22,-17,69) rot=(0,1,0;1.5708rad)
  diameter = 6
  invert = false
  matchOuter = false
  offset = 0
  thread = false
  type = 1
FEATURE [Sketcher::SketchObject] Sketch009
  MapMode = 5
  Placement = pos=(0,0,60) rot=(0,0,1;0rad)
  sketch-geometry (6):
    g0: LineSegment StartX=-18.9734 StartY=34.0308 StartZ=0 EndX=-16.0253 EndY=36.9748 EndZ=0
    g1: LineSegment StartX=18.996 StartY=34.0308 StartZ=0 EndX=16.044 EndY=36.9748 EndZ=0
    g2: LineSegment StartX=18.996 StartY=34.0308 StartZ=0 EndX=-18.9734 EndY=34.0308 EndZ=0
    g3: LineSegment StartX=-18.9734 StartY=40.0311 StartZ=0 EndX=-16.0253 EndY=36.9748 EndZ=0
    g4: LineSegment StartX=16.044 StartY=36.9748 StartZ=0 EndX=18.9109 EndY=40.0311 EndZ=0
    g5: LineSegment StartX=-18.9734 StartY=40.0311 StartZ=0 EndX=18.9109 EndY=40.0311 EndZ=0
  constraints (7):
    c: Coincident(g2,g1)
    c: Coincident(g2,g0)
    c: Horizontal(g2)
    c: Coincident(g3,g0)
    c: Coincident(g5,g3)
    c: Coincident(g5,g4)
    c: Horizontal(g5)
FEATURE [Part::Extrusion] Extrude025
  Base = -> Sketch009
  Dir = (0,0,1)
  DirMode = 2
  FaceMakerClass = Part::FaceMakerBullseye
  LengthFwd = -112
  LengthRev = 0
  Solid = true
  Symmetric = false
FEATURE [Sketcher::SketchObject] Sketch010
  MapMode = 45
  Placement = pos=(44.88,21.011,5.40003) rot=(0.707106,0.001666,0.707106;3.13826rad)
  sketch-geometry (7):
    g0: LineSegment StartX=5.21891 StartY=0.0364138 StartZ=0 EndX=2.62121 EndY=4.46293 EndZ=0
    g1: LineSegment StartX=2.62121 StartY=4.46293 StartZ=0 EndX=-2.51111 EndY=4.42651 EndZ=0
    g2: LineSegment StartX=-2.51111 StartY=4.42651 StartZ=0 EndX=-5.04574 EndY=-0.0364138 EndZ=0
    g3: LineSegment StartX=-5.04574 StartY=-0.0364138 StartZ=0 EndX=-2.44804 EndY=-4.46293 EndZ=0
    g4: LineSegment StartX=-2.44804 StartY=-4.46293 StartZ=0 EndX=2.68428 EndY=-4.42651 EndZ=0
    g5: LineSegment StartX=2.68428 StartY=-4.42651 StartZ=0 EndX=5.21891 EndY=0.0364138 EndZ=0
    g6: Circle [constr] CenterX=0.0865834 CenterY=0 CenterZ=0 NormalX=0 NormalY=0 NormalZ=1 AngleXU=0 Radius=5.13245
  constraints (14):
    c: Coincident(g0,g1)
    c: Coincident(g1,g2)
    c: Coincident(g2,g3)
    c: Coincident(g3,g4)
    c: Coincident(g4,g5)
    c: Coincident(g5,g0)
    c: Equal(g0, g1-g5) x5
    c: PointOnObject(g0,g6)
    c: PointOnObject(g1,g6)
    c: PointOnObject(g2,g6)
    c: PointOnObject(g3,g6)
    c: PointOnObject(g4,g6)
    c: PointOnObject(g5,g6)
    c: PointOnObject(g6,g-1)
FEATURE [Part::Extrusion] Extrude026
  Base = -> Sketch010
  Dir = (1,0,0)
  DirMode = 2
  FaceMakerClass = Part::FaceMakerBullseye
  LengthFwd = 5
  LengthRev = 0
  Placement = pos=(0,0,0.25) rot=(0,0,1;0rad)
  Solid = true
  Symmetric = false
FEATURE [Part::Feature] Screw_solid087  label="M2x4-Screw (Solid)087"
  Placement = pos=(0,0,0) rot=(0,0,1;3.14159rad)
  shape: bbox 3.6 x 3.6 x 4 mm, 12 faces (baked)
FEATURE [Part::Feature] Cylinder014005326  label="Válec302"
  Placement = pos=(0,0,0) rot=(0,0,1;2.0944rad)
  shape: bbox 5 x 5 x 7 mm, 3 faces (baked)
FEATURE [Part::Feature] Cylinder014005327  label="Válec303"
  Placement = pos=(0,0,0) rot=(0,0,1;4.18879rad)
  shape: bbox 5 x 5 x 7 mm, 3 faces (baked)
FEATURE [Part::Feature] Screw_solid088  label="M2x4-Screw (Solid)088"
  Placement = pos=(0,0,0) rot=(0,0,1;1.0472rad)
  shape: bbox 3.6 x 3.6 x 4 mm, 12 faces (baked)
FEATURE [Part::Feature] Cylinder014005328  label="Válec304"
  shape: bbox 5 x 5 x 7 mm, 3 faces (baked)
FEATURE [Part::MultiFuse] Fusion196
  Shapes = -> [Cylinder014005327,Cylinder014005328,Cylinder014005326]
FEATURE [Part::Feature] Screw_solid089  label="M2x4-Screw (Solid)089"
  Placement = pos=(0,0,0) rot=(0,0,-1;1.0472rad)
  shape: bbox 3.6 x 3.6 x 4 mm, 12 faces (baked)
FEATURE [Part::MultiFuse] Fusion199  label="srouby030"
  Placement = pos=(0,0,0.5) rot=(0,0,1;0rad)
  Shapes = -> [Screw_solid088,Screw_solid089,Screw_solid087]
FEATURE [Part::Box] Box035  label="Krychle028"
  AttacherType = Attacher::AttachEngine3D
  Height = 112
  Length = 38
  Placement = pos=(-19,32,-52) rot=(0,0,1;0rad)
  Width = 10
FEATURE [Part::Box] Box036  label="Krychle029"
  AttacherType = Attacher::AttachEngine3D
  Height = 112
  Length = 38
  Placement = pos=(-19,34,-52) rot=(0,0,1;0rad)
  Width = 6
FEATURE [Part::Cylinder] Cylinder014005329  label="Válec305"
  Angle = 360
  AttacherType = Attacher::AttachEngine3D
  Height = 22
  Radius = 2.6
FEATURE [Part::MultiFuse] Fusion195
  Shapes = -> [Cylinder014005329,Extrude026]
FEATURE [Part::Cylinder] Cylinder014005330  label="Válec306"
  Angle = 360
  AttacherType = Attacher::AttachEngine3D
  Height = 7
  Radius = 2.6
FEATURE [Part::MultiFuse] Fusion198
  Placement = pos=(0,0,1) rot=(0,0,1;0rad)
  Shapes = -> [Fusion196,Cylinder014005330]
FEATURE [Part::Cylinder] Cylinder014005331  label="Válec307"
  Angle = 360
  AttacherType = Attacher::AttachEngine3D
  Height = 8
  Placement = pos=(0,0,66) rot=(0,0,1;0rad)
  Radius = 4.5
FEATURE [Part::Box] Box037  label="Krychle030"
  AttacherType = Attacher::AttachEngine3D
  Height = 15
  Length = 50
  Placement = pos=(-25,-25,64) rot=(0,0,1;0rad)
  Width = 50
FEATURE [Part::Cylinder] Cylinder014005332  label="Válec308"
  Angle = 360
  AttacherType = Attacher::AttachEngine3D
  Height = 6
  Placement = pos=(0,0,7) rot=(0,0,1;0rad)
  Radius = 6.5
FEATURE [Part::Box] Box038  label="Krychle031"
  AttacherType = Attacher::AttachEngine3D
  Height = 15
  Length = 2
  Placement = pos=(-15.5,-26,61) rot=(0,0,1;0rad)
  Width = 52
FEATURE [Part::Cylinder] Cylinder014005333  label="Unasec vrch017"
  Angle = 360
  AttacherType = Attacher::AttachEngine3D
  Height = 1.5
  Placement = pos=(0,0,5.5) rot=(0,0,1;0rad)
  Radius = 15.5
FEATURE [Part::Cylinder] Cylinder014005334  label="Válec309"
  Angle = 360
  AttacherType = Attacher::AttachEngine3D
  Height = 55
  Placement = pos=(0,0,35) rot=(0,0,1;0rad)
  Radius = 2.7
FEATURE [Part::Cylinder] Cylinder014005335  label="Válec310"
  Angle = 360
  AttacherType = Attacher::AttachEngine3D
  Height = 9
  Placement = pos=(0,0,55) rot=(0,0,1;0rad)
  Radius = 12.5
FEATURE [Part::Cut] Cut061079  label="unasec vrch017"
  Base = -> Cylinder014005333
  Tool = -> Fusion199
FEATURE [Part::Cut] Cut061080
  Base = -> Box035
  Tool = -> Box036
FEATURE [Part::MultiFuse] Fusion194  label="Arca plate base004"
  Placement = pos=(0,-6.5,115.5) rot=(-1,0,0;1.5708rad)
  Shapes = -> [Extrude025,Cut061080]
FEATURE [Part::Cut] Cut061077  label="Arca sw 002"
  Base = -> Box037
  Tool = -> Fusion194
FEATURE [Part::Cut] Cut061083
  Base = -> Cut061077
  Tool = -> Box038
FEATURE [Part::MultiFuse] Fusion192
  Shapes = -> [Cylinder014005335,Cut061083]
FEATURE [Part::Cut] Cut061084  label="Unasec Vrch zaklad017"
  Base = -> Cut061079
  Tool = -> Fusion198
FEATURE [Part::MultiFuse] Fusion197
  Shapes = -> [Cut061084,Cylinder014005332,Extrude027]
FEATURE [Part::Cut] Cut061081  label="unasec top004"
  Base = -> Fusion197
  Placement = pos=(0,0,42) rot=(0,0,1;0rad)
  Tool = -> Fusion195
FEATURE [Part::MultiFuse] Fusion191
  Shapes = -> [Cylinder014005334,Cut061081,Cylinder014005331]
FEATURE [Part::Cut] Cut061082
  Base = -> Fusion192
  Tool = -> Fusion191
FEATURE [Part::Cylinder] Cylinder014005336  label="Válec311"
  Angle = 360
  AttacherType = Attacher::AttachEngine3D
  Height = 60
  Placement = pos=(-30,17,69) rot=(0,1,0;1.5708rad)
  Radius = 2.1
FEATURE [Part::Cylinder] Cylinder014005337  label="Válec312"
  Angle = 360
  AttacherType = Attacher::AttachEngine3D
  Height = 60
  Placement = pos=(-30,-17,69) rot=(0,1,0;1.5708rad)
  Radius = 2.1
FEATURE [Part::MultiFuse] Fusion193
  Shapes = -> [Cylinder014005336,Cylinder014005337,Nut007,Nut008]
FEATURE [Part::Cut] Cut061078
  Base = -> Cut061082
  Tool = -> Fusion193
FEATURE [Part::Cylinder] Cylinder014005338  label="Válec313"
  Angle = 360
  AttacherType = Attacher::AttachEngine3D
  Height = 2.5
  Placement = pos=(0,-12,71) rot=(0,0,1;0rad)
  Radius = 6
FEATURE [Part::Box] Box039  label="Krychle032"
  AttacherType = Attacher::AttachEngine3D
  Height = 2.5
  Length = 12
  Placement = pos=(-6,-25,71) rot=(0,0,1;0rad)
  Width = 13
FEATURE [Part::MultiFuse] Fusion201
  Placement = pos=(0,0,1) rot=(0,0,1;3.14159rad)
  Shapes = -> [Box039,Cylinder014005338]
FEATURE [Part::Cylinder] Cylinder014005339  label="Válec314"
  Angle = 360
  AttacherType = Attacher::AttachEngine3D
  Height = 2.5
  Placement = pos=(0,-12,71) rot=(0,0,1;0rad)
  Radius = 6
FEATURE [Part::Box] Box040  label="Krychle033"
  AttacherType = Attacher::AttachEngine3D
  Height = 2.5
  Length = 12
  Placement = pos=(-6,-25,71) rot=(0,0,1;0rad)
  Width = 13
FEATURE [Part::MultiFuse] Fusion200
  Placement = pos=(0,0,1) rot=(0,0,1;0rad)
  Shapes = -> [Box040,Cylinder014005339]
FEATURE [Part::MultiFuse] Fusion202
  Shapes = -> [Fusion200,Fusion201]
FEATURE [Part::Cut] Cut061085  label="Swis Arca002"
  Base = -> Cut061078
  Placement = pos=(0,-5,115) rot=(-1,0,0;1.5708rad)
  Tool = -> Fusion202
FEATURE [Part::Box] Box041  label="Krychle034"
  AttacherType = Attacher::AttachEngine3D
  Height = 2
  Length = 80
  Placement = pos=(-40,-50,59) rot=(0,0,1;0rad)
  Width = 80
FEATURE [Part::Box] Box042  label="Krychle035"
  AttacherType = Attacher::AttachEngine3D
  Height = 2
  Length = 80
  Placement = pos=(-40,-50,-53) rot=(0,0,1;0rad)
  Width = 80
FEATURE [Part::MultiFuse] Fusion203
  Shapes = -> [Box041,Box042]
FEATURE [Part::Cut] Cut061086  label="Axix1 fin"
  Base = -> Chamfer003
  Tool = -> Fusion203
FEATURE [Part::Box] Box043  label="Krychle036"
  AttacherType = Attacher::AttachEngine3D
  Height = 2
  Length = 80
  Placement = pos=(-40,-50,-53) rot=(0,0,1;0rad)
  Width = 80
FEATURE [Part::Box] Box044  label="Krychle037"
  AttacherType = Attacher::AttachEngine3D
  Height = 2
  Length = 80
  Placement = pos=(-40,-50,59) rot=(0,0,1;0rad)
  Width = 80
FEATURE [Part::MultiFuse] Fusion204
  Placement = pos=(0,-5,98) rot=(-1,0,0;1.5708rad)
  Shapes = -> [Box044,Box043]
FEATURE [Part::Cut] Cut061087  label="Axis2 fin"
  Base = -> Chamfer005
  Tool = -> Fusion204
FEATURE [Part::Box] Box002  label="Krychle002"
  AttacherType = Attacher::AttachEngine3D
  Height = 3
  Length = 13
  Placement = pos=(-6.5,0,-3) rot=(0,0,1;0rad)
  Width = 4
FEATURE [Sketcher::SketchObject] Sketch011
  MapMode = 5
  Placement = pos=(0,40,0) rot=(0,0.707107,0.707107;3.14159rad)
  sketch-geometry (6):
    g0: LineSegment StartX=0 StartY=0 StartZ=0 EndX=0 EndY=3 EndZ=0
    g1: LineSegment StartX=0 StartY=3 StartZ=0 EndX=-4 EndY=10 EndZ=0
    g2: LineSegment StartX=-4 StartY=10 StartZ=0 EndX=-26 EndY=10 EndZ=0
    g3: LineSegment StartX=-26 StartY=10 StartZ=0 EndX=-30 EndY=3 EndZ=0
    g4: LineSegment StartX=-30 StartY=3 StartZ=0 EndX=-30 EndY=0 EndZ=0
    g5: LineSegment StartX=-30 StartY=0 StartZ=0 EndX=0 EndY=0 EndZ=0
  constraints (11):
    c: Coincident(g-1,g0)
    c: PointOnObject(g0,g-2)
    c: Coincident(g0,g1)
    c: Coincident(g1,g2)
    c: Horizontal(g2)
    c: Coincident(g2,g3)
    c: Coincident(g3,g4)
    c: PointOnObject(g4,g-1)
    c: Vertical(g4)
    c: Coincident(g4,g5)
    c: Coincident(g5,g0)
FEATURE [Part::Extrusion] Extrude028
  Base = -> Sketch011
  Dir = (0,1,0)
  DirMode = 2
  FaceMakerClass = Part::FaceMakerBullseye
  LengthFwd = -40
  LengthRev = 0
  Placement = pos=(-15,0,0) rot=(0,0,1;0rad)
  Solid = true
  Symmetric = false
FEATURE [Part::MultiFuse] Fusion206  label="Dovetal profile001"
  Shapes = -> [Extrude028,Box002]
FEATURE [Part::Cylinder] Cylinder014005340  label="Válec315"
  Angle = 360
  AttacherType = Attacher::AttachEngine3D
  Height = 10
  Placement = pos=(12,20,4) rot=(0,1,0;0.785398rad)
  Radius = 1.4
FEATURE [Part::Cylinder] Cylinder001  label="Válec001"
  Angle = 360
  AttacherType = Attacher::AttachEngine3D
  Height = 10
  Placement = pos=(-12,20,4) rot=(0,-1,0;0.785398rad)
  Radius = 1.4
FEATURE [Part::MultiFuse] Fusion205
  Shapes = -> [Cylinder014005340,Cylinder001]
FEATURE [Part::Box] Box001  label="Krychle001"
  AttacherType = Attacher::AttachEngine3D
  Height = 15
  Length = 36
  Placement = pos=(-18,0,-5) rot=(0,0,1;0rad)
  Width = 40
FEATURE [Part::Cut] Cut061088
  Base = -> Box001
  Tool = -> Fusion206
FEATURE [Part::Chamfer] Chamfer007
  Base = -> Cut061088
  Edges = 2 edges r=5: [Edge2,Edge29]
FEATURE [Part::Cut] Cut001  label="Dov holder"
  Base = -> Chamfer007
  Placement = pos=(-35,-26,-12) rot=(1,0,0;1.5708rad)
  Tool = -> Fusion205
FEATURE [Part::Feature] Cut001001  label="Dov holder001"
  Placement = pos=(-4.5,-43,-39) rot=(0,0,-1;1.5708rad)
  shape: bbox 15 x 36 x 40 mm, 20 faces (baked)
FEATURE [Part::Box] Box045  label="Krychle038"
  AttacherType = Attacher::AttachEngine3D
  Height = 4
  Length = 3
  Placement = pos=(-30.5,-14.5,-51) rot=(0,0,1;0rad)
  Width = 13
FEATURE [Part::Cylinder] Cylinder014005341  label="Válec316"
  Angle = 360
  AttacherType = Attacher::AttachEngine3D
  Height = 65
  Placement = pos=(-32,0,-27) rot=(0,1,0;1.5708rad)
  Radius = 1.25
FEATURE [Part::MultiFuse] Fusion207
  Shapes = -> [Cut061086,Cut001001]
FEATURE [Part::MultiFuse] Fusion208
  Shapes = -> [Box045,Cylinder014005341]
FEATURE [Part::Cut] Cut061089  label="Axix1 final"
  Base = -> Fusion207
  Tool = -> Fusion208
FEATURE [Part::FeaturePython] Nut009  label="M4-Nut004"  # Fasteners workbench fastener (typed FeaturePython)
  Placement = pos=(-40.2,7,53) rot=(1,0,0;1.5708rad)
  diameter = 6
  invert = false
  matchOuter = false
  offset = 0
  thread = false
  type = 1
FEATURE [Part::FeaturePython] Screw002  label="M4x20-Screw002"  # Fasteners workbench fastener (typed FeaturePython)
  Placement = pos=(-40.5,-9,53) rot=(1,0,0;1.5708rad)
  diameter = 4
  invert = false
  length = 5
  matchOuter = false
  offset = 0
  thread = false
  type = 5
FEATURE [Part::FeaturePython] Nut010  label="M4-Nut005"  # Fasteners workbench fastener (typed FeaturePython)
  Placement = pos=(-40.2,7,53) rot=(1,0,0;1.5708rad)
  diameter = 6
  invert = false
  matchOuter = false
  offset = 0
  thread = false
  type = 1
FEATURE [Part::FeaturePython] Screw001  label="M4x20-Screw001"  # Fasteners workbench fastener (typed FeaturePython)
  Placement = pos=(-40.5,-9,53) rot=(1,0,0;1.5708rad)
  diameter = 4
  invert = false
  length = 5
  matchOuter = false
  offset = 0
  thread = false
  type = 5
FEATURE [Part::FeaturePython] Screw003  label="M4x20-Screw003"  # Fasteners workbench fastener (typed FeaturePython)
  Placement = pos=(-40.5,-9,53) rot=(1,0,0;1.5708rad)
  diameter = 4
  invert = false
  length = 5
  matchOuter = false
  offset = 0
  thread = false
  type = 5
FEATURE [Part::Cylinder] Cylinder014005342  label="tubus001"
  Angle = 360
  AttacherType = Attacher::AttachEngine3D
  Height = 15
  Placement = pos=(0,-1,-52) rot=(0,0,1;0rad)
  Radius = 37
FEATURE [Part::FeaturePython] Nut011  label="M4-Nut006"  # Fasteners workbench fastener (typed FeaturePython)
  Placement = pos=(-40.2,7,53) rot=(1,0,0;1.5708rad)
  diameter = 6
  invert = false
  matchOuter = false
  offset = 0
  thread = false
  type = 1
FEATURE [Part::FeaturePython] Nut012  label="M4-Nut007"  # Fasteners workbench fastener (typed FeaturePython)
  Placement = pos=(-40.2,7,53) rot=(1,0,0;1.5708rad)
  diameter = 6
  invert = false
  matchOuter = false
  offset = 0
  thread = false
  type = 1
FEATURE [Part::FeaturePython] Screw  label="M4x20-Screw"  # Fasteners workbench fastener (typed FeaturePython)
  Placement = pos=(-40.5,-9,53) rot=(1,0,0;1.5708rad)
  diameter = 4
  invert = false
  length = 5
  matchOuter = false
  offset = 0
  thread = false
  type = 5
FEATURE [Part::Box] Box046  label="Krychle039"
  AttacherType = Attacher::AttachEngine3D
  Height = 15
  Length = 90
  Placement = pos=(-45,-10,-52) rot=(0,0,1;0rad)
  Width = 17
FEATURE [Part::Box] Box047  label="mezara001"
  AttacherType = Attacher::AttachEngine3D
  Height = 15
  Length = 90
  Placement = pos=(-45,-3,-52) rot=(0,0,1;0rad)
  Width = 3
FEATURE [Part::Box] Box048  label="Krychle040"
  AttacherType = Attacher::AttachEngine3D
  Height = 15
  Length = 90
  Placement = pos=(-45,-10,45) rot=(0,0,1;0rad)
  Width = 17
FEATURE [Part::Box] Box049  label="Krychle041"
  AttacherType = Attacher::AttachEngine3D
  Height = 112
  Length = 38
  Placement = pos=(-19,34,-52) rot=(0,0,1;0rad)
  Width = 6
FEATURE [Part::Box] Box050  label="mezara"
  AttacherType = Attacher::AttachEngine3D
  Height = 15
  Length = 90
  Placement = pos=(-45,-3,45) rot=(0,0,1;0rad)
  Width = 3
FEATURE [Part::Box] Box051  label="Krychle042"
  AttacherType = Attacher::AttachEngine3D
  Height = 112
  Length = 38
  Placement = pos=(-19,32,-52) rot=(0,0,1;0rad)
  Width = 10
FEATURE [Part::Cylinder] Cylinder014005343  label="tubus"
  Angle = 360
  AttacherType = Attacher::AttachEngine3D
  Height = 112
  Placement = pos=(0,-1,-52) rot=(0,0,1;0rad)
  Radius = 32
FEATURE [Part::Cylinder] Cylinder014005344  label="tubus002"
  Angle = 360
  AttacherType = Attacher::AttachEngine3D
  Height = 15
  Placement = pos=(0,-1,45) rot=(0,0,1;0rad)
  Radius = 37
FEATURE [Sketcher::SketchObject] Sketch012
  MapMode = 5
  Placement = pos=(0,0,60) rot=(0,0,1;0rad)
  sketch-geometry (6):
    g0: LineSegment StartX=-18.9734 StartY=34.0308 StartZ=0 EndX=-16.0253 EndY=36.9748 EndZ=0
    g1: LineSegment StartX=18.996 StartY=34.0308 StartZ=0 EndX=16.044 EndY=36.9748 EndZ=0
    g2: LineSegment StartX=18.996 StartY=34.0308 StartZ=0 EndX=-18.9734 EndY=34.0308 EndZ=0
    g3: LineSegment StartX=-18.9734 StartY=40.0311 StartZ=0 EndX=-16.0253 EndY=36.9748 EndZ=0
    g4: LineSegment StartX=16.044 StartY=36.9748 StartZ=0 EndX=18.9109 EndY=40.0311 EndZ=0
    g5: LineSegment StartX=-18.9734 StartY=40.0311 StartZ=0 EndX=18.9109 EndY=40.0311 EndZ=0
  constraints (7):
    c: Coincident(g2,g1)
    c: Coincident(g2,g0)
    c: Horizontal(g2)
    c: Coincident(g3,g0)
    c: Coincident(g5,g3)
    c: Coincident(g5,g4)
    c: Horizontal(g5)
FEATURE [Part::Extrusion] Extrude029
  Base = -> Sketch012
  Dir = (0,0,1)
  DirMode = 2
  FaceMakerClass = Part::FaceMakerBullseye
  LengthFwd = -112
  LengthRev = 0
  Solid = true
  Symmetric = false
FEATURE [Part::Cut] Cut061090
  Base = -> Box051
  Tool = -> Box049
FEATURE [Part::MultiFuse] Fusion209  label="Arca plate base005"
  Placement = pos=(0,-0.5,0) rot=(0,0,1;0rad)
  Shapes = -> [Extrude029,Cut061090]
FEATURE [Part::MultiFuse] Fusion210
  Shapes = -> [Box050,Box047,Cylinder014005343]
FEATURE [Part::MultiFuse] Fusion211
  Shapes = -> [Fusion209,Cylinder014005342,Cylinder014005344,Box048,Box046]
FEATURE [Part::Cut] Cut061091
  Base = -> Fusion211
  Tool = -> Fusion210
FEATURE [Part::MultiFuse] Fusion212  label="Srouby"
  Placement = pos=(0,0,-0.5) rot=(0,0,1;0rad)
  Shapes = -> [Screw,Nut009]
FEATURE [Part::MultiFuse] Fusion213  label="Srouby002"
  Placement = pos=(0,0,-97.5) rot=(0,0,1;0rad)
  Shapes = -> [Screw002,Nut012]
FEATURE [Part::MultiFuse] Fusion214  label="Srouby003"
  Placement = pos=(80.5,0,-97.5) rot=(0,0,1;0rad)
  Shapes = -> [Screw003,Nut011]
FEATURE [Part::MultiFuse] Fusion215  label="Srouby001"
  Placement = pos=(80.5,0,-0.5) rot=(0,0,1;0rad)
  Shapes = -> [Screw001,Nut010]
FEATURE [Part::MultiFuse] Fusion216
  Shapes = -> [Fusion212,Fusion215,Fusion213,Fusion214]
FEATURE [Part::Cut] Cut061092  label="Drzak 01"
  Base = -> Cut061091
  Placement = pos=(0,0,0) rot=(1,0,0;1.5708rad)
  Tool = -> Fusion216
FEATURE [App::Part] Part018  label="Telescop Holder"
  Group = -> [Fusion216,Sketch012,Cut061090,Cut061091,Cylinder014005344,Cylinder014005343,Box051,Box050,Box046,Cylinder014005342,Nut012,Extrude029,Screw,Screw002,Screw001,Nut010,Nut009,Screw003,Nut011,Fusion214,Fusion215,Fusion209,Fusion212,Fusion213,Fusion210,Fusion211,Box049,Box047,Box048,Cut061092]
  License = CC BY 3.0
  LicenseURL = http://creativecommons.org/licenses/by/3.0/
  Origin = -> Origin018
  Placement = pos=(0,110,118) rot=(1,0,0;1.5708rad)
FEATURE [Part::Cylinder] Cylinder014005345  label="tyč závaží"
  Angle = 360
  AttacherType = Attacher::AttachEngine3D
  Height = 300
  Placement = pos=(0,55,88) rot=(1,0,0;1.5708rad)
  Radius = 3
FEATURE [Part::Cylinder] Cylinder014005346  label="Válec317"
  Angle = 360
  AttacherType = Attacher::AttachEngine3D
  Height = 60
  Placement = pos=(0,-200,88) rot=(1,0,0;1.5708rad)
  Radius = 50
FEATURE [Part::Cylinder] Cylinder014005347  label="Válec318"
  Angle = 360
  AttacherType = Attacher::AttachEngine3D
  Height = 58
  Placement = pos=(0,-200,88) rot=(1,0,0;1.5708rad)
  Radius = 44
FEATURE [Part::Cut] Cut061093
  Base = -> Cylinder014005346
  Tool = -> Cylinder014005347
FEATURE [Part::Cylinder] Cylinder014005348  label="Válec319"
  Angle = 360
  AttacherType = Attacher::AttachEngine3D
  Height = 56
  Placement = pos=(0,-203.5,88) rot=(1,0,0;1.5708rad)
  Radius = 10
FEATURE [Part::MultiFuse] Fusion217  label="Zavazí dno"
  Placement = pos=(0,-2,0) rot=(0,0,1;0rad)
  Shapes = -> [Cut061093,Cylinder014005348]
FEATURE [Part::Cylinder] Cylinder014005349  label="Válec320"
  Angle = 360
  AttacherType = Attacher::AttachEngine3D
  Height = 2
  Placement = pos=(0,-200,88) rot=(1,0,0;1.5708rad)
  Radius = 50
FEATURE [Part::Cylinder] Cylinder014005350  label="Válec321"
  Angle = 360
  AttacherType = Attacher::AttachEngine3D
  Height = 3.5
  Placement = pos=(0,-200,88) rot=(1,0,0;1.5708rad)
  Radius = 44
FEATURE [Part::MultiFuse] Fusion218  label="zaazi vyko"
  Shapes = -> [Cylinder014005350,Cylinder014005349]
FEATURE [Part::Cylinder] Cylinder014005351  label="tyč závaží001"
  Angle = 360
  AttacherType = Attacher::AttachEngine3D
  Height = 350
  Placement = pos=(0,85,88) rot=(1,0,0;1.5708rad)
  Radius = 3
FEATURE [Part::FeaturePython] Nut013  label="M6-Nut006"  # Fasteners workbench fastener (typed FeaturePython)
  Placement = pos=(0,-258,88) rot=(1,0,0;1.5708rad)
  diameter = 8
  invert = false
  matchOuter = false
  offset = 0
  thread = false
  type = 1
FEATURE [Part::FeaturePython] Screw006  label="M2.5x8-Screw"  # Fasteners workbench fastener (typed FeaturePython)
  Placement = pos=(0,-199,31) rot=(-1,0,0;1.5708rad)
  diameter = 3
  invert = false
  length = 3
  matchOuter = false
  offset = 0
  thread = false
  type = 12
FEATURE [Part::Feature] Screw006_solid  label="vyko M2.5x8"
  Placement = pos=(0,0,10) rot=(0,0,1;0rad)
  shape: bbox 4.5 x 8.524 x 4.5 mm, 11 faces (baked)
FEATURE [Part::Feature] Screw006_solid001  label="vyko M2.5x009"
  Placement = pos=(0,0,104) rot=(0,0,1;0rad)
  shape: bbox 4.5 x 8.524 x 4.5 mm, 11 faces (baked)
FEATURE [Part::Feature] Screw006_solid002  label="vyko M2.5x010"
  Placement = pos=(47,0,57) rot=(0,0,1;0rad)
  shape: bbox 4.5 x 8.524 x 4.5 mm, 11 faces (baked)
FEATURE [Part::Feature] Screw006_solid003  label="vyko M2.5x011"
  Placement = pos=(-47,0,57) rot=(0,0,1;0rad)
  shape: bbox 4.5 x 8.524 x 4.5 mm, 11 faces (baked)
FEATURE [Part::MultiFuse] Fusion219  label="srouby diry zavazi"
  Shapes = -> [Cylinder014005351,Screw006_solid,Screw006_solid001,Screw006_solid002,Screw006_solid003,Nut013]
FEATURE [Part::Cut] Cut061094  label="Weight  bottom"
  Base = -> Fusion217
  Tool = -> Fusion219
FEATURE [Part::FeaturePython] Nut014  label="M6-Nut005"  # Fasteners workbench fastener (typed FeaturePython)
  Placement = pos=(0,-238,88) rot=(1,0,0;1.5708rad)
  diameter = 8
  invert = false
  matchOuter = false
  offset = 0
  thread = false
  type = 1
FEATURE [Part::Cylinder] Cylinder014005352  label="tyč závaží002"
  Angle = 360
  AttacherType = Attacher::AttachEngine3D
  Height = 300
  Placement = pos=(0,55,88) rot=(1,0,0;1.5708rad)
  Radius = 3
FEATURE [Part::Feature] Screw006_solid004  label="vyko M2.5x012"
  Placement = pos=(0,0,104) rot=(0,0,1;0rad)
  shape: bbox 4.5 x 8.524 x 4.5 mm, 11 faces (baked)
FEATURE [Part::Feature] Screw006_solid005  label="vyko M2.5x013"
  Placement = pos=(47,0,57) rot=(0,0,1;0rad)
  shape: bbox 4.5 x 8.524 x 4.5 mm, 11 faces (baked)
FEATURE [Part::Feature] Screw006_solid006  label="vyko M2.5x014"
  Placement = pos=(-47,0,57) rot=(0,0,1;0rad)
  shape: bbox 4.5 x 8.524 x 4.5 mm, 11 faces (baked)
FEATURE [Part::Feature] Screw006_solid007  label="vyko M2.5x015"
  Placement = pos=(0,0,10) rot=(0,0,1;0rad)
  shape: bbox 4.5 x 8.524 x 4.5 mm, 11 faces (baked)
FEATURE [Part::MultiFuse] Fusion220  label="srouby diry zavazi001"
  Shapes = -> [Cylinder014005352,Screw006_solid007,Screw006_solid004,Screw006_solid005,Screw006_solid006,Nut014]
FEATURE [Part::Cut] Cut061095  label="Weight top"
  Base = -> Fusion218
  Tool = -> Fusion220
FEATURE [Part::Cylinder] Cylinder014005353  label="dira"
  Angle = 360
  AttacherType = Attacher::AttachEngine3D
  Height = 65
  Placement = pos=(-32,-16,-27) rot=(0,1,0;1.5708rad)
  Radius = 1.25
FEATURE [Part::Cut] Cut061096  label="Axis 1 RA"
  Base = -> Cut061089
  Tool = -> Cylinder014005353
FEATURE [Part::Cylinder] Cylinder014005355  label="dira001"
  Angle = 360
  AttacherType = Attacher::AttachEngine3D
  Height = 65
  Placement = pos=(-32,-32,99) rot=(0,1,0;1.5708rad)
  Radius = 1.25
FEATURE [Part::Cut] Cut061097  label="Axis 2 DEC"
  Base = -> Cut061087
  Tool = -> Cylinder014005355
